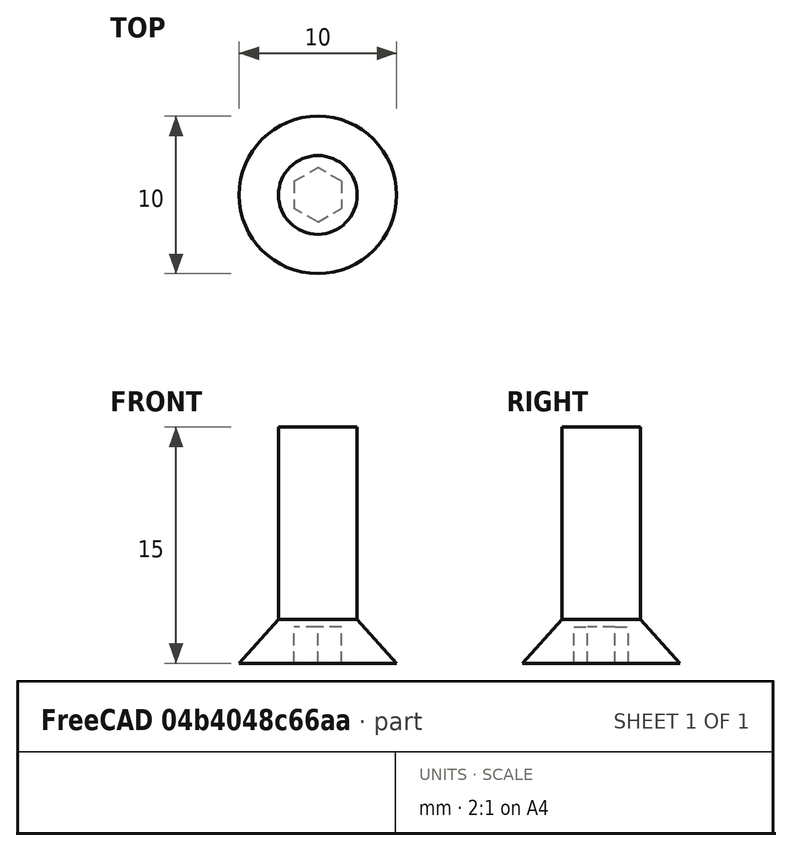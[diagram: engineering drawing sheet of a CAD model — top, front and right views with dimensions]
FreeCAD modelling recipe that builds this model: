
FCSTD DOCUMENT  (FreeCAD 1.0R39109 (Git))
Label: dbox_asm
License: All rights reserved
LicenseURL: https://en.wikipedia.org/wiki/All_rights_reserved
objects: App::Link×162, App::FeaturePython×132, Assembly::AssemblyLink×11, Assembly::JointGroup×2, Part::Feature×1, Assembly::AssemblyObject×1
note: 1 computed .brp shape members not serialized (recipe doc carries the construction recipe); baked Part::Feature solids carry a one-line shape summary decoded from their .brp
EXTERNAL_REF file=../parts/T-Slot_20_height.FCStd obj=Body
EXTERNAL_REF file=../parts/T-Slot_20_length.FCStd obj=Body
EXTERNAL_REF file=../parts/T-Slot_20_width.FCStd obj=Body
EXTERNAL_REF file=../downloads/2020-corner-bracket.FCStd obj=Part
EXTERNAL_REF file=../parts/T-nut_20.FCStd obj=Part__Feature
EXTERNAL_REF file=roof_holder_asm.FCStd obj=Assembly
EXTERNAL_REF file=roof_holder_asm.FCStd obj=roof_holder
EXTERNAL_REF file=roof_holder_asm.FCStd obj=Hex_socket_countersunk_head_screw_ISO_10642_M5_15_0
EXTERNAL_REF file=roof_holder_asm.FCStd obj=Hex_socket_countersunk_head_screw_ISO_10642_M5_15_001
EXTERNAL_REF file=asm_roof.FCStd obj=Assembly
EXTERNAL_REF file=asm_roof.FCStd obj=plate_roof001
EXTERNAL_REF file=asm_roof.FCStd obj=linear_slide
EXTERNAL_REF file=asm_roof.FCStd obj=linear_slide001
EXTERNAL_REF file=asm_roof.FCStd obj=asm_SHF002
EXTERNAL_REF file=asm_shf.FCStd obj=SHF12
EXTERNAL_REF file=asm_shf.FCStd obj=Hex_socket_head_cap_screw_DIN_912_M4_15_0
EXTERNAL_REF file=asm_shf.FCStd obj=Hex_socket_head_cap_screw_DIN_912_M5_15_0
EXTERNAL_REF file=asm_shf.FCStd obj=Hex_socket_head_cap_screw_DIN_912_M5_15_001
EXTERNAL_REF file=asm_roof.FCStd obj=asm_SHF003
EXTERNAL_REF file=asm_roof.FCStd obj=asm_cam_holder
EXTERNAL_REF file=asm_plate_front_back.FCStd obj=Assembly
EXTERNAL_REF file=asm_plate_front_back.FCStd obj=plate_front_back
EXTERNAL_REF file=asm_plate_front_back.FCStd obj=Hex_screw_M5_10_001
EXTERNAL_REF file=asm_plate_front_back.FCStd obj=Hex_screw_M5_10_002
EXTERNAL_REF file=asm_plate_front_back.FCStd obj=Hex_screw_M5_10_003
EXTERNAL_REF file=asm_plate_front_back.FCStd obj=Hex_screw_M5_10_0
EXTERNAL_REF file=asm_plate_side.FCStd obj=Assembly
EXTERNAL_REF file=asm_plate_side.FCStd obj=plate_side
EXTERNAL_REF file=asm_plate_side.FCStd obj=TAH15_M5_L6
EXTERNAL_REF file=asm_plate_side.FCStd obj=TAH15_M5_L007
EXTERNAL_REF file=asm_plate_side.FCStd obj=TAH15_M5_L008
EXTERNAL_REF file=asm_plate_side.FCStd obj=TAH15_M5_L009
EXTERNAL_REF file=../secondary/bolts.FCStd obj=Body004

FEATURE [App::Link] Tslot20_heigh
  LinkedObject = -> <external ../parts/T-Slot_20_height.FCStd>#Body
FEATURE [App::FeaturePython] GroundedJoint  # Assembly grounded joint (typed FeaturePython)
  ObjectToGround = -> Tslot20_heigh
FEATURE [App::Link] Tslot20_len
  LinkPlacement = pos=(10,4e-16,570) rot=(0,1,0;1.5708rad)
  LinkedObject = -> <external ../parts/T-Slot_20_length.FCStd>#Body
  Placement = pos=(10,4e-16,570) rot=(0,1,0;1.5708rad)
FEATURE [App::FeaturePython] Joint  label="Fixed"  # Assembly joint (typed FeaturePython)
  Activated = true
  AngleMax = 0
  AngleMin = 0
  Detach1 = false
  Detach2 = false
  Distance = 0
  Distance2 = 0
  EnableAngleMax = false
  EnableAngleMin = false
  EnableLengthMax = false
  EnableLengthMin = false
  JointType = 0 (Fixed)
  LengthMax = 0
  LengthMin = 0
  Offset2 = pos=(0,0,0) rot=(0,0,1;1.5708rad)
  Placement1 = pos=(10,-6.55,580) rot=(-0.57735,-0.57735,0.57735;4.18879rad)
  Placement2 = pos=(-10,-6.55,1.8e-15) rot=(1,0,0;4.71239rad)
  Reference1 = -> Assembly [Tslot20_heigh.Edge52,Tslot20_heigh.Edge52]
  Reference2 = -> Assembly [Tslot20_len.Edge39,Tslot20_len.Edge39]
FEATURE [App::Link] Tslot20_heigh001
  LinkPlacement = pos=(420,3.92e-14,-5.3e-14) rot=(0,0,1;0rad)
  LinkedObject = -> <external ../parts/T-Slot_20_height.FCStd>#Body
  Placement = pos=(420,3.92e-14,-5.3e-14) rot=(0,0,1;0rad)
FEATURE [App::FeaturePython] Joint001  label="Fixed001"  # Assembly joint (typed FeaturePython)
  Activated = true
  AngleMax = 0
  AngleMin = 0
  Detach1 = false
  Detach2 = false
  Distance = 0
  Distance2 = 0
  EnableAngleMax = false
  EnableAngleMin = false
  EnableLengthMax = false
  EnableLengthMin = false
  JointType = 0 (Fixed)
  LengthMax = 0
  LengthMin = 0
  Offset2 = pos=(0,0,0) rot=(0,0,1;1.5708rad)
  Placement1 = pos=(-10,6.55,400) rot=(0.57735,0.57735,0.57735;4.18879rad)
  Placement2 = pos=(-10,6.55,580) rot=(1,0,0;4.71239rad)
  Reference1 = -> Assembly [Tslot20_len.Edge68,Tslot20_len.Edge68]
  Reference2 = -> Assembly [Tslot20_heigh001.Edge68,Tslot20_heigh001.Edge68]
FEATURE [App::Link] Tslot20_wid
  LinkPlacement = pos=(7e-16,10,570) rot=(0.57735,0.57735,0.57735;4.18879rad)
  LinkedObject = -> <external ../parts/T-Slot_20_width.FCStd>#Body
  Placement = pos=(7e-16,10,570) rot=(0.57735,0.57735,0.57735;4.18879rad)
FEATURE [App::FeaturePython] Joint002  label="Fixed002"  # Assembly joint (typed FeaturePython)
  Activated = true
  AngleMax = 0
  AngleMin = 0
  Detach1 = false
  Detach2 = false
  Distance = 0
  Distance2 = 0
  EnableAngleMax = false
  EnableAngleMin = false
  EnableLengthMax = false
  EnableLengthMin = false
  JointType = 0 (Fixed)
  LengthMax = 0
  LengthMin = 0
  Offset2 = pos=(0,0,0) rot=(0,0,1;1.5708rad)
  Placement1 = pos=(10,-6.55,0) rot=(-0.57735,-0.57735,0.57735;4.18879rad)
  Placement2 = pos=(-6.55,10,580) rot=(0.57735,-0.57735,0.57735;4.18879rad)
  Reference1 = -> Assembly [Tslot20_wid.Edge14,Tslot20_wid.Edge14]
  Reference2 = -> Assembly [Tslot20_heigh.Edge3,Tslot20_heigh.Edge3]
FEATURE [App::Link] Tslot20_heigh002
  LinkPlacement = pos=(1e-16,220,-3.59e-14) rot=(0,0,1;0rad)
  LinkedObject = -> <external ../parts/T-Slot_20_height.FCStd>#Body
  Placement = pos=(1e-16,220,-3.59e-14) rot=(0,0,1;0rad)
FEATURE [App::FeaturePython] Joint003  label="Fixed003"  # Assembly joint (typed FeaturePython)
  Activated = true
  AngleMax = 0
  AngleMin = 0
  Detach1 = false
  Detach2 = false
  Distance = 0
  Distance2 = 0
  EnableAngleMax = false
  EnableAngleMin = false
  EnableLengthMax = false
  EnableLengthMin = false
  JointType = 0 (Fixed)
  LengthMax = 0
  LengthMin = 0
  Offset2 = pos=(0,0,0) rot=(0,0,1;1.5708rad)
  Placement1 = pos=(10,-6.55,200) rot=(-0.57735,-0.57735,0.57735;4.18879rad)
  Placement2 = pos=(-6.55,-10,580) rot=(-0.57735,0.57735,0.57735;4.18879rad)
  Reference1 = -> Assembly [Tslot20_wid.Edge52,Tslot20_wid.Edge52]
  Reference2 = -> Assembly [Tslot20_heigh002.Edge43,Tslot20_heigh002.Edge43]
FEATURE [App::Link] Tslot20_len001
  LinkPlacement = pos=(10,220,570) rot=(0,1,0;1.5708rad)
  LinkedObject = -> <external ../parts/T-Slot_20_length.FCStd>#Body
  Placement = pos=(10,220,570) rot=(0,1,0;1.5708rad)
FEATURE [App::FeaturePython] Joint004  label="Fixed004"  # Assembly joint (typed FeaturePython)
  Activated = true
  AngleMax = 0
  AngleMin = 0
  Detach1 = false
  Detach2 = false
  Distance = 0
  Distance2 = 0
  EnableAngleMax = false
  EnableAngleMin = false
  EnableLengthMax = false
  EnableLengthMin = false
  JointType = 0 (Fixed)
  LengthMax = 0
  LengthMin = 0
  Offset2 = pos=(0,0,0) rot=(0,0,1;1.5708rad)
  Placement1 = pos=(10,6.55,580) rot=(-0.57735,-0.57735,0.57735;4.18879rad)
  Placement2 = pos=(-10,6.55,-1.8e-15) rot=(1,0,0;4.71239rad)
  Reference1 = -> Assembly [Tslot20_heigh002.Edge60,Tslot20_heigh002.Edge60]
  Reference2 = -> Assembly [Tslot20_len001.Edge31,Tslot20_len001.Edge31]
FEATURE [App::Link] Tslot20_heigh003
  LinkPlacement = pos=(420,220,-8.25e-14) rot=(0,0,1;0rad)
  LinkedObject = -> <external ../parts/T-Slot_20_height.FCStd>#Body
  Placement = pos=(420,220,-8.25e-14) rot=(0,0,1;0rad)
FEATURE [App::FeaturePython] Joint005  label="Fixed005"  # Assembly joint (typed FeaturePython)
  Activated = true
  AngleMax = 0
  AngleMin = 0
  Detach1 = false
  Detach2 = false
  Distance = 0
  Distance2 = 0
  EnableAngleMax = false
  EnableAngleMin = false
  EnableLengthMax = false
  EnableLengthMin = false
  JointType = 0 (Fixed)
  LengthMax = 0
  LengthMin = 0
  Offset2 = pos=(0,0,0) rot=(0,0,1;1.5708rad)
  Placement1 = pos=(-10,6.55,400) rot=(0.57735,0.57735,0.57735;4.18879rad)
  Placement2 = pos=(-10,6.55,580) rot=(1,0,0;4.71239rad)
  Reference1 = -> Assembly [Tslot20_len001.Edge68,Tslot20_len001.Edge68]
  Reference2 = -> Assembly [Tslot20_heigh003.Edge68,Tslot20_heigh003.Edge68]
FEATURE [App::Link] Tslot20_wid001
  LinkPlacement = pos=(420,10,570) rot=(-1,0,0;1.5708rad)
  LinkedObject = -> <external ../parts/T-Slot_20_width.FCStd>#Body
  Placement = pos=(420,10,570) rot=(-1,0,0;1.5708rad)
FEATURE [App::FeaturePython] Joint006  label="Fixed006"  # Assembly joint (typed FeaturePython)
  Activated = true
  AngleMax = 0
  AngleMin = 0
  Detach1 = false
  Detach2 = false
  Distance = 0
  Distance2 = 0
  EnableAngleMax = false
  EnableAngleMin = false
  EnableLengthMax = false
  EnableLengthMin = false
  JointType = 0 (Fixed)
  LengthMax = 0
  LengthMin = 0
  Offset2 = pos=(0,0,0) rot=(0,0,1;1.5708rad)
  Placement1 = pos=(6.55,10,580) rot=(0.707107,0,0.707107;3.14159rad)
  Placement2 = pos=(6.55,-10,-1.8e-15) rot=(-0.57735,0.57735,0.57735;4.18879rad)
  Reference1 = -> Assembly [Tslot20_heigh001.Edge61,Tslot20_heigh001.Edge61]
  Reference2 = -> Assembly [Tslot20_wid001.Edge13,Tslot20_wid001.Edge13]
FEATURE [App::Link] Tslot20_len002
  LinkPlacement = pos=(10,2.9e-15,10) rot=(0,1,0;1.5708rad)
  LinkedObject = -> <external ../parts/T-Slot_20_length.FCStd>#Body
  Placement = pos=(10,2.9e-15,10) rot=(0,1,0;1.5708rad)
FEATURE [App::FeaturePython] Joint007  label="Fixed007"  # Assembly joint (typed FeaturePython)
  Activated = true
  AngleMax = 0
  AngleMin = 0
  Detach1 = false
  Detach2 = false
  Distance = 0
  Distance2 = 0
  EnableAngleMax = false
  EnableAngleMin = false
  EnableLengthMax = false
  EnableLengthMin = false
  JointType = 0 (Fixed)
  LengthMax = 0
  LengthMin = 0
  Offset2 = pos=(0,0,0) rot=(0,0,-1;1.5708rad)
  Placement1 = pos=(10,6.55,0) rot=(-0.57735,-0.57735,0.57735;4.18879rad)
  Placement2 = pos=(10,6.55,0) rot=(0,-0.707107,0.707107;3.14159rad)
  Reference1 = -> Assembly [Tslot20_len002.Edge22,Tslot20_len002.Edge22]
  Reference2 = -> Assembly [Tslot20_heigh.Edge22,Tslot20_heigh.Edge22]
FEATURE [App::Link] Tslot20_len003
  LinkPlacement = pos=(10,220,10) rot=(0,1,0;1.5708rad)
  LinkedObject = -> <external ../parts/T-Slot_20_length.FCStd>#Body
  Placement = pos=(10,220,10) rot=(0,1,0;1.5708rad)
FEATURE [App::FeaturePython] Joint008  label="Fixed008"  # Assembly joint (typed FeaturePython)
  Activated = true
  AngleMax = 0
  AngleMin = 0
  Detach1 = false
  Detach2 = false
  Distance = 0
  Distance2 = 0
  EnableAngleMax = false
  EnableAngleMin = false
  EnableLengthMax = false
  EnableLengthMin = false
  JointType = 0 (Fixed)
  LengthMax = 0
  LengthMin = 0
  Offset2 = pos=(0,0,0) rot=(0,0,-1;1.5708rad)
  Placement1 = pos=(-10,6.55,0) rot=(0.57735,0.57735,0.57735;4.18879rad)
  Placement2 = pos=(10,6.55,400) rot=(0,-0.707107,0.707107;3.14159rad)
  Reference1 = -> Assembly [Tslot20_heigh003.Edge31,Tslot20_heigh003.Edge31]
  Reference2 = -> Assembly [Tslot20_len003.Edge60,Tslot20_len003.Edge60]
FEATURE [App::Link] Tslot20_wid002
  LinkPlacement = pos=(-6.2e-15,10,30) rot=(1,0,0;4.71239rad)
  LinkedObject = -> <external ../parts/T-Slot_20_width.FCStd>#Body
  Placement = pos=(-6.2e-15,10,30) rot=(1,0,0;4.71239rad)
FEATURE [App::Link] Tslot20_wid003
  LinkPlacement = pos=(420,210,30) rot=(1,0,0;1.5708rad)
  LinkedObject = -> <external ../parts/T-Slot_20_width.FCStd>#Body
  Placement = pos=(420,210,30) rot=(1,0,0;1.5708rad)
FEATURE [App::FeaturePython] Joint009  label="Fixed009"  # Assembly joint (typed FeaturePython)
  Activated = true
  AngleMax = 0
  AngleMin = 0
  Detach1 = false
  Detach2 = false
  Distance = 0
  Distance2 = 0
  EnableAngleMax = false
  EnableAngleMin = false
  EnableLengthMax = false
  EnableLengthMin = false
  JointType = 0 (Fixed)
  LengthMax = 0
  LengthMin = 0
  Offset2 = pos=(0,-20,0) rot=(0,0,-1;1.5708rad)
  Placement1 = pos=(-6.55,-10,0) rot=(-0.707107,0,0.707107;3.14159rad)
  Placement2 = pos=(-6.55,30,200) rot=(0.57735,0.57735,0.57735;2.0944rad)
  Reference1 = -> Assembly [Tslot20_heigh002.Edge5,Tslot20_heigh002.Edge5]
  Reference2 = -> Assembly [Tslot20_wid002.Edge3,Tslot20_wid002.Edge3]
FEATURE [App::FeaturePython] Joint010  label="Fixed010"  # Assembly joint (typed FeaturePython)
  Activated = true
  AngleMax = 0
  AngleMin = 0
  Detach1 = false
  Detach2 = false
  Distance = 0
  Distance2 = 0
  EnableAngleMax = false
  EnableAngleMin = false
  EnableLengthMax = false
  EnableLengthMin = false
  JointType = 0 (Fixed)
  LengthMax = 0
  LengthMin = 0
  Offset2 = pos=(0,20,0) rot=(0,0,-1;1.5708rad)
  Placement1 = pos=(6.55,10,0) rot=(0.707107,0,0.707107;3.14159rad)
  Placement2 = pos=(6.55,-30,200) rot=(-0.57735,-0.57735,0.57735;2.0944rad)
  Reference1 = -> Assembly [Tslot20_heigh001.Edge23,Tslot20_heigh001.Edge23]
  Reference2 = -> Assembly [Tslot20_wid003.Edge51,Tslot20_wid003.Edge51]
FEATURE [App::Link] Body  label="corner1"
  LinkPlacement = pos=(20,-0.05,30) rot=(0,0,1;0rad)
  LinkedObject = -> <external ../downloads/2020-corner-bracket.FCStd>#Part
  Placement = pos=(20,-0.05,30) rot=(0,0,1;0rad)
FEATURE [App::FeaturePython] Joint011  label="Fixed011"  # Assembly joint (typed FeaturePython)
  Activated = true
  AngleMax = 0
  AngleMin = 0
  Detach1 = false
  Detach2 = false
  Distance = 0
  Distance2 = 0
  EnableAngleMax = false
  EnableAngleMin = false
  EnableLengthMax = false
  EnableLengthMin = false
  JointType = 0 (Fixed)
  LengthMax = 0
  LengthMin = 0
  Offset2 = pos=(0,0,-2) rot=(0,0,1;1.5708rad)
  Placement1 = pos=(-10,-8.5,-10) rot=(-0.57735,-0.57735,0.57735;4.18879rad)
  Placement2 = pos=(-10,-8.55,-1.8e-15) rot=(1,0,0;4.71239rad)
  Reference1 = -> Assembly [Body.Edge15,Body.Vertex13]
  Reference2 = -> Assembly [Tslot20_len002.Edge39,Tslot20_len002.Edge39]
FEATURE [App::Link] Body001  label="corner2"
  LinkPlacement = pos=(0.05,200,50) rot=(0,0,-1;1.5708rad)
  LinkedObject = -> <external ../downloads/2020-corner-bracket.FCStd>#Part
  Placement = pos=(0.05,200,50) rot=(0,0,-1;1.5708rad)
FEATURE [App::Link] Body002  label="corner3"
  LinkPlacement = pos=(0.05,20,50) rot=(0,0,1;1.5708rad)
  LinkedObject = -> <external ../downloads/2020-corner-bracket.FCStd>#Part
  Placement = pos=(0.05,20,50) rot=(0,0,1;1.5708rad)
FEATURE [App::Link] Body003  label="corner4"
  LinkPlacement = pos=(20,-0.05,550) rot=(0,1,0;1.5708rad)
  LinkedObject = -> <external ../downloads/2020-corner-bracket.FCStd>#Part
  Placement = pos=(20,-0.05,550) rot=(0,1,0;1.5708rad)
FEATURE [App::FeaturePython] Joint012  label="Fixed012"  # Assembly joint (typed FeaturePython)
  Activated = true
  AngleMax = 0
  AngleMin = 0
  Detach1 = false
  Detach2 = false
  Distance = 0
  Distance2 = 0
  EnableAngleMax = false
  EnableAngleMin = false
  EnableLengthMax = false
  EnableLengthMin = false
  JointType = 0 (Fixed)
  LengthMax = 0
  LengthMin = 0
  Offset2 = pos=(0,0,-2) rot=(0,0,-1;1.5708rad)
  Placement1 = pos=(6.55,-10,0) rot=(-0.707107,0,0.707107;3.14159rad)
  Placement2 = pos=(-10,-6.5,-10) rot=(0,-0.707107,0.707107;3.14159rad)
  Reference1 = -> Assembly [Tslot20_wid002.Edge13,Tslot20_wid002.Edge13]
  Reference2 = -> Assembly [Body002.Edge15,Body002.Vertex13]
FEATURE [App::FeaturePython] Joint013  label="Fixed013"  # Assembly joint (typed FeaturePython)
  Activated = true
  AngleMax = 0
  AngleMin = 0
  Detach1 = false
  Detach2 = false
  Distance = 0
  Distance2 = 0
  EnableAngleMax = false
  EnableAngleMin = false
  EnableLengthMax = false
  EnableLengthMin = false
  JointType = 0 (Fixed)
  LengthMax = 0
  LengthMin = 0
  Offset2 = pos=(0,0,2) rot=(0,0,1;1.5708rad)
  Placement1 = pos=(6.55,-10,200) rot=(-0.707107,0,0.707107;3.14159rad)
  Placement2 = pos=(-10,6.5,-10) rot=(-1,0,0;4.71239rad)
  Reference1 = -> Assembly [Tslot20_wid002.Edge51,Tslot20_wid002.Edge51]
  Reference2 = -> Assembly [Body001.Edge15,Body001.Vertex12]
FEATURE [App::FeaturePython] Joint014  label="Fixed014"  # Assembly joint (typed FeaturePython)
  Activated = true
  AngleMax = 0
  AngleMin = 0
  Detach1 = false
  Detach2 = false
  Distance = 0
  Distance2 = 0
  EnableAngleMax = false
  EnableAngleMin = false
  EnableLengthMax = false
  EnableLengthMin = false
  JointType = 0 (Fixed)
  LengthMax = 0
  LengthMin = 0
  Offset2 = pos=(0,0,-2) rot=(0,0,1;0rad)
  Placement1 = pos=(10,-6.55,0) rot=(-0.57735,-0.57735,0.57735;4.18879rad)
  Placement2 = pos=(-10,-6.5,-10) rot=(-0.57735,-0.57735,0.57735;4.18879rad)
  Reference1 = -> Assembly [Tslot20_len.Edge14,Tslot20_len.Edge14]
  Reference2 = -> Assembly [Body003.Edge15,Body003.Vertex13]
FEATURE [App::Link] Body004  label="corner5"
  LinkPlacement = pos=(20,220.05,30) rot=(0,0,1;0rad)
  LinkedObject = -> <external ../downloads/2020-corner-bracket.FCStd>#Part
  Placement = pos=(20,220.05,30) rot=(0,0,1;0rad)
FEATURE [App::FeaturePython] Joint015  label="Fixed015"  # Assembly joint (typed FeaturePython)
  Activated = true
  AngleMax = 0
  AngleMin = 0
  Detach1 = false
  Detach2 = false
  Distance = 0
  Distance2 = 0
  EnableAngleMax = false
  EnableAngleMin = false
  EnableLengthMax = false
  EnableLengthMin = false
  JointType = 0 (Fixed)
  LengthMax = 0
  LengthMin = 0
  Offset2 = pos=(0,0,2) rot=(0,0,1;1.5708rad)
  Placement1 = pos=(-10,6.55,-1.8e-15) rot=(0.57735,0.57735,0.57735;4.18879rad)
  Placement2 = pos=(-10,6.5,-10) rot=(-1,0,0;4.71239rad)
  Reference1 = -> Assembly [Tslot20_len003.Edge31,Tslot20_len003.Edge31]
  Reference2 = -> Assembly [Body004.Edge15,Body004.Vertex12]
FEATURE [App::Link] Body005  label="corner6"
  LinkPlacement = pos=(-0.05,200,550) rot=(-0.707107,0.707107,0;3.14159rad)
  LinkedObject = -> <external ../downloads/2020-corner-bracket.FCStd>#Part
  Placement = pos=(-0.05,200,550) rot=(-0.707107,0.707107,0;3.14159rad)
FEATURE [App::Link] Body006  label="corner7"
  LinkPlacement = pos=(-0.55,20,550) rot=(-0.57735,0.57735,0.57735;2.0944rad)
  LinkedObject = -> <external ../downloads/2020-corner-bracket.FCStd>#Part
  Placement = pos=(-0.55,20,550) rot=(-0.57735,0.57735,0.57735;2.0944rad)
FEATURE [App::Link] Body007  label="corner8"
  LinkPlacement = pos=(400,219.45,30) rot=(0,0,1;3.14159rad)
  LinkedObject = -> <external ../downloads/2020-corner-bracket.FCStd>#Part
  Placement = pos=(400,219.45,30) rot=(0,0,1;3.14159rad)
FEATURE [App::Link] Body008  label="corner9"
  LinkPlacement = pos=(20,219.6,550) rot=(0,1,0;1.5708rad)
  LinkedObject = -> <external ../downloads/2020-corner-bracket.FCStd>#Part
  Placement = pos=(20,219.6,550) rot=(0,1,0;1.5708rad)
FEATURE [App::FeaturePython] Joint016  label="Fixed016"  # Assembly joint (typed FeaturePython)
  Activated = true
  AngleMax = 0
  AngleMin = 0
  Detach1 = false
  Detach2 = false
  Distance = 0
  Distance2 = 0
  EnableAngleMax = false
  EnableAngleMin = false
  EnableLengthMax = false
  EnableLengthMin = false
  JointType = 0 (Fixed)
  LengthMax = 0
  LengthMin = 0
  Offset2 = pos=(0,0,-6) rot=(0,0,1;3.14159rad)
  Placement1 = pos=(-10,-6.55,0) rot=(0.57735,0.57735,0.57735;4.18879rad)
  Placement2 = pos=(-10,6,-10) rot=(-0.57735,0.57735,-0.57735;4.18879rad)
  Reference1 = -> Assembly [Tslot20_wid.Edge39,Tslot20_wid.Edge39]
  Reference2 = -> Assembly [Body006.Edge15,Body006.Edge15]
FEATURE [App::FeaturePython] Joint017  label="Fixed017"  # Assembly joint (typed FeaturePython)
  Activated = true
  AngleMax = 0
  AngleMin = 0
  Detach1 = false
  Detach2 = false
  Distance = 0
  Distance2 = 0
  EnableAngleMax = false
  EnableAngleMin = false
  EnableLengthMax = false
  EnableLengthMin = false
  JointType = 0 (Fixed)
  LengthMax = 0
  LengthMin = 0
  Offset2 = pos=(0,0,-6) rot=(0,0,-1;1.5708rad)
  Placement1 = pos=(-10,-6.55,400) rot=(0.57735,0.57735,0.57735;4.18879rad)
  Placement2 = pos=(-10,6,-10) rot=(0,-0.707107,0.707107;3.14159rad)
  Reference1 = -> Assembly [Tslot20_len003.Edge76,Tslot20_len003.Edge76]
  Reference2 = -> Assembly [Body007.Edge15,Body007.Edge15]
FEATURE [App::FeaturePython] Joint018  label="Fixed018"  # Assembly joint (typed FeaturePython)
  Activated = true
  AngleMax = 0
  AngleMin = 0
  Detach1 = false
  Detach2 = false
  Distance = 0
  Distance2 = 0
  EnableAngleMax = false
  EnableAngleMin = false
  EnableLengthMax = false
  EnableLengthMin = false
  JointType = 0 (Fixed)
  LengthMax = 0
  LengthMin = 0
  Offset2 = pos=(0,0,2) rot=(0,0,-1;1.5708rad)
  Placement1 = pos=(-10,-6.55,200) rot=(0.57735,0.57735,0.57735;4.18879rad)
  Placement2 = pos=(-10,6.5,-10) rot=(0,-0.707107,0.707107;3.14159rad)
  Reference1 = -> Assembly [Tslot20_wid.Edge76,Tslot20_wid.Edge76]
  Reference2 = -> Assembly [Body005.Edge15,Body005.Vertex12]
FEATURE [App::FeaturePython] Joint019  label="Fixed019"  # Assembly joint (typed FeaturePython)
  Activated = true
  AngleMax = 0
  AngleMin = 0
  Detach1 = false
  Detach2 = false
  Distance = 0
  Distance2 = 0
  EnableAngleMax = false
  EnableAngleMin = false
  EnableLengthMax = false
  EnableLengthMin = false
  JointType = 0 (Fixed)
  LengthMax = 0
  LengthMin = 0
  Offset2 = pos=(0,0,-12) rot=(0,0,1;0rad)
  Placement1 = pos=(10,3.1,0) rot=(-0.57735,-0.57735,0.57735;4.18879rad)
  Placement2 = pos=(-10,3.5,-10) rot=(-0.57735,-0.57735,0.57735;4.18879rad)
  Reference1 = -> Assembly [Tslot20_len001.Edge22,Tslot20_len001.Vertex22]
  Reference2 = -> Assembly [Body008.Edge15,Body008.Vertex13]
FEATURE [App::Link] Body009  label="corner10"
  LinkPlacement = pos=(400,219.45,550) rot=(0,1,0;3.14159rad)
  LinkedObject = -> <external ../downloads/2020-corner-bracket.FCStd>#Part
  Placement = pos=(400,219.45,550) rot=(0,1,0;3.14159rad)
FEATURE [App::Link] Body010  label="corner11"
  LinkPlacement = pos=(420.45,200,550) rot=(0.57735,0.57735,-0.57735;2.0944rad)
  LinkedObject = -> <external ../downloads/2020-corner-bracket.FCStd>#Part
  Placement = pos=(420.45,200,550) rot=(0.57735,0.57735,-0.57735;2.0944rad)
FEATURE [App::Link] Body011  label="corner12"
  LinkPlacement = pos=(419.95,200,50) rot=(0,0,1;4.71239rad)
  LinkedObject = -> <external ../downloads/2020-corner-bracket.FCStd>#Part
  Placement = pos=(419.95,200,50) rot=(0,0,1;4.71239rad)
FEATURE [App::FeaturePython] Joint020  label="Fixed020"  # Assembly joint (typed FeaturePython)
  Activated = true
  AngleMax = 0
  AngleMin = 0
  Detach1 = false
  Detach2 = false
  Distance = 0
  Distance2 = 0
  EnableAngleMax = false
  EnableAngleMin = false
  EnableLengthMax = false
  EnableLengthMin = false
  JointType = 0 (Fixed)
  LengthMax = 0
  LengthMin = 0
  Offset2 = pos=(0,0,-6) rot=(0,0,-1;1.5708rad)
  Placement1 = pos=(-10,0,-10) rot=(-0.57735,-0.57735,0.57735;4.18879rad)
  Placement2 = pos=(10,-0.55,400) rot=(0,-0.707107,0.707107;3.14159rad)
  Reference1 = -> Assembly [Body009.Edge15,Body009.Edge15]
  Reference2 = -> Assembly [Tslot20_len001.Edge52,Tslot20_len001.Edge52]
FEATURE [App::FeaturePython] Joint021  label="Fixed021"  # Assembly joint (typed FeaturePython)
  Activated = true
  AngleMax = 0
  AngleMin = 0
  Detach1 = false
  Detach2 = false
  Distance = 0
  Distance2 = 0
  EnableAngleMax = false
  EnableAngleMin = false
  EnableLengthMax = false
  EnableLengthMin = false
  JointType = 0 (Fixed)
  LengthMax = 0
  LengthMin = 0
  Offset2 = pos=(0,0,7) rot=(0,0,1;0rad)
  Placement1 = pos=(-6.55,10,200) rot=(0.707107,0,0.707107;3.14159rad)
  Placement2 = pos=(-10,-7,-10) rot=(-0.57735,-0.57735,0.57735;4.18879rad)
  Reference1 = -> Assembly [Tslot20_wid001.Edge3,Tslot20_wid001.Edge3]
  Reference2 = -> Assembly [Body010.Edge15,Body010.Edge15]
FEATURE [App::FeaturePython] Joint022  label="Fixed022"  # Assembly joint (typed FeaturePython)
  Activated = true
  AngleMax = 0
  AngleMin = 0
  Detach1 = false
  Detach2 = false
  Distance = 0
  Distance2 = 0
  EnableAngleMax = false
  EnableAngleMin = false
  EnableLengthMax = false
  EnableLengthMin = false
  JointType = 0 (Fixed)
  LengthMax = 0
  LengthMin = 0
  Offset2 = pos=(0,0,15) rot=(0,0,1;1.5708rad)
  Placement1 = pos=(-6.55,10,0) rot=(0.707107,0,0.707107;3.14159rad)
  Placement2 = pos=(-10,-6.5,-10) rot=(-1,0,0;4.71239rad)
  Reference1 = -> Assembly [Tslot20_wid003.Edge1,Tslot20_wid003.Edge1]
  Reference2 = -> Assembly [Body011.Edge15,Body011.Vertex12]
FEATURE [App::Link] Body012  label="Body"
  LinkPlacement = pos=(419.45,20,550) rot=(0.707107,0.707107,0;3.14159rad)
  LinkedObject = -> <external ../downloads/2020-corner-bracket.FCStd>#Part
  Placement = pos=(419.45,20,550) rot=(0.707107,0.707107,0;3.14159rad)
FEATURE [App::Link] Body013
  LinkPlacement = pos=(400,-0.05,550) rot=(-0.707107,0,0.707107;3.14159rad)
  LinkedObject = -> <external ../downloads/2020-corner-bracket.FCStd>#Part
  Placement = pos=(400,-0.05,550) rot=(-0.707107,0,0.707107;3.14159rad)
FEATURE [App::FeaturePython] Joint023  label="Fixed023"  # Assembly joint (typed FeaturePython)
  Activated = true
  AngleMax = 0
  AngleMin = 0
  Detach1 = false
  Detach2 = false
  Distance = 0
  Distance2 = 0
  EnableAngleMax = false
  EnableAngleMin = false
  EnableLengthMax = false
  EnableLengthMin = false
  JointType = 0 (Fixed)
  LengthMax = 0
  LengthMin = 0
  Offset2 = pos=(0,0,6) rot=(0,0,1;1.5708rad)
  Placement1 = pos=(-6.55,10,0) rot=(0.707107,0,0.707107;3.14159rad)
  Placement2 = pos=(-10,-6,-10) rot=(-1,0,0;4.71239rad)
  Reference1 = -> Assembly [Tslot20_wid001.Edge1,Tslot20_wid001.Edge1]
  Reference2 = -> Assembly [Body012.Edge15,Body012.Edge15]
FEATURE [App::Link] Body014
  LinkPlacement = pos=(400,0.45,30) rot=(0,-1,0;1.5708rad)
  LinkedObject = -> <external ../downloads/2020-corner-bracket.FCStd>#Part
  Placement = pos=(400,0.45,30) rot=(0,-1,0;1.5708rad)
FEATURE [App::Link] Body015
  LinkPlacement = pos=(420.45,20,50) rot=(-0.57735,-0.57735,-0.57735;2.0944rad)
  LinkedObject = -> <external ../downloads/2020-corner-bracket.FCStd>#Part
  Placement = pos=(420.45,20,50) rot=(-0.57735,-0.57735,-0.57735;2.0944rad)
FEATURE [App::FeaturePython] Joint025  label="Fixed025"  # Assembly joint (typed FeaturePython)
  Activated = true
  AngleMax = 0
  AngleMin = 0
  Detach1 = false
  Detach2 = false
  Distance = 0
  Distance2 = 0
  EnableAngleMax = false
  EnableAngleMin = false
  EnableLengthMax = false
  EnableLengthMin = false
  JointType = 0 (Fixed)
  LengthMax = 0
  LengthMin = 0
  Offset2 = pos=(0,0,7) rot=(0,0,1;0rad)
  Placement1 = pos=(-6.55,10,200) rot=(0.707107,0,0.707107;3.14159rad)
  Placement2 = pos=(-10,-7,-10) rot=(-0.57735,-0.57735,0.57735;4.18879rad)
  Reference1 = -> Assembly [Tslot20_wid003.Edge3,Tslot20_wid003.Edge3]
  Reference2 = -> Assembly [Body015.Edge15,Body015.Edge15]
FEATURE [App::FeaturePython] Joint026  label="Fixed026"  # Assembly joint (typed FeaturePython)
  Activated = true
  AngleMax = 0
  AngleMin = 0
  Detach1 = false
  Detach2 = false
  Distance = 0
  Distance2 = 0
  EnableAngleMax = false
  EnableAngleMin = false
  EnableLengthMax = false
  EnableLengthMin = false
  JointType = 0 (Fixed)
  LengthMax = 0
  LengthMin = 0
  Offset2 = pos=(0,0,7) rot=(0,0,1;0rad)
  Placement1 = pos=(-10,-6.55,400) rot=(0.57735,0.57735,0.57735;4.18879rad)
  Placement2 = pos=(-10,-7,-10) rot=(-0.57735,-0.57735,0.57735;4.18879rad)
  Reference1 = -> Assembly [Tslot20_len002.Edge76,Tslot20_len002.Edge76]
  Reference2 = -> Assembly [Body014.Edge15,Body014.Edge15]
FEATURE [App::FeaturePython] Joint027  label="Fixed027"  # Assembly joint (typed FeaturePython)
  Activated = true
  AngleMax = 0
  AngleMin = 0
  Detach1 = false
  Detach2 = false
  Distance = 0
  Distance2 = 0
  EnableAngleMax = false
  EnableAngleMin = false
  EnableLengthMax = false
  EnableLengthMin = false
  JointType = 0 (Fixed)
  LengthMax = 0
  LengthMin = 0
  Offset2 = pos=(0,0,-15) rot=(0,0,1;3.14159rad)
  Placement1 = pos=(10,-6.55,400) rot=(-0.57735,-0.57735,0.57735;4.18879rad)
  Placement2 = pos=(-10,6.5,-10) rot=(-0.57735,0.57735,-0.57735;4.18879rad)
  Reference1 = -> Assembly [Tslot20_len.Edge52,Tslot20_len.Edge52]
  Reference2 = -> Assembly [Body013.Edge15,Body013.Vertex13]
FEATURE [App::Link] T_Nut_2020_M5  label="T-Nut_2020_M5"
  LinkPlacement = pos=(83.9077,212,570.1) rot=(0.57735,0.57735,-0.57735;2.0944rad)
  LinkedObject = -> <external ../parts/T-nut_20.FCStd>#Part__Feature
  Placement = pos=(83.9077,212,570.1) rot=(0.57735,0.57735,-0.57735;2.0944rad)
FEATURE [App::Link] T_Nut_2020_M006  label="T-Nut_2020_M006"
  LinkPlacement = pos=(107.908,212,570.1) rot=(0.57735,0.57735,-0.57735;2.0944rad)
  LinkedObject = -> <external ../parts/T-nut_20.FCStd>#Part__Feature
  Placement = pos=(107.908,212,570.1) rot=(0.57735,0.57735,-0.57735;2.0944rad)
FEATURE [App::FeaturePython] Joint028  label="Slider"  # Assembly joint (typed FeaturePython)
  Activated = true
  AngleMax = 0
  AngleMin = 0
  Detach1 = false
  Detach2 = false
  Distance = 0
  Distance2 = 0
  EnableAngleMax = false
  EnableAngleMin = false
  EnableLengthMax = false
  EnableLengthMin = false
  JointType = 3 (Slider)
  LengthMax = 0
  LengthMin = 0
  Offset1 = pos=(0,0,44) rot=(0,0,1;0rad)
  Offset2 = pos=(0,0,0) rot=(0,0,1;1.5708rad)
  Placement1 = pos=(-3,-44,0) rot=(-0.57735,-0.57735,0.57735;4.18879rad)
  Placement2 = pos=(-3.1,-8,-1.8e-15) rot=(0.707107,0.707107,0;3.14159rad)
  Reference1 = -> Assembly [T_Nut_2020_M5.Edge27,T_Nut_2020_M5.Edge27]
  Reference2 = -> Assembly [Tslot20_len001.Edge81,Tslot20_len001.Vertex7]
FEATURE [App::FeaturePython] Joint029  label="Slider001"  # Assembly joint (typed FeaturePython)
  Activated = true
  AngleMax = 0
  AngleMin = 0
  Detach1 = false
  Detach2 = false
  Distance = 0
  Distance2 = 0
  EnableAngleMax = false
  EnableAngleMin = false
  EnableLengthMax = false
  EnableLengthMin = false
  JointType = 3 (Slider)
  LengthMax = 0
  LengthMin = 0
  Offset2 = pos=(0,0,0) rot=(0,0,1;1.5708rad)
  Placement1 = pos=(-3,0,0) rot=(-0.57735,-0.57735,0.57735;4.18879rad)
  Placement2 = pos=(-3.1,-8,-1.8e-15) rot=(0.707107,0.707107,0;3.14159rad)
  Reference1 = -> Assembly [T_Nut_2020_M006.Edge27,T_Nut_2020_M006.Edge27]
  Reference2 = -> Assembly [Tslot20_len001.Edge81,Tslot20_len001.Vertex7]
FEATURE [Part::Feature] BOLTS_part  label="Hex socket countersunk head screw ISO 10642 M5 15.0"
  Placement = pos=(-103,0,0) rot=(0,0,1;0rad)
  shape: bbox 10 x 10 x 15 mm, 12 faces (baked)
FEATURE [App::Link] roof_holder001
  LinkPlacement = pos=(95.9077,208.636,570.1) rot=(1,0,0;1.5708rad)
  LinkedObject = -> <external roof_holder_asm.FCStd>#roof_holder
  Placement = pos=(95.9077,208.636,570.1) rot=(1,0,0;1.5708rad)
FEATURE [App::Link] Hex_socket_countersunk_head_screw_ISO_10642_M5_15_001  label="Hex socket countersunk head screw ISO 10642 M5 15.002"
  LinkPlacement = pos=(107.908,201.836,570.1) rot=(-1,0,0;1.5708rad)
  LinkedObject = -> <external roof_holder_asm.FCStd>#Hex_socket_countersunk_head_screw_ISO_10642_M5_15_0
  Placement = pos=(107.908,201.836,570.1) rot=(-1,0,0;1.5708rad)
FEATURE [App::Link] Hex_socket_countersunk_head_screw_ISO_10642_M5_15_002  label="Hex socket countersunk head screw ISO 10642 M5 15.003"
  LinkPlacement = pos=(83.9077,201.836,570.1) rot=(-1,0,0;1.5708rad)
  LinkedObject = -> <external roof_holder_asm.FCStd>#Hex_socket_countersunk_head_screw_ISO_10642_M5_15_001
  Placement = pos=(83.9077,201.836,570.1) rot=(-1,0,0;1.5708rad)
FEATURE [App::FeaturePython] Joint030  label="Slider002"  # Assembly joint (typed FeaturePython)
  Activated = true
  AngleMax = 0
  AngleMin = 0
  Detach1 = false
  Detach2 = false
  Distance = 0
  Distance2 = 0
  EnableAngleMax = false
  EnableAngleMin = false
  EnableLengthMax = false
  EnableLengthMin = false
  JointType = 3 (Slider)
  LengthMax = 0
  LengthMin = 0
  Offset2 = pos=(0,0,0) rot=(0,0,-1;1.5708rad)
  Placement1 = pos=(0,0,11.5) rot=(0,0,1;0rad)
  Placement2 = pos=(0,0,-1.5) rot=(-0.707107,-0.707107,0;3.14159rad)
  Reference1 = -> Assembly [asm_roof_holder.Hex_socket_countersunk_head_screw_ISO_10642_M5_15_001.Face4,asm_roof_holder.Hex_socket_countersunk_head_screw_ISO_10642_M5_15_001.Face4]
  Reference2 = -> Assembly [T_Nut_2020_M006.Face7,T_Nut_2020_M006.Face7]
FEATURE [App::FeaturePython] Joint031  label="Slider003"  # Assembly joint (typed FeaturePython)
  Activated = true
  AngleMax = 0
  AngleMin = 0
  Detach1 = false
  Detach2 = false
  Distance = 0
  Distance2 = 0
  EnableAngleMax = false
  EnableAngleMin = false
  EnableLengthMax = false
  EnableLengthMin = false
  JointType = 3 (Slider)
  LengthMax = 0
  LengthMin = 0
  Placement1 = pos=(0,0,0.6) rot=(-1,0,0;3.14159rad)
  Placement2 = pos=(0,0,11.5) rot=(0,0,1;0rad)
  Reference1 = -> Assembly [T_Nut_2020_M5.Face7,T_Nut_2020_M5.Edge3]
  Reference2 = -> Assembly [asm_roof_holder.Hex_socket_countersunk_head_screw_ISO_10642_M5_15_002.Face4,asm_roof_holder.Hex_socket_countersunk_head_screw_ISO_10642_M5_15_002.Face4]
FEATURE [App::Link] T_Nut_2020_M007  label="T-Nut_2020_M007"
  LinkPlacement = pos=(268.572,212,570.1) rot=(0.57735,0.57735,-0.57735;2.0944rad)
  LinkedObject = -> <external ../parts/T-nut_20.FCStd>#Part__Feature
  Placement = pos=(268.572,212,570.1) rot=(0.57735,0.57735,-0.57735;2.0944rad)
FEATURE [App::FeaturePython] Joint032  label="Slider004"  # Assembly joint (typed FeaturePython)
  Activated = true
  AngleMax = 0
  AngleMin = 0
  Detach1 = false
  Detach2 = false
  Distance = 0
  Distance2 = 0
  EnableAngleMax = false
  EnableAngleMin = false
  EnableLengthMax = false
  EnableLengthMin = false
  JointType = 3 (Slider)
  LengthMax = 0
  LengthMin = 0
  Offset1 = pos=(0,0,-100) rot=(0,0,1;0rad)
  Offset2 = pos=(0,0,0) rot=(0,0,1;1.5708rad)
  Placement1 = pos=(-3,100,0) rot=(-0.57735,-0.57735,0.57735;4.18879rad)
  Placement2 = pos=(-3.1,-8,400) rot=(0.707107,0.707107,0;3.14159rad)
  Reference1 = -> Assembly [T_Nut_2020_M007.Edge27,T_Nut_2020_M007.Edge27]
  Reference2 = -> Assembly [Tslot20_len001.Edge81,Tslot20_len001.Vertex43]
FEATURE [App::Link] T_Nut_2020_M008  label="T-Nut_2020_M008"
  LinkPlacement = pos=(292.572,212,570.1) rot=(0.57735,0.57735,-0.57735;2.0944rad)
  LinkedObject = -> <external ../parts/T-nut_20.FCStd>#Part__Feature
  Placement = pos=(292.572,212,570.1) rot=(0.57735,0.57735,-0.57735;2.0944rad)
FEATURE [App::FeaturePython] Joint033  label="Slider005"  # Assembly joint (typed FeaturePython)
  Activated = true
  AngleMax = 0
  AngleMin = 0
  Detach1 = false
  Detach2 = false
  Distance = 0
  Distance2 = 0
  EnableAngleMax = false
  EnableAngleMin = false
  EnableLengthMax = false
  EnableLengthMin = false
  JointType = 3 (Slider)
  LengthMax = 0
  LengthMin = 0
  Offset1 = pos=(0,0,-50) rot=(0,0,1;0rad)
  Offset2 = pos=(0,0,0) rot=(0,0,1;1.5708rad)
  Placement1 = pos=(-3,50,0) rot=(-0.57735,-0.57735,0.57735;4.18879rad)
  Placement2 = pos=(-3.1,-8,400) rot=(0.707107,0.707107,0;3.14159rad)
  Reference1 = -> Assembly [T_Nut_2020_M008.Edge27,T_Nut_2020_M008.Edge27]
  Reference2 = -> Assembly [Tslot20_len001.Edge81,Tslot20_len001.Vertex43]
FEATURE [App::Link] roof_holder
  LinkedObject = -> <external roof_holder_asm.FCStd>#roof_holder
FEATURE [App::Link] Hex_socket_countersunk_head_screw_ISO_10642_M5_15_0  label="Hex socket countersunk head screw ISO 10642 M5 15.004"
  LinkPlacement = pos=(12,7e-16,6.8) rot=(1,0,0;3.14159rad)
  LinkedObject = -> <external roof_holder_asm.FCStd>#Hex_socket_countersunk_head_screw_ISO_10642_M5_15_0
  Placement = pos=(12,7e-16,6.8) rot=(1,0,0;3.14159rad)
FEATURE [App::Link] Hex_socket_countersunk_head_screw_ISO_10642_M5_15_003  label="Hex socket countersunk head screw ISO 10642 M5 15.001"
  LinkPlacement = pos=(-12,7e-16,6.8) rot=(1,0,0;3.14159rad)
  LinkedObject = -> <external roof_holder_asm.FCStd>#Hex_socket_countersunk_head_screw_ISO_10642_M5_15_001
  Placement = pos=(-12,7e-16,6.8) rot=(1,0,0;3.14159rad)
FEATURE [Assembly::AssemblyLink] asm_roof_holder001
  Group = -> [roof_holder,Hex_socket_countersunk_head_screw_ISO_10642_M5_15_0,Hex_socket_countersunk_head_screw_ISO_10642_M5_15_003]
  LinkedObject = -> <external roof_holder_asm.FCStd>#Assembly
  Origin = -> Origin002
  Placement = pos=(280.572,210.004,570.1) rot=(1,0,0;1.5708rad)
  Rigid = true
FEATURE [App::FeaturePython] Joint035  label="Fixed028"  # Assembly joint (typed FeaturePython)
  Activated = true
  AngleMax = 0
  AngleMin = 0
  Detach1 = false
  Detach2 = false
  Distance = 0
  Distance2 = 0
  EnableAngleMax = false
  EnableAngleMin = false
  EnableLengthMax = false
  EnableLengthMin = false
  JointType = 0 (Fixed)
  LengthMax = 0
  LengthMin = 0
  Placement1 = pos=(-12,0,4) rot=(0,0,1;0rad)
  Placement2 = pos=(0,0,2.8) rot=(0,0,1;0rad)
  Reference1 = -> Assembly [asm_roof_holder.roof_holder001.Edge21,asm_roof_holder.roof_holder001.Edge21]
  Reference2 = -> Assembly [asm_roof_holder.Hex_socket_countersunk_head_screw_ISO_10642_M5_15_002.Edge1,asm_roof_holder.Hex_socket_countersunk_head_screw_ISO_10642_M5_15_002.Edge1]
FEATURE [App::FeaturePython] Joint036  label="Fixed029"  # Assembly joint (typed FeaturePython)
  Activated = true
  AngleMax = 0
  AngleMin = 0
  Detach1 = false
  Detach2 = false
  Distance = 0
  Distance2 = 0
  EnableAngleMax = false
  EnableAngleMin = false
  EnableLengthMax = false
  EnableLengthMin = false
  JointType = 0 (Fixed)
  LengthMax = 0
  LengthMin = 0
  Placement1 = pos=(0,0,2.8) rot=(0,0,1;0rad)
  Placement2 = pos=(12,0,4) rot=(0,0,1;0rad)
  Reference1 = -> Assembly [asm_roof_holder.Hex_socket_countersunk_head_screw_ISO_10642_M5_15_001.Edge1,asm_roof_holder.Hex_socket_countersunk_head_screw_ISO_10642_M5_15_001.Edge1]
  Reference2 = -> Assembly [asm_roof_holder.roof_holder001.Edge2,asm_roof_holder.roof_holder001.Edge2]
FEATURE [Assembly::JointGroup] Joints001
  Group = -> [Joint035,Joint036]
FEATURE [Assembly::AssemblyLink] asm_roof_holder
  Group = -> [Joints001,roof_holder001,Hex_socket_countersunk_head_screw_ISO_10642_M5_15_001,Hex_socket_countersunk_head_screw_ISO_10642_M5_15_002,Joint035,Joint036]
  LinkedObject = -> <external roof_holder_asm.FCStd>#Assembly
  Origin = -> Origin001
  Rigid = false
FEATURE [App::FeaturePython] Joint037  label="Slider006"  # Assembly joint (typed FeaturePython)
  Activated = true
  AngleMax = 0
  AngleMin = 0
  Detach1 = false
  Detach2 = false
  Distance = 0
  Distance2 = 0
  EnableAngleMax = false
  EnableAngleMin = false
  EnableLengthMax = false
  EnableLengthMin = false
  JointType = 3 (Slider)
  LengthMax = 0
  LengthMin = 0
  Offset2 = pos=(0,0,0) rot=(0,0,1;1.5708rad)
  Placement1 = pos=(0,0,15) rot=(0,0,1;0rad)
  Placement2 = pos=(0,0,0.6) rot=(0,0,1;1.5708rad)
  Reference1 = -> Assembly [asm_roof_holder001.Hex_socket_countersunk_head_screw_ISO_10642_M5_15_003.Edge12,asm_roof_holder001.Hex_socket_countersunk_head_screw_ISO_10642_M5_15_003.Edge12]
  Reference2 = -> Assembly [T_Nut_2020_M007.Edge6,T_Nut_2020_M007.Edge6]
FEATURE [App::FeaturePython] Joint038  label="Slider007"  # Assembly joint (typed FeaturePython)
  Activated = true
  AngleMax = 0
  AngleMin = 0
  Detach1 = false
  Detach2 = false
  Distance = 0
  Distance2 = 0
  EnableAngleMax = false
  EnableAngleMin = false
  EnableLengthMax = false
  EnableLengthMin = false
  JointType = 3 (Slider)
  LengthMax = 0
  LengthMin = 0
  Placement1 = pos=(0,0,15) rot=(0,0,1;0rad)
  Placement2 = pos=(0,0,0.6) rot=(0,0,1;0rad)
  Reference1 = -> Assembly [asm_roof_holder001.Hex_socket_countersunk_head_screw_ISO_10642_M5_15_0.Edge12,asm_roof_holder001.Hex_socket_countersunk_head_screw_ISO_10642_M5_15_0.Edge12]
  Reference2 = -> Assembly [T_Nut_2020_M008.Edge6,T_Nut_2020_M008.Edge6]
FEATURE [App::Link] T_Nut_2020_M009  label="T-Nut_2020_M009"
  LinkPlacement = pos=(323.367,8,570.1) rot=(-0.57735,0.57735,0.57735;2.0944rad)
  LinkedObject = -> <external ../parts/T-nut_20.FCStd>#Part__Feature
  Placement = pos=(323.367,8,570.1) rot=(-0.57735,0.57735,0.57735;2.0944rad)
FEATURE [App::Link] T_Nut_2020_M010  label="T-Nut_2020_M010"
  LinkPlacement = pos=(347.367,8,570.1) rot=(-0.57735,0.57735,0.57735;2.0944rad)
  LinkedObject = -> <external ../parts/T-nut_20.FCStd>#Part__Feature
  Placement = pos=(347.367,8,570.1) rot=(-0.57735,0.57735,0.57735;2.0944rad)
FEATURE [App::FeaturePython] Joint039  label="Slider008"  # Assembly joint (typed FeaturePython)
  Activated = true
  AngleMax = 0
  AngleMin = 0
  Detach1 = false
  Detach2 = false
  Distance = 0
  Distance2 = 0
  EnableAngleMax = false
  EnableAngleMin = false
  EnableLengthMax = false
  EnableLengthMin = false
  JointType = 3 (Slider)
  LengthMax = 0
  LengthMin = 0
  Offset2 = pos=(0,0,0) rot=(0,0,-1;1.5708rad)
  Placement1 = pos=(-3.1,8,400) rot=(0,1,0;3.14159rad)
  Placement2 = pos=(-3,0,0) rot=(0,-0.707107,0.707107;3.14159rad)
  Reference1 = -> Assembly [Tslot20_len.Edge42,Tslot20_len.Vertex40]
  Reference2 = -> Assembly [T_Nut_2020_M009.Edge27,T_Nut_2020_M009.Edge27]
FEATURE [App::FeaturePython] Joint040  label="Slider009"  # Assembly joint (typed FeaturePython)
  Activated = true
  AngleMax = 0
  AngleMin = 0
  Detach1 = false
  Detach2 = false
  Distance = 0
  Distance2 = 0
  EnableAngleMax = false
  EnableAngleMin = false
  EnableLengthMax = false
  EnableLengthMin = false
  JointType = 3 (Slider)
  LengthMax = 0
  LengthMin = 0
  Offset2 = pos=(0,0,0) rot=(0,0,-1;1.5708rad)
  Placement1 = pos=(-3.1,8,400) rot=(0,1,0;3.14159rad)
  Placement2 = pos=(-3,5.25,-7.1e-15) rot=(0,-0.707107,0.707107;3.14159rad)
  Reference1 = -> Assembly [Tslot20_len.Edge42,Tslot20_len.Vertex40]
  Reference2 = -> Assembly [T_Nut_2020_M010.Edge27,T_Nut_2020_M010.Vertex10]
FEATURE [App::Link] roof_holder002
  LinkedObject = -> <external roof_holder_asm.FCStd>#roof_holder
FEATURE [App::Link] Hex_socket_countersunk_head_screw_ISO_10642_M5_15_004  label="Hex socket countersunk head screw ISO 10642 M5 15.005"
  LinkPlacement = pos=(12,7e-16,6.8) rot=(1,0,0;3.14159rad)
  LinkedObject = -> <external roof_holder_asm.FCStd>#Hex_socket_countersunk_head_screw_ISO_10642_M5_15_0
  Placement = pos=(12,7e-16,6.8) rot=(1,0,0;3.14159rad)
FEATURE [App::Link] Hex_socket_countersunk_head_screw_ISO_10642_M5_15_005  label="Hex socket countersunk head screw ISO 10642 M5 15.006"
  LinkPlacement = pos=(-12,7e-16,6.8) rot=(1,0,0;3.14159rad)
  LinkedObject = -> <external roof_holder_asm.FCStd>#Hex_socket_countersunk_head_screw_ISO_10642_M5_15_001
  Placement = pos=(-12,7e-16,6.8) rot=(1,0,0;3.14159rad)
FEATURE [Assembly::AssemblyLink] asm_roof_holder002
  Group = -> [roof_holder002,Hex_socket_countersunk_head_screw_ISO_10642_M5_15_004,Hex_socket_countersunk_head_screw_ISO_10642_M5_15_005]
  LinkedObject = -> <external roof_holder_asm.FCStd>#Assembly
  Origin = -> Origin003
  Placement = pos=(335.367,10.0091,570.1) rot=(1,0,0;4.71239rad)
  Rigid = true
FEATURE [App::FeaturePython] Joint041  label="Slider010"  # Assembly joint (typed FeaturePython)
  Activated = true
  AngleMax = 0
  AngleMin = 0
  Detach1 = false
  Detach2 = false
  Distance = 0
  Distance2 = 0
  EnableAngleMax = false
  EnableAngleMin = false
  EnableLengthMax = false
  EnableLengthMin = false
  JointType = 3 (Slider)
  LengthMax = 0
  LengthMin = 0
  Offset2 = pos=(0,0,0) rot=(0,0,-1;1.5708rad)
  Placement1 = pos=(0,0,15) rot=(0,0,1;0rad)
  Placement2 = pos=(0,0,0.6) rot=(0,0,1;4.71239rad)
  Reference1 = -> Assembly [asm_roof_holder002.Hex_socket_countersunk_head_screw_ISO_10642_M5_15_004.Edge12,asm_roof_holder002.Hex_socket_countersunk_head_screw_ISO_10642_M5_15_004.Edge12]
  Reference2 = -> Assembly [T_Nut_2020_M010.Edge6,T_Nut_2020_M010.Edge6]
FEATURE [App::FeaturePython] Joint042  label="Slider011"  # Assembly joint (typed FeaturePython)
  Activated = true
  AngleMax = 0
  AngleMin = 0
  Detach1 = false
  Detach2 = false
  Distance = 0
  Distance2 = 0
  EnableAngleMax = false
  EnableAngleMin = false
  EnableLengthMax = false
  EnableLengthMin = false
  JointType = 3 (Slider)
  LengthMax = 0
  LengthMin = 0
  Placement1 = pos=(0,0,0.6) rot=(0,0,1;0rad)
  Placement2 = pos=(0,0,15) rot=(0,0,1;0rad)
  Reference1 = -> Assembly [T_Nut_2020_M009.Edge6,T_Nut_2020_M009.Edge6]
  Reference2 = -> Assembly [asm_roof_holder002.Hex_socket_countersunk_head_screw_ISO_10642_M5_15_005.Edge12,asm_roof_holder002.Hex_socket_countersunk_head_screw_ISO_10642_M5_15_005.Edge12]
FEATURE [App::Link] T_Nut_2020_M011  label="T-Nut_2020_M011"
  LinkPlacement = pos=(147.943,8,570.1) rot=(-0.57735,0.57735,0.57735;2.0944rad)
  LinkedObject = -> <external ../parts/T-nut_20.FCStd>#Part__Feature
  Placement = pos=(147.943,8,570.1) rot=(-0.57735,0.57735,0.57735;2.0944rad)
FEATURE [App::Link] T_Nut_2020_M012  label="T-Nut_2020_M012"
  LinkPlacement = pos=(171.943,8,570.1) rot=(-0.57735,0.57735,0.57735;2.0944rad)
  LinkedObject = -> <external ../parts/T-nut_20.FCStd>#Part__Feature
  Placement = pos=(171.943,8,570.1) rot=(-0.57735,0.57735,0.57735;2.0944rad)
FEATURE [App::FeaturePython] Joint043  label="Slider012"  # Assembly joint (typed FeaturePython)
  Activated = true
  AngleMax = 0
  AngleMin = 0
  Detach1 = false
  Detach2 = false
  Distance = 0
  Distance2 = 0
  EnableAngleMax = false
  EnableAngleMin = false
  EnableLengthMax = false
  EnableLengthMin = false
  JointType = 3 (Slider)
  LengthMax = 0
  LengthMin = 0
  Offset2 = pos=(0,0,0) rot=(0,0,-1;1.5708rad)
  Placement1 = pos=(-3,0,0) rot=(-0.57735,-0.57735,0.57735;4.18879rad)
  Placement2 = pos=(-3.1,8,1.8e-15) rot=(-0.707107,0.707107,0;3.14159rad)
  Reference1 = -> Assembly [T_Nut_2020_M012.Edge27,T_Nut_2020_M012.Edge27]
  Reference2 = -> Assembly [Tslot20_len.Edge42,Tslot20_len.Vertex30]
FEATURE [App::FeaturePython] Joint044  label="Slider013"  # Assembly joint (typed FeaturePython)
  Activated = true
  AngleMax = 0
  AngleMin = 0
  Detach1 = false
  Detach2 = false
  Distance = 0
  Distance2 = 0
  EnableAngleMax = false
  EnableAngleMin = false
  EnableLengthMax = false
  EnableLengthMin = false
  JointType = 3 (Slider)
  LengthMax = 0
  LengthMin = 0
  Offset2 = pos=(0,0,0) rot=(0,0,-1;1.5708rad)
  Placement1 = pos=(-3,0,0) rot=(-0.57735,-0.57735,0.57735;4.18879rad)
  Placement2 = pos=(-3.1,8,1.8e-15) rot=(-0.707107,0.707107,0;3.14159rad)
  Reference1 = -> Assembly [T_Nut_2020_M011.Edge27,T_Nut_2020_M011.Edge27]
  Reference2 = -> Assembly [Tslot20_len.Edge42,Tslot20_len.Vertex30]
FEATURE [App::Link] roof_holder003
  LinkedObject = -> <external roof_holder_asm.FCStd>#roof_holder
FEATURE [App::Link] Hex_socket_countersunk_head_screw_ISO_10642_M5_15_006  label="Hex socket countersunk head screw ISO 10642 M5 15.007"
  LinkPlacement = pos=(12,7e-16,6.8) rot=(1,0,0;3.14159rad)
  LinkedObject = -> <external roof_holder_asm.FCStd>#Hex_socket_countersunk_head_screw_ISO_10642_M5_15_0
  Placement = pos=(12,7e-16,6.8) rot=(1,0,0;3.14159rad)
FEATURE [App::Link] Hex_socket_countersunk_head_screw_ISO_10642_M5_15_007  label="Hex socket countersunk head screw ISO 10642 M5 15.008"
  LinkPlacement = pos=(-12,7e-16,6.8) rot=(1,0,0;3.14159rad)
  LinkedObject = -> <external roof_holder_asm.FCStd>#Hex_socket_countersunk_head_screw_ISO_10642_M5_15_001
  Placement = pos=(-12,7e-16,6.8) rot=(1,0,0;3.14159rad)
FEATURE [Assembly::AssemblyLink] asm_roof_holder003
  Group = -> [roof_holder003,Hex_socket_countersunk_head_screw_ISO_10642_M5_15_006,Hex_socket_countersunk_head_screw_ISO_10642_M5_15_007]
  LinkedObject = -> <external roof_holder_asm.FCStd>#Assembly
  Origin = -> Origin004
  Placement = pos=(159.943,10.0097,570.1) rot=(-1,0,0;1.5708rad)
  Rigid = true
FEATURE [App::FeaturePython] Joint045  label="Slider014"  # Assembly joint (typed FeaturePython)
  Activated = true
  AngleMax = 0
  AngleMin = 0
  Detach1 = false
  Detach2 = false
  Distance = 0
  Distance2 = 0
  EnableAngleMax = false
  EnableAngleMin = false
  EnableLengthMax = false
  EnableLengthMin = false
  JointType = 3 (Slider)
  LengthMax = 0
  LengthMin = 0
  Offset2 = pos=(0,0,0) rot=(0,0,-1;1.5708rad)
  Placement1 = pos=(0,0,15) rot=(0,0,1;0rad)
  Placement2 = pos=(0,0,0.6) rot=(0,0,1;4.71239rad)
  Reference1 = -> Assembly [asm_roof_holder003.Hex_socket_countersunk_head_screw_ISO_10642_M5_15_006.Edge12,asm_roof_holder003.Hex_socket_countersunk_head_screw_ISO_10642_M5_15_006.Edge12]
  Reference2 = -> Assembly [T_Nut_2020_M012.Edge6,T_Nut_2020_M012.Edge6]
FEATURE [App::FeaturePython] Joint046  label="Slider015"  # Assembly joint (typed FeaturePython)
  Activated = true
  AngleMax = 0
  AngleMin = 0
  Detach1 = false
  Detach2 = false
  Distance = 0
  Distance2 = 0
  EnableAngleMax = false
  EnableAngleMin = false
  EnableLengthMax = false
  EnableLengthMin = false
  JointType = 3 (Slider)
  LengthMax = 0
  LengthMin = 0
  Placement1 = pos=(0,0,15) rot=(0,0,1;0rad)
  Placement2 = pos=(0,0,0.6) rot=(0,0,1;0rad)
  Reference1 = -> Assembly [asm_roof_holder003.Hex_socket_countersunk_head_screw_ISO_10642_M5_15_007.Edge12,asm_roof_holder003.Hex_socket_countersunk_head_screw_ISO_10642_M5_15_007.Edge12]
  Reference2 = -> Assembly [T_Nut_2020_M011.Edge6,T_Nut_2020_M011.Edge6]
FEATURE [App::Link] T_Nut_2020_M013  label="T-Nut_2020_M013"
  LinkPlacement = pos=(428,0.1,77.758) rot=(-0.57735,0.57735,-0.57735;2.0944rad)
  LinkedObject = -> <external ../parts/T-nut_20.FCStd>#Part__Feature
  Placement = pos=(428,0.1,77.758) rot=(-0.57735,0.57735,-0.57735;2.0944rad)
FEATURE [App::FeaturePython] Joint048  label="Slider017"  # Assembly joint (typed FeaturePython)
  Activated = true
  AngleMax = 0
  AngleMin = 0
  Detach1 = false
  Detach2 = false
  Distance = 0
  Distance2 = 0
  EnableAngleMax = false
  EnableAngleMin = false
  EnableLengthMax = false
  EnableLengthMin = false
  JointType = 3 (Slider)
  LengthMax = 0
  LengthMin = 0
  Offset2 = pos=(0,0,0) rot=(0,0,1;3.14159rad)
  Placement1 = pos=(-3,0,0) rot=(-0.57735,-0.57735,0.57735;4.18879rad)
  Placement2 = pos=(8,3.1,0) rot=(0,0,1;3.14159rad)
  Reference1 = -> Assembly [T_Nut_2020_M013.Edge27,T_Nut_2020_M013.Edge27]
  Reference2 = -> Assembly [Tslot20_heigh001.Edge95,Tslot20_heigh001.Vertex21]
FEATURE [App::Link] T_Nut_2020_M014  label="T-Nut_2020_M014"
  LinkPlacement = pos=(428,219.9,77.1229) rot=(-0.57735,0.57735,-0.57735;2.0944rad)
  LinkedObject = -> <external ../parts/T-nut_20.FCStd>#Part__Feature
  Placement = pos=(428,219.9,77.1229) rot=(-0.57735,0.57735,-0.57735;2.0944rad)
FEATURE [App::FeaturePython] Joint049  label="Slider018"  # Assembly joint (typed FeaturePython)
  Activated = true
  AngleMax = 0
  AngleMin = 0
  Detach1 = false
  Detach2 = false
  Distance = 0
  Distance2 = 0
  EnableAngleMax = false
  EnableAngleMin = false
  EnableLengthMax = false
  EnableLengthMin = false
  JointType = 3 (Slider)
  LengthMax = 0
  LengthMin = 0
  Offset2 = pos=(0,0,0) rot=(0,0,1;3.14159rad)
  Placement1 = pos=(3,-5.25,0) rot=(-0.57735,-0.57735,0.57735;4.18879rad)
  Placement2 = pos=(8,-3.1,0) rot=(0,0,1;3.14159rad)
  Reference1 = -> Assembly [T_Nut_2020_M014.Edge8,T_Nut_2020_M014.Vertex8]
  Reference2 = -> Assembly [Tslot20_heigh003.Edge90,Tslot20_heigh003.Vertex16]
FEATURE [App::Link] plate_roof001  label="plate_roof"
  LinkedObject = -> <external asm_roof.FCStd>#plate_roof001
FEATURE [App::Link] linear_slide  label="linear_slide_12"
  LinkPlacement = pos=(-38,-53.8,-16.3253) rot=(0,0,1;0rad)
  LinkedObject = -> <external asm_roof.FCStd>#linear_slide
  Placement = pos=(-38,-53.8,-16.3253) rot=(0,0,1;0rad)
FEATURE [App::Link] linear_slide001  label="linear_slide_12_001"
  LinkPlacement = pos=(38,-53.8,-16.3253) rot=(0,0,1;0rad)
  LinkedObject = -> <external asm_roof.FCStd>#linear_slide001
  Placement = pos=(38,-53.8,-16.3253) rot=(0,0,1;0rad)
FEATURE [App::Link] SHF12
  LinkedObject = -> <external asm_shf.FCStd>#SHF12
FEATURE [App::Link] Hex_socket_head_cap_screw_DIN_912_M4_15_0  label="Hex socket head cap screw DIN 912 M4 15.0"
  LinkPlacement = pos=(12.25,6.5,11.5) rot=(0,-1,0;1.5708rad)
  LinkedObject = -> <external asm_shf.FCStd>#Hex_socket_head_cap_screw_DIN_912_M4_15_0
  Placement = pos=(12.25,6.5,11.5) rot=(0,-1,0;1.5708rad)
FEATURE [App::Link] Hex_socket_head_cap_screw_DIN_912_M5_15_0  label="Hex socket head cap screw DIN 912 M5 15.0"
  LinkPlacement = pos=(18,11,1.16e-14) rot=(0.57735,-0.57735,0.57735;2.0944rad)
  LinkedObject = -> <external asm_shf.FCStd>#Hex_socket_head_cap_screw_DIN_912_M5_15_0
  Placement = pos=(18,11,1.16e-14) rot=(0.57735,-0.57735,0.57735;2.0944rad)
FEATURE [App::Link] Hex_socket_head_cap_screw_DIN_912_M5_15_001  label="Hex socket head cap screw DIN 912 M5 15.001"
  LinkPlacement = pos=(-18,11,1.16e-14) rot=(0.57735,-0.57735,0.57735;2.0944rad)
  LinkedObject = -> <external asm_shf.FCStd>#Hex_socket_head_cap_screw_DIN_912_M5_15_001
  Placement = pos=(-18,11,1.16e-14) rot=(0.57735,-0.57735,0.57735;2.0944rad)
FEATURE [Assembly::AssemblyLink] asm_SHF002
  Group = -> [SHF12,Hex_socket_head_cap_screw_DIN_912_M4_15_0,Hex_socket_head_cap_screw_DIN_912_M5_15_0,Hex_socket_head_cap_screw_DIN_912_M5_15_001]
  LinkedObject = -> <external asm_roof.FCStd>#asm_SHF002
  Placement = pos=(-38,-53.8,4e-15) rot=(0.57735,-0.57735,0.57735;4.18879rad)
  Rigid = true
FEATURE [App::Link] SHF013
  LinkedObject = -> <external asm_shf.FCStd>#SHF12
FEATURE [App::Link] Hex_socket_head_cap_screw_DIN_912_M4_15_001  label="Hex socket head cap screw DIN 912 M4 15.001"
  LinkPlacement = pos=(12.25,6.5,11.5) rot=(0,-1,0;1.5708rad)
  LinkedObject = -> <external asm_shf.FCStd>#Hex_socket_head_cap_screw_DIN_912_M4_15_0
  Placement = pos=(12.25,6.5,11.5) rot=(0,-1,0;1.5708rad)
FEATURE [App::Link] Hex_socket_head_cap_screw_DIN_912_M5_15_002  label="Hex socket head cap screw DIN 912 M5 15.002"
  LinkPlacement = pos=(18,11,1.16e-14) rot=(0.57735,-0.57735,0.57735;2.0944rad)
  LinkedObject = -> <external asm_shf.FCStd>#Hex_socket_head_cap_screw_DIN_912_M5_15_0
  Placement = pos=(18,11,1.16e-14) rot=(0.57735,-0.57735,0.57735;2.0944rad)
FEATURE [App::Link] Hex_socket_head_cap_screw_DIN_912_M5_15_003  label="Hex socket head cap screw DIN 912 M5 15.003"
  LinkPlacement = pos=(-18,11,1.16e-14) rot=(0.57735,-0.57735,0.57735;2.0944rad)
  LinkedObject = -> <external asm_shf.FCStd>#Hex_socket_head_cap_screw_DIN_912_M5_15_001
  Placement = pos=(-18,11,1.16e-14) rot=(0.57735,-0.57735,0.57735;2.0944rad)
FEATURE [Assembly::AssemblyLink] asm_SHF003
  Group = -> [SHF013,Hex_socket_head_cap_screw_DIN_912_M4_15_001,Hex_socket_head_cap_screw_DIN_912_M5_15_002,Hex_socket_head_cap_screw_DIN_912_M5_15_003]
  LinkedObject = -> <external asm_roof.FCStd>#asm_SHF003
  Placement = pos=(38,-53.8,4e-15) rot=(0.57735,-0.57735,0.57735;4.18879rad)
  Rigid = true
FEATURE [App::Link] asm_cam_holder
  LinkPlacement = pos=(0,-53.8,64.6747) rot=(0,0,1;1.5708rad)
  LinkedObject = -> <external asm_roof.FCStd>#asm_cam_holder
  Placement = pos=(0,-53.8,64.6747) rot=(0,0,1;1.5708rad)
FEATURE [Assembly::AssemblyLink] asm_roof
  Group = -> [plate_roof001,linear_slide,linear_slide001,asm_SHF002,asm_SHF003,asm_cam_holder]
  LinkedObject = -> <external asm_roof.FCStd>#Assembly
  Origin = -> Origin005
  Placement = pos=(210,110,764.828) rot=(0.707107,0.707107,0;3.14159rad)
  Rigid = true
FEATURE [App::FeaturePython] Joint050  label="Slider019"  # Assembly joint (typed FeaturePython)
  Activated = true
  AngleMax = 0
  AngleMin = 0
  Detach1 = false
  Detach2 = false
  Distance = 0
  Distance2 = 0
  EnableAngleMax = false
  EnableAngleMin = false
  EnableLengthMax = true
  EnableLengthMin = true
  JointType = 3 (Slider)
  LengthMax = 226.58
  LengthMin = 11.7049
  Placement1 = pos=(100,-200,1.5) rot=(0,0,1;0rad)
  Placement2 = pos=(-3.1,10,200) rot=(0.707107,0,0.707107;3.14159rad)
  Reference1 = -> Assembly [asm_roof.plate_roof001.Edge5,asm_roof.plate_roof001.Edge5]
  Reference2 = -> Assembly [Tslot20_wid.Edge3,Tslot20_wid.Vertex3]
FEATURE [App::Link] plate_front_back
  LinkedObject = -> <external asm_plate_front_back.FCStd>#plate_front_back
FEATURE [App::Link] Hex_screw_M5_10_001  label="Hex screw M5 10.001"
  LinkPlacement = pos=(-103.013,204.442,-7) rot=(0,0,1;0rad)
  LinkedObject = -> <external asm_plate_front_back.FCStd>#Hex_screw_M5_10_001
  Placement = pos=(-103.013,204.442,-7) rot=(0,0,1;0rad)
FEATURE [App::Link] Hex_screw_M5_10_002  label="Hex screw M5 10.002"
  LinkPlacement = pos=(116.987,204.442,-7) rot=(0,0,1;0rad)
  LinkedObject = -> <external asm_plate_front_back.FCStd>#Hex_screw_M5_10_002
  Placement = pos=(116.987,204.442,-7) rot=(0,0,1;0rad)
FEATURE [App::Link] Hex_screw_M5_10_003  label="Hex screw M5 10.003"
  LinkPlacement = pos=(116.987,-275.558,-7) rot=(0,0,1;0rad)
  LinkedObject = -> <external asm_plate_front_back.FCStd>#Hex_screw_M5_10_003
  Placement = pos=(116.987,-275.558,-7) rot=(0,0,1;0rad)
FEATURE [App::Link] Hex_screw_M5_10_0  label="Hex screw M5 10.0"
  LinkPlacement = pos=(-103.013,-275.558,-7) rot=(0,0,1;0rad)
  LinkedObject = -> <external asm_plate_front_back.FCStd>#Hex_screw_M5_10_0
  Placement = pos=(-103.013,-275.558,-7) rot=(0,0,1;0rad)
FEATURE [Assembly::AssemblyLink] asm_plate_front_back
  Group = -> [plate_front_back,Hex_screw_M5_10_001,Hex_screw_M5_10_002,Hex_screw_M5_10_003,Hex_screw_M5_10_0]
  LinkedObject = -> <external asm_plate_front_back.FCStd>#Assembly
  Origin = -> Origin006
  Placement = pos=(-10,109.9,299.985) rot=(0.57735,0.57735,-0.57735;4.18879rad)
  Rigid = true
FEATURE [App::Link] T_Nut_2020_M015  label="T-Nut_2020_M015"
  LinkPlacement = pos=(428,219.9,547.156) rot=(0.57735,0.57735,0.57735;2.0944rad)
  LinkedObject = -> <external ../parts/T-nut_20.FCStd>#Part__Feature
  Placement = pos=(428,219.9,547.156) rot=(0.57735,0.57735,0.57735;2.0944rad)
FEATURE [App::Link] T_Nut_2020_M016  label="T-Nut_2020_M016"
  LinkPlacement = pos=(428,0.1,539.806) rot=(0.57735,0.57735,0.57735;2.0944rad)
  LinkedObject = -> <external ../parts/T-nut_20.FCStd>#Part__Feature
  Placement = pos=(428,0.1,539.806) rot=(0.57735,0.57735,0.57735;2.0944rad)
FEATURE [App::FeaturePython] Joint051  label="Slider020"  # Assembly joint (typed FeaturePython)
  Activated = true
  AngleMax = 0
  AngleMin = 0
  Detach1 = false
  Detach2 = false
  Distance = 0
  Distance2 = 0
  EnableAngleMax = false
  EnableAngleMin = false
  EnableLengthMax = false
  EnableLengthMin = false
  JointType = 3 (Slider)
  LengthMax = 0
  LengthMin = 0
  Offset2 = pos=(0,0,0) rot=(0,0,1;3.14159rad)
  Placement1 = pos=(-3,0,0) rot=(-0.57735,-0.57735,0.57735;4.18879rad)
  Placement2 = pos=(8,-3.1,580) rot=(0,0,1;3.14159rad)
  Reference1 = -> Assembly [T_Nut_2020_M015.Edge27,T_Nut_2020_M015.Edge27]
  Reference2 = -> Assembly [Tslot20_heigh003.Edge90,Tslot20_heigh003.Vertex52]
FEATURE [App::FeaturePython] Joint052  label="Slider021"  # Assembly joint (typed FeaturePython)
  Activated = true
  AngleMax = 0
  AngleMin = 0
  Detach1 = false
  Detach2 = false
  Distance = 0
  Distance2 = 0
  EnableAngleMax = false
  EnableAngleMin = false
  EnableLengthMax = false
  EnableLengthMin = false
  JointType = 3 (Slider)
  LengthMax = 0
  LengthMin = 0
  Offset2 = pos=(0,0,0) rot=(0,0,1;3.14159rad)
  Placement1 = pos=(3,0,0) rot=(-0.57735,-0.57735,0.57735;4.18879rad)
  Placement2 = pos=(8,3.1,580) rot=(0,0,1;3.14159rad)
  Reference1 = -> Assembly [T_Nut_2020_M016.Edge8,T_Nut_2020_M016.Edge8]
  Reference2 = -> Assembly [Tslot20_heigh001.Edge95,Tslot20_heigh001.Vertex57]
FEATURE [App::Link] plate_front_back001
  LinkedObject = -> <external asm_plate_front_back.FCStd>#plate_front_back
FEATURE [App::Link] Hex_screw_M5_10_004  label="Hex screw M5 10.004"
  LinkPlacement = pos=(-103.013,204.442,-7) rot=(0,0,1;0rad)
  LinkedObject = -> <external asm_plate_front_back.FCStd>#Hex_screw_M5_10_001
  Placement = pos=(-103.013,204.442,-7) rot=(0,0,1;0rad)
FEATURE [App::Link] Hex_screw_M5_10_005  label="Hex screw M5 10.005"
  LinkPlacement = pos=(116.987,204.442,-7) rot=(0,0,1;0rad)
  LinkedObject = -> <external asm_plate_front_back.FCStd>#Hex_screw_M5_10_002
  Placement = pos=(116.987,204.442,-7) rot=(0,0,1;0rad)
FEATURE [App::Link] Hex_screw_M5_10_006  label="Hex screw M5 10.006"
  LinkPlacement = pos=(116.987,-275.558,-7) rot=(0,0,1;0rad)
  LinkedObject = -> <external asm_plate_front_back.FCStd>#Hex_screw_M5_10_003
  Placement = pos=(116.987,-275.558,-7) rot=(0,0,1;0rad)
FEATURE [App::Link] Hex_screw_M5_10_007  label="Hex screw M5 10.007"
  LinkPlacement = pos=(-103.013,-275.558,-7) rot=(0,0,1;0rad)
  LinkedObject = -> <external asm_plate_front_back.FCStd>#Hex_screw_M5_10_0
  Placement = pos=(-103.013,-275.558,-7) rot=(0,0,1;0rad)
FEATURE [Assembly::AssemblyLink] asm_plate_front_back001
  Group = -> [plate_front_back001,Hex_screw_M5_10_004,Hex_screw_M5_10_005,Hex_screw_M5_10_006,Hex_screw_M5_10_007]
  LinkedObject = -> <external asm_plate_front_back.FCStd>#Assembly
  Origin = -> Origin007
  Placement = pos=(430,110.1,299.806) rot=(0.57735,0.57735,0.57735;2.0944rad)
  Rigid = true
FEATURE [App::FeaturePython] Joint053  label="Fixed030"  # Assembly joint (typed FeaturePython)
  Activated = true
  AngleMax = 0
  AngleMin = 0
  Detach1 = false
  Detach2 = false
  Distance = 0
  Distance2 = 0
  EnableAngleMax = false
  EnableAngleMin = false
  EnableLengthMax = false
  EnableLengthMin = false
  JointType = 0 (Fixed)
  LengthMax = 0
  LengthMin = 0
  Offset2 = pos=(0,0,-5.6) rot=(0,0,1;0rad)
  Placement1 = pos=(-6.98683,35.5575,0) rot=(0,0,1;0rad)
  Placement2 = pos=(-1.7e-15,-6.2e-15,-5) rot=(0,0,1;0rad)
  Reference1 = -> Assembly [asm_plate_front_back001.Hex_screw_M5_10_004.Edge2,asm_plate_front_back001.Hex_screw_M5_10_004.Edge2]
  Reference2 = -> Assembly [T_Nut_2020_M016.Edge6,T_Nut_2020_M016.Edge6]
FEATURE [App::Link] T_Nut_2020_M017  label="T-Nut_2020_M017"
  LinkPlacement = pos=(-8,219.9,539.985) rot=(0.57735,0.57735,-0.57735;4.18879rad)
  LinkedObject = -> <external ../parts/T-nut_20.FCStd>#Part__Feature
  Placement = pos=(-8,219.9,539.985) rot=(0.57735,0.57735,-0.57735;4.18879rad)
FEATURE [App::Link] T_Nut_2020_M018  label="T-Nut_2020_M018"
  LinkPlacement = pos=(-8,0.1,46.76) rot=(0.57735,-0.57735,-0.57735;2.0944rad)
  LinkedObject = -> <external ../parts/T-nut_20.FCStd>#Part__Feature
  Placement = pos=(-8,0.1,46.76) rot=(0.57735,-0.57735,-0.57735;2.0944rad)
FEATURE [App::Link] T_Nut_2020_M019  label="T-Nut_2020_M019"
  LinkPlacement = pos=(-8,219.9,55.7454) rot=(0.57735,0.57735,-0.57735;4.18879rad)
  LinkedObject = -> <external ../parts/T-nut_20.FCStd>#Part__Feature
  Placement = pos=(-8,219.9,55.7454) rot=(0.57735,0.57735,-0.57735;4.18879rad)
FEATURE [App::Link] T_Nut_2020_M020  label="T-Nut_2020_M020"
  LinkPlacement = pos=(-8,0.1,573.051) rot=(0.57735,0.57735,-0.57735;4.18879rad)
  LinkedObject = -> <external ../parts/T-nut_20.FCStd>#Part__Feature
  Placement = pos=(-8,0.1,573.051) rot=(0.57735,0.57735,-0.57735;4.18879rad)
FEATURE [App::FeaturePython] Joint054  label="Slider022"  # Assembly joint (typed FeaturePython)
  Activated = true
  AngleMax = 0
  AngleMin = 0
  Detach1 = false
  Detach2 = false
  Distance = 0
  Distance2 = 0
  EnableAngleMax = false
  EnableAngleMin = false
  EnableLengthMax = false
  EnableLengthMin = false
  JointType = 3 (Slider)
  LengthMax = 0
  LengthMin = 0
  Placement1 = pos=(-3,0,0) rot=(-0.57735,-0.57735,0.57735;4.18879rad)
  Placement2 = pos=(-8,-3.1,0) rot=(0,0,1;0rad)
  Reference1 = -> Assembly [T_Nut_2020_M019.Edge27,T_Nut_2020_M019.Edge27]
  Reference2 = -> Assembly [Tslot20_heigh002.Edge109,Tslot20_heigh002.Vertex37]
FEATURE [App::FeaturePython] Joint055  label="Slider023"  # Assembly joint (typed FeaturePython)
  Activated = true
  AngleMax = 0
  AngleMin = 0
  Detach1 = false
  Detach2 = false
  Distance = 0
  Distance2 = 0
  EnableAngleMax = false
  EnableAngleMin = false
  EnableLengthMax = false
  EnableLengthMin = false
  JointType = 3 (Slider)
  LengthMax = 0
  LengthMin = 0
  Placement1 = pos=(-3,0,0) rot=(-0.57735,-0.57735,0.57735;4.18879rad)
  Placement2 = pos=(-8,3.1,0) rot=(0,0,1;0rad)
  Reference1 = -> Assembly [T_Nut_2020_M018.Edge27,T_Nut_2020_M018.Edge27]
  Reference2 = -> Assembly [Tslot20_heigh.Edge104,Tslot20_heigh.Vertex32]
FEATURE [App::FeaturePython] Joint056  label="Slider024"  # Assembly joint (typed FeaturePython)
  Activated = true
  AngleMax = 0
  AngleMin = 0
  Detach1 = false
  Detach2 = false
  Distance = 0
  Distance2 = 0
  EnableAngleMax = false
  EnableAngleMin = false
  EnableLengthMax = false
  EnableLengthMin = false
  JointType = 3 (Slider)
  LengthMax = 0
  LengthMin = 0
  Placement1 = pos=(3,5.25,-7.1e-15) rot=(-0.57735,-0.57735,0.57735;4.18879rad)
  Placement2 = pos=(-8,3.1,580) rot=(0,0,1;0rad)
  Reference1 = -> Assembly [T_Nut_2020_M020.Edge8,T_Nut_2020_M020.Vertex7]
  Reference2 = -> Assembly [Tslot20_heigh.Edge104,Tslot20_heigh.Vertex67]
FEATURE [App::FeaturePython] Joint057  label="Slider025"  # Assembly joint (typed FeaturePython)
  Activated = true
  AngleMax = 0
  AngleMin = 0
  Detach1 = false
  Detach2 = false
  Distance = 0
  Distance2 = 0
  EnableAngleMax = false
  EnableAngleMin = false
  EnableLengthMax = false
  EnableLengthMin = false
  JointType = 3 (Slider)
  LengthMax = 0
  LengthMin = 0
  Placement1 = pos=(-3,0,0) rot=(-0.57735,-0.57735,0.57735;4.18879rad)
  Placement2 = pos=(-8,-3.1,580) rot=(0,0,1;0rad)
  Reference1 = -> Assembly [T_Nut_2020_M017.Edge27,T_Nut_2020_M017.Edge27]
  Reference2 = -> Assembly [Tslot20_heigh002.Edge109,Tslot20_heigh002.Vertex72]
FEATURE [App::FeaturePython] Joint058  label="Fixed031"  # Assembly joint (typed FeaturePython)
  Activated = true
  AngleMax = 0
  AngleMin = 0
  Detach1 = false
  Detach2 = false
  Distance = 0
  Distance2 = 0
  EnableAngleMax = false
  EnableAngleMin = false
  EnableLengthMax = false
  EnableLengthMin = false
  JointType = 0 (Fixed)
  LengthMax = 0
  LengthMin = 0
  Offset2 = pos=(0,0,-5.6) rot=(0,0,1;0rad)
  Placement1 = pos=(-6.98683,35.5575,0) rot=(0,0,1;0rad)
  Placement2 = pos=(-6e-16,-6.2e-15,-5) rot=(0,0,1;0rad)
  Reference1 = -> Assembly [asm_plate_front_back.Hex_screw_M5_10_003.Edge2,asm_plate_front_back.Hex_screw_M5_10_003.Edge2]
  Reference2 = -> Assembly [T_Nut_2020_M017.Edge6,T_Nut_2020_M017.Edge6]
FEATURE [App::Link] T_Nut_2020_M021  label="T-Nut_2020_M021"
  LinkPlacement = pos=(419.9,228,33.7633) rot=(1,0,0;4.71239rad)
  LinkedObject = -> <external ../parts/T-nut_20.FCStd>#Part__Feature
  Placement = pos=(419.9,228,33.7633) rot=(1,0,0;4.71239rad)
FEATURE [App::Link] T_Nut_2020_M022  label="T-Nut_2020_M022"
  LinkPlacement = pos=(0.1,228,567.313) rot=(-1,0,0;1.5708rad)
  LinkedObject = -> <external ../parts/T-nut_20.FCStd>#Part__Feature
  Placement = pos=(0.1,228,567.313) rot=(-1,0,0;1.5708rad)
FEATURE [App::Link] T_Nut_2020_M023  label="T-Nut_2020_M023"
  LinkPlacement = pos=(419.9,228,549.906) rot=(1,0,0;4.71239rad)
  LinkedObject = -> <external ../parts/T-nut_20.FCStd>#Part__Feature
  Placement = pos=(419.9,228,549.906) rot=(1,0,0;4.71239rad)
FEATURE [App::Link] T_Nut_2020_M024  label="T-Nut_2020_M024"
  LinkPlacement = pos=(0.1,228,59.7123) rot=(1,0,0;4.71239rad)
  LinkedObject = -> <external ../parts/T-nut_20.FCStd>#Part__Feature
  Placement = pos=(0.1,228,59.7123) rot=(1,0,0;4.71239rad)
FEATURE [App::FeaturePython] Joint059  label="Slider026"  # Assembly joint (typed FeaturePython)
  Activated = true
  AngleMax = 0
  AngleMin = 0
  Detach1 = false
  Detach2 = false
  Distance = 0
  Distance2 = 0
  EnableAngleMax = false
  EnableAngleMin = false
  EnableLengthMax = false
  EnableLengthMin = false
  JointType = 3 (Slider)
  LengthMax = 0
  LengthMin = 0
  Offset2 = pos=(0,0,0) rot=(0,0,-1;1.5708rad)
  Placement1 = pos=(3,-7.1e-15,0) rot=(-0.57735,-0.57735,0.57735;4.18879rad)
  Placement2 = pos=(3.1,8,0) rot=(-0.707107,0.707107,0;3.14159rad)
  Reference1 = -> Assembly [T_Nut_2020_M024.Edge8,T_Nut_2020_M024.Edge8]
  Reference2 = -> Assembly [Tslot20_heigh002.Edge99,Tslot20_heigh002.Vertex25]
FEATURE [App::FeaturePython] Joint060  label="Slider027"  # Assembly joint (typed FeaturePython)
  Activated = true
  AngleMax = 0
  AngleMin = 0
  Detach1 = false
  Detach2 = false
  Distance = 0
  Distance2 = 0
  EnableAngleMax = false
  EnableAngleMin = false
  EnableLengthMax = false
  EnableLengthMin = false
  JointType = 3 (Slider)
  LengthMax = 0
  LengthMin = 0
  Offset2 = pos=(0,0,0) rot=(0,0,-1;1.5708rad)
  Placement1 = pos=(-3,0,0) rot=(-0.57735,-0.57735,0.57735;4.18879rad)
  Placement2 = pos=(-3.1,8,0) rot=(-0.707107,0.707107,0;3.14159rad)
  Reference1 = -> Assembly [T_Nut_2020_M021.Edge27,T_Nut_2020_M021.Edge27]
  Reference2 = -> Assembly [Tslot20_heigh003.Edge42,Tslot20_heigh003.Vertex30]
FEATURE [App::FeaturePython] Joint061  label="Slider028"  # Assembly joint (typed FeaturePython)
  Activated = true
  AngleMax = 0
  AngleMin = 0
  Detach1 = false
  Detach2 = false
  Distance = 0
  Distance2 = 0
  EnableAngleMax = false
  EnableAngleMin = false
  EnableLengthMax = false
  EnableLengthMin = false
  JointType = 3 (Slider)
  LengthMax = 0
  LengthMin = 0
  Offset2 = pos=(0,0,0) rot=(0,0,-1;1.5708rad)
  Placement1 = pos=(3,-5.25,0) rot=(-0.57735,-0.57735,0.57735;4.18879rad)
  Placement2 = pos=(3.1,8,580) rot=(-0.707107,0.707107,0;3.14159rad)
  Reference1 = -> Assembly [T_Nut_2020_M022.Edge8,T_Nut_2020_M022.Vertex8]
  Reference2 = -> Assembly [Tslot20_heigh002.Edge99,Tslot20_heigh002.Vertex61]
FEATURE [App::FeaturePython] Joint062  label="Slider029"  # Assembly joint (typed FeaturePython)
  Activated = true
  AngleMax = 0
  AngleMin = 0
  Detach1 = false
  Detach2 = false
  Distance = 0
  Distance2 = 0
  EnableAngleMax = false
  EnableAngleMin = false
  EnableLengthMax = false
  EnableLengthMin = false
  JointType = 3 (Slider)
  LengthMax = 0
  LengthMin = 0
  Offset2 = pos=(0,0,0) rot=(0,0,-1;1.5708rad)
  Placement1 = pos=(-3,0,0) rot=(-0.57735,-0.57735,0.57735;4.18879rad)
  Placement2 = pos=(-3.1,8,580) rot=(-0.707107,0.707107,0;3.14159rad)
  Reference1 = -> Assembly [T_Nut_2020_M023.Edge27,T_Nut_2020_M023.Edge27]
  Reference2 = -> Assembly [Tslot20_heigh003.Edge42,Tslot20_heigh003.Vertex40]
FEATURE [App::Link] plate_side
  LinkedObject = -> <external asm_plate_side.FCStd>#plate_side
FEATURE [App::Link] TAH15_M5_L6  label="TAH15-M5-L6"
  LinkPlacement = pos=(210,240,3) rot=(0.707107,0,-0.707107;3.14159rad)
  LinkedObject = -> <external asm_plate_side.FCStd>#TAH15_M5_L6
  Placement = pos=(210,240,3) rot=(0.707107,0,-0.707107;3.14159rad)
FEATURE [App::Link] TAH15_M5_L007  label="TAH15-M5-L007"
  LinkPlacement = pos=(-210,-240,3) rot=(0.707107,0,-0.707107;3.14159rad)
  LinkedObject = -> <external asm_plate_side.FCStd>#TAH15_M5_L007
  Placement = pos=(-210,-240,3) rot=(0.707107,0,-0.707107;3.14159rad)
FEATURE [App::Link] TAH15_M5_L008  label="TAH15-M5-L008"
  LinkPlacement = pos=(210,-240,3) rot=(0.707107,0,-0.707107;3.14159rad)
  LinkedObject = -> <external asm_plate_side.FCStd>#TAH15_M5_L008
  Placement = pos=(210,-240,3) rot=(0.707107,0,-0.707107;3.14159rad)
FEATURE [App::Link] TAH15_M5_L009  label="TAH15-M5-L009"
  LinkPlacement = pos=(-210,240,3) rot=(0.707107,0,-0.707107;3.14159rad)
  LinkedObject = -> <external asm_plate_side.FCStd>#TAH15_M5_L009
  Placement = pos=(-210,240,3) rot=(0.707107,0,-0.707107;3.14159rad)
FEATURE [Assembly::AssemblyLink] asm_plate_side
  Group = -> [plate_side,TAH15_M5_L6,TAH15_M5_L007,TAH15_M5_L008,TAH15_M5_L009]
  LinkedObject = -> <external asm_plate_side.FCStd>#Assembly
  Origin = -> Origin008
  Placement = pos=(209.9,230.109,299.906) rot=(0,-0.707107,-0.707107;3.14159rad)
  Rigid = true
FEATURE [App::FeaturePython] Joint063  label="Fixed032"  # Assembly joint (typed FeaturePython)
  Activated = true
  AngleMax = 0
  AngleMin = 0
  Detach1 = false
  Detach2 = false
  Distance = 0
  Distance2 = 0
  EnableAngleMax = false
  EnableAngleMin = false
  EnableLengthMax = false
  EnableLengthMin = false
  JointType = 0 (Fixed)
  LengthMax = 0
  LengthMin = 0
  Offset2 = pos=(0,0,-1) rot=(0,0,1;3.14159rad)
  Placement1 = pos=(5.5095,0,0) rot=(0,1,0;1.5708rad)
  Placement2 = pos=(0,-1.1e-15,-0.4) rot=(0,0,-1;3.14159rad)
  Reference1 = -> Assembly [asm_plate_side.TAH15_M5_L009.Edge12,asm_plate_side.TAH15_M5_L009.Edge12]
  Reference2 = -> Assembly [T_Nut_2020_M023.Edge6,T_Nut_2020_M023.Edge6]
FEATURE [App::Link] T_Nut_2020_M025  label="T-Nut_2020_M025"
  LinkPlacement = pos=(0.1,-8,34.5329) rot=(1,0,0;1.5708rad)
  LinkedObject = -> <external ../parts/T-nut_20.FCStd>#Part__Feature
  Placement = pos=(0.1,-8,34.5329) rot=(1,0,0;1.5708rad)
FEATURE [App::Link] T_Nut_2020_M026  label="T-Nut_2020_M026"
  LinkPlacement = pos=(419.9,-8,32.0325) rot=(1,0,0;1.5708rad)
  LinkedObject = -> <external ../parts/T-nut_20.FCStd>#Part__Feature
  Placement = pos=(419.9,-8,32.0325) rot=(1,0,0;1.5708rad)
FEATURE [App::Link] T_Nut_2020_M027  label="T-Nut_2020_M027"
  LinkPlacement = pos=(0.1,-8,549.726) rot=(1,0,0;1.5708rad)
  LinkedObject = -> <external ../parts/T-nut_20.FCStd>#Part__Feature
  Placement = pos=(0.1,-8,549.726) rot=(1,0,0;1.5708rad)
FEATURE [App::Link] T_Nut_2020_M028  label="T-Nut_2020_M028"
  LinkPlacement = pos=(419.9,-8,559.851) rot=(1,0,0;1.5708rad)
  LinkedObject = -> <external ../parts/T-nut_20.FCStd>#Part__Feature
  Placement = pos=(419.9,-8,559.851) rot=(1,0,0;1.5708rad)
FEATURE [App::FeaturePython] Joint064  label="Slider030"  # Assembly joint (typed FeaturePython)
  Activated = true
  AngleMax = 0
  AngleMin = 0
  Detach1 = false
  Detach2 = false
  Distance = 0
  Distance2 = 0
  EnableAngleMax = false
  EnableAngleMin = false
  EnableLengthMax = false
  EnableLengthMin = false
  JointType = 3 (Slider)
  LengthMax = 0
  LengthMin = 0
  Offset2 = pos=(0,0,0) rot=(0,0,1;1.5708rad)
  Placement1 = pos=(-3,0,0) rot=(-0.57735,-0.57735,0.57735;4.18879rad)
  Placement2 = pos=(-3.1,-8,0) rot=(0.707107,0.707107,0;3.14159rad)
  Reference1 = -> Assembly [T_Nut_2020_M026.Edge27,T_Nut_2020_M026.Edge27]
  Reference2 = -> Assembly [Tslot20_heigh001.Edge81,Tslot20_heigh001.Vertex7]
FEATURE [App::FeaturePython] Joint065  label="Slider031"  # Assembly joint (typed FeaturePython)
  Activated = true
  AngleMax = 0
  AngleMin = 0
  Detach1 = false
  Detach2 = false
  Distance = 0
  Distance2 = 0
  EnableAngleMax = false
  EnableAngleMin = false
  EnableLengthMax = false
  EnableLengthMin = false
  JointType = 3 (Slider)
  LengthMax = 0
  LengthMin = 0
  Offset2 = pos=(0,0,0) rot=(0,0,1;1.5708rad)
  Placement1 = pos=(3,-5.25,7.1e-15) rot=(-0.57735,-0.57735,0.57735;4.18879rad)
  Placement2 = pos=(3.1,-8,0) rot=(0.707107,0.707107,0;3.14159rad)
  Reference1 = -> Assembly [T_Nut_2020_M025.Edge8,T_Nut_2020_M025.Vertex8]
  Reference2 = -> Assembly [Tslot20_heigh.Edge86,Tslot20_heigh.Vertex12]
FEATURE [App::FeaturePython] Joint066  label="Slider032"  # Assembly joint (typed FeaturePython)
  Activated = true
  AngleMax = 0
  AngleMin = 0
  Detach1 = false
  Detach2 = false
  Distance = 0
  Distance2 = 0
  EnableAngleMax = false
  EnableAngleMin = false
  EnableLengthMax = false
  EnableLengthMin = false
  JointType = 3 (Slider)
  LengthMax = 0
  LengthMin = 0
  Offset2 = pos=(0,0,0) rot=(0,0,1;1.5708rad)
  Placement1 = pos=(-3,0,0) rot=(-0.57735,-0.57735,0.57735;4.18879rad)
  Placement2 = pos=(-3.1,-8,580) rot=(0.707107,0.707107,0;3.14159rad)
  Reference1 = -> Assembly [T_Nut_2020_M028.Edge27,T_Nut_2020_M028.Edge27]
  Reference2 = -> Assembly [Tslot20_heigh001.Edge81,Tslot20_heigh001.Vertex43]
FEATURE [App::FeaturePython] Joint067  label="Slider033"  # Assembly joint (typed FeaturePython)
  Activated = true
  AngleMax = 0
  AngleMin = 0
  Detach1 = false
  Detach2 = false
  Distance = 0
  Distance2 = 0
  EnableAngleMax = false
  EnableAngleMin = false
  EnableLengthMax = false
  EnableLengthMin = false
  JointType = 3 (Slider)
  LengthMax = 0
  LengthMin = 0
  Offset2 = pos=(0,0,0) rot=(0,0,1;1.5708rad)
  Placement1 = pos=(3,0,0) rot=(-0.57735,-0.57735,0.57735;4.18879rad)
  Placement2 = pos=(3.1,-8,580) rot=(0.707107,0.707107,0;3.14159rad)
  Reference1 = -> Assembly [T_Nut_2020_M027.Edge8,T_Nut_2020_M027.Edge8]
  Reference2 = -> Assembly [Tslot20_heigh.Edge86,Tslot20_heigh.Vertex48]
FEATURE [App::Link] plate_side001
  LinkedObject = -> <external asm_plate_side.FCStd>#plate_side
FEATURE [App::Link] TAH15_M5_L010  label="TAH15-M5-L010"
  LinkPlacement = pos=(210,240,3) rot=(0.707107,0,-0.707107;3.14159rad)
  LinkedObject = -> <external asm_plate_side.FCStd>#TAH15_M5_L6
  Placement = pos=(210,240,3) rot=(0.707107,0,-0.707107;3.14159rad)
FEATURE [App::Link] TAH15_M5_L011  label="TAH15-M5-L011"
  LinkPlacement = pos=(-210,-240,3) rot=(0.707107,0,-0.707107;3.14159rad)
  LinkedObject = -> <external asm_plate_side.FCStd>#TAH15_M5_L007
  Placement = pos=(-210,-240,3) rot=(0.707107,0,-0.707107;3.14159rad)
FEATURE [App::Link] TAH15_M5_L012  label="TAH15-M5-L012"
  LinkPlacement = pos=(210,-240,3) rot=(0.707107,0,-0.707107;3.14159rad)
  LinkedObject = -> <external asm_plate_side.FCStd>#TAH15_M5_L008
  Placement = pos=(210,-240,3) rot=(0.707107,0,-0.707107;3.14159rad)
FEATURE [App::Link] TAH15_M5_L013  label="TAH15-M5-L013"
  LinkPlacement = pos=(-210,240,3) rot=(0.707107,0,-0.707107;3.14159rad)
  LinkedObject = -> <external asm_plate_side.FCStd>#TAH15_M5_L009
  Placement = pos=(-210,240,3) rot=(0.707107,0,-0.707107;3.14159rad)
FEATURE [Assembly::AssemblyLink] asm_plate_side001
  Group = -> [plate_side001,TAH15_M5_L010,TAH15_M5_L011,TAH15_M5_L012,TAH15_M5_L013]
  LinkedObject = -> <external asm_plate_side.FCStd>#Assembly
  Origin = -> Origin009
  Placement = pos=(210.1,-11.1095,299.726) rot=(1,0,0;1.5708rad)
  Rigid = true
FEATURE [App::FeaturePython] Joint068  label="Fixed033"  # Assembly joint (typed FeaturePython)
  Activated = true
  AngleMax = 0
  AngleMin = 0
  Detach1 = false
  Detach2 = false
  Distance = 0
  Distance2 = 0
  EnableAngleMax = false
  EnableAngleMin = false
  EnableLengthMax = false
  EnableLengthMin = false
  JointType = 0 (Fixed)
  LengthMax = 0
  LengthMin = 0
  Placement1 = pos=(5.5095,0,0) rot=(0,1,0;1.5708rad)
  Placement2 = pos=(0,0,0.6) rot=(0,0,1;0rad)
  Reference1 = -> Assembly [asm_plate_side001.TAH15_M5_L013.Edge12,asm_plate_side001.TAH15_M5_L013.Edge12]
  Reference2 = -> Assembly [T_Nut_2020_M027.Edge6,T_Nut_2020_M027.Edge6]
FEATURE [App::Link] T_Nut_2020_M029  label="T-Nut_2020_M029"
  LinkPlacement = pos=(-0.1,20.447,38) rot=(0,0,1;0rad)
  LinkedObject = -> <external ../parts/T-nut_20.FCStd>#Part__Feature
  Placement = pos=(-0.1,20.447,38) rot=(0,0,1;0rad)
FEATURE [App::Link] T_Nut_2020_M030  label="T-Nut_2020_M030"
  LinkPlacement = pos=(0.1,200.635,38) rot=(0,0,1;0rad)
  LinkedObject = -> <external ../parts/T-nut_20.FCStd>#Part__Feature
  Placement = pos=(0.1,200.635,38) rot=(0,0,1;0rad)
FEATURE [App::FeaturePython] Joint069  label="Slider034"  # Assembly joint (typed FeaturePython)
  Activated = true
  AngleMax = 0
  AngleMin = 0
  Detach1 = false
  Detach2 = false
  Distance = 0
  Distance2 = 0
  EnableAngleMax = false
  EnableAngleMin = false
  EnableLengthMax = false
  EnableLengthMin = false
  JointType = 3 (Slider)
  LengthMax = 0
  LengthMin = 0
  Offset2 = pos=(0,0,0) rot=(0,0,1;1.5708rad)
  Placement1 = pos=(3,0,0) rot=(-0.57735,-0.57735,0.57735;4.18879rad)
  Placement2 = pos=(3.1,-8,200) rot=(0.707107,0.707107,0;3.14159rad)
  Reference1 = -> Assembly [T_Nut_2020_M030.Edge8,T_Nut_2020_M030.Edge8]
  Reference2 = -> Assembly [Tslot20_wid002.Edge86,Tslot20_wid002.Vertex48]
FEATURE [App::Link] Hex_screw_M5_10_008  label="Hex screw M5 10.008"
  LinkPlacement = pos=(7.08683,165.078,32.6) rot=(0,0,1;0rad)
  LinkedObject = -> <external ../secondary/bolts.FCStd>#Body004
  Placement = pos=(7.08683,165.078,32.6) rot=(0,0,1;0rad)
FEATURE [App::Link] Hex_screw_M5_10_009  label="Hex screw M5 10.009"
  LinkPlacement = pos=(6.88683,-15.1105,32.6) rot=(0,0,1;0rad)
  LinkedObject = -> <external ../secondary/bolts.FCStd>#Body004
  Placement = pos=(6.88683,-15.1105,32.6) rot=(0,0,1;0rad)
FEATURE [App::Link] Hex_screw_M5_10_010  label="Hex screw M5 10.010"
  LinkPlacement = pos=(55.6112,7.08683,12.6) rot=(0,0,1;1.5708rad)
  LinkedObject = -> <external ../secondary/bolts.FCStd>#Body004
  Placement = pos=(55.6112,7.08683,12.6) rot=(0,0,1;1.5708rad)
FEATURE [App::Link] Hex_screw_M5_10_011  label="Hex screw M5 10.011"
  LinkPlacement = pos=(55.848,227.087,12.6) rot=(0,0,1;1.5708rad)
  LinkedObject = -> <external ../secondary/bolts.FCStd>#Body004
  Placement = pos=(55.848,227.087,12.6) rot=(0,0,1;1.5708rad)
FEATURE [App::FeaturePython] Joint070  label="Fixed034"  # Assembly joint (typed FeaturePython)
  Activated = true
  AngleMax = 0
  AngleMin = 0
  Detach1 = false
  Detach2 = false
  Distance = 0
  Distance2 = 0
  EnableAngleMax = false
  EnableAngleMin = false
  EnableLengthMax = false
  EnableLengthMin = false
  JointType = 0 (Fixed)
  LengthMax = 0
  LengthMin = 0
  Offset2 = pos=(0,0,-6) rot=(0,0,1;0rad)
  Placement1 = pos=(-6.98683,35.5575,-7.1e-15) rot=(0,0,1;0rad)
  Placement2 = pos=(0,-6.7e-15,-5.4) rot=(0,0,1;0rad)
  Reference1 = -> Assembly [Hex_screw_M5_10_008.Edge2,Hex_screw_M5_10_008.Edge2]
  Reference2 = -> Assembly [T_Nut_2020_M030.Edge6,T_Nut_2020_M030.Edge6]
FEATURE [App::FeaturePython] Joint071  label="Slider035"  # Assembly joint (typed FeaturePython)
  Activated = true
  AngleMax = 0
  AngleMin = 0
  Detach1 = false
  Detach2 = false
  Distance = 0
  Distance2 = 0
  EnableAngleMax = false
  EnableAngleMin = false
  EnableLengthMax = false
  EnableLengthMin = false
  JointType = 3 (Slider)
  LengthMax = 0
  LengthMin = 0
  Offset2 = pos=(0,0,0) rot=(0,0,1;1.5708rad)
  Placement1 = pos=(-3,0,0) rot=(-0.57735,-0.57735,0.57735;4.18879rad)
  Placement2 = pos=(-3.1,-8,0) rot=(0.707107,0.707107,0;3.14159rad)
  Reference1 = -> Assembly [T_Nut_2020_M029.Edge27,T_Nut_2020_M029.Edge27]
  Reference2 = -> Assembly [Tslot20_wid002.Edge81,Tslot20_wid002.Vertex7]
FEATURE [App::FeaturePython] Joint072  label="Fixed035"  # Assembly joint (typed FeaturePython)
  Activated = true
  AngleMax = 0
  AngleMin = 0
  Detach1 = false
  Detach2 = false
  Distance = 0
  Distance2 = 0
  EnableAngleMax = false
  EnableAngleMin = false
  EnableLengthMax = false
  EnableLengthMin = false
  JointType = 0 (Fixed)
  LengthMax = 0
  LengthMin = 0
  Offset2 = pos=(0,0,-6) rot=(0,0,1;0rad)
  Placement1 = pos=(-6.98683,35.5575,-7.1e-15) rot=(0,0,1;0rad)
  Placement2 = pos=(0,-6.7e-15,-5.4) rot=(0,0,1;0rad)
  Reference1 = -> Assembly [Hex_screw_M5_10_009.Edge2,Hex_screw_M5_10_009.Edge2]
  Reference2 = -> Assembly [T_Nut_2020_M029.Edge6,T_Nut_2020_M029.Edge6]
FEATURE [App::Link] T_Nut_2020_M031  label="T-Nut_2020_M031"
  LinkPlacement = pos=(20.0537,0.1,18) rot=(0,0,1;1.5708rad)
  LinkedObject = -> <external ../parts/T-nut_20.FCStd>#Part__Feature
  Placement = pos=(20.0537,0.1,18) rot=(0,0,1;1.5708rad)
FEATURE [App::Link] T_Nut_2020_M032  label="T-Nut_2020_M032"
  LinkPlacement = pos=(20.2905,220.1,18) rot=(0,0,1;1.5708rad)
  LinkedObject = -> <external ../parts/T-nut_20.FCStd>#Part__Feature
  Placement = pos=(20.2905,220.1,18) rot=(0,0,1;1.5708rad)
FEATURE [App::FeaturePython] Joint073  label="Slider036"  # Assembly joint (typed FeaturePython)
  Activated = true
  AngleMax = 0
  AngleMin = 0
  Detach1 = false
  Detach2 = false
  Distance = 0
  Distance2 = 0
  EnableAngleMax = false
  EnableAngleMin = false
  EnableLengthMax = false
  EnableLengthMin = false
  JointType = 3 (Slider)
  LengthMax = 0
  LengthMin = 0
  Placement1 = pos=(3,-3.6e-15,3.6e-15) rot=(-0.57735,-0.57735,0.57735;4.18879rad)
  Placement2 = pos=(-8,3.1,0) rot=(0,0,1;0rad)
  Reference1 = -> Assembly [T_Nut_2020_M032.Edge8,T_Nut_2020_M032.Edge8]
  Reference2 = -> Assembly [Tslot20_len003.Edge104,Tslot20_len003.Vertex32]
FEATURE [App::FeaturePython] Joint074  label="Fixed036"  # Assembly joint (typed FeaturePython)
  Activated = true
  AngleMax = 0
  AngleMin = 0
  Detach1 = false
  Detach2 = false
  Distance = 0
  Distance2 = 0
  EnableAngleMax = false
  EnableAngleMin = false
  EnableLengthMax = false
  EnableLengthMin = false
  JointType = 0 (Fixed)
  LengthMax = 0
  LengthMin = 0
  Offset2 = pos=(0,0,-6) rot=(0,0,1;0rad)
  Placement1 = pos=(-6.98683,35.5575,0) rot=(0,0,1;0rad)
  Placement2 = pos=(0,-6.7e-15,-5.4) rot=(0,0,1;0rad)
  Reference1 = -> Assembly [Hex_screw_M5_10_011.Edge2,Hex_screw_M5_10_011.Edge2]
  Reference2 = -> Assembly [T_Nut_2020_M032.Edge6,T_Nut_2020_M032.Edge6]
FEATURE [App::FeaturePython] Joint075  label="Slider037"  # Assembly joint (typed FeaturePython)
  Activated = true
  AngleMax = 0
  AngleMin = 0
  Detach1 = false
  Detach2 = false
  Distance = 0
  Distance2 = 0
  EnableAngleMax = false
  EnableAngleMin = false
  EnableLengthMax = false
  EnableLengthMin = false
  JointType = 3 (Slider)
  LengthMax = 0
  LengthMin = 0
  Placement1 = pos=(3,0,0) rot=(-0.57735,-0.57735,0.57735;4.18879rad)
  Placement2 = pos=(-8,3.1,0) rot=(0,0,1;0rad)
  Reference1 = -> Assembly [T_Nut_2020_M031.Edge8,T_Nut_2020_M031.Edge8]
  Reference2 = -> Assembly [Tslot20_len002.Edge104,Tslot20_len002.Vertex32]
FEATURE [App::FeaturePython] Joint076  label="Fixed037"  # Assembly joint (typed FeaturePython)
  Activated = true
  AngleMax = 0
  AngleMin = 0
  Detach1 = false
  Detach2 = false
  Distance = 0
  Distance2 = 0
  EnableAngleMax = false
  EnableAngleMin = false
  EnableLengthMax = false
  EnableLengthMin = false
  JointType = 0 (Fixed)
  LengthMax = 0
  LengthMin = 0
  Offset2 = pos=(0,0,-6) rot=(0,0,1;0rad)
  Placement1 = pos=(-6.98683,35.5575,0) rot=(0,0,1;0rad)
  Placement2 = pos=(0,-6.7e-15,-5.4) rot=(0,0,1;0rad)
  Reference1 = -> Assembly [Hex_screw_M5_10_010.Edge2,Hex_screw_M5_10_010.Edge2]
  Reference2 = -> Assembly [T_Nut_2020_M031.Edge6,T_Nut_2020_M031.Edge6]
FEATURE [App::Link] T_Nut_2020_M033  label="T-Nut_2020_M033"
  LinkPlacement = pos=(420.1,198.193,38) rot=(0,0,1;0rad)
  LinkedObject = -> <external ../parts/T-nut_20.FCStd>#Part__Feature
  Placement = pos=(420.1,198.193,38) rot=(0,0,1;0rad)
FEATURE [App::Link] T_Nut_2020_M034  label="T-Nut_2020_M034"
  LinkPlacement = pos=(399.431,220.1,18) rot=(0,0,1;1.5708rad)
  LinkedObject = -> <external ../parts/T-nut_20.FCStd>#Part__Feature
  Placement = pos=(399.431,220.1,18) rot=(0,0,1;1.5708rad)
FEATURE [App::Link] T_Nut_2020_M035  label="T-Nut_2020_M035"
  LinkPlacement = pos=(420.1,20.7376,38) rot=(0,0,1;0rad)
  LinkedObject = -> <external ../parts/T-nut_20.FCStd>#Part__Feature
  Placement = pos=(420.1,20.7376,38) rot=(0,0,1;0rad)
FEATURE [App::Link] T_Nut_2020_M036  label="T-Nut_2020_M036"
  LinkPlacement = pos=(398.375,0.1,18) rot=(0,0,1;1.5708rad)
  LinkedObject = -> <external ../parts/T-nut_20.FCStd>#Part__Feature
  Placement = pos=(398.375,0.1,18) rot=(0,0,1;1.5708rad)
FEATURE [App::FeaturePython] Joint077  label="Slider038"  # Assembly joint (typed FeaturePython)
  Activated = true
  AngleMax = 0
  AngleMin = 0
  Detach1 = false
  Detach2 = false
  Distance = 0
  Distance2 = 0
  EnableAngleMax = false
  EnableAngleMin = false
  EnableLengthMax = false
  EnableLengthMin = false
  JointType = 3 (Slider)
  LengthMax = 0
  LengthMin = 0
  Offset2 = pos=(0,0,0) rot=(0,0,-1;1.5708rad)
  Placement1 = pos=(3,5.25,-7.1e-15) rot=(-0.57735,-0.57735,0.57735;4.18879rad)
  Placement2 = pos=(3.1,8,0) rot=(-0.707107,0.707107,0;3.14159rad)
  Reference1 = -> Assembly [T_Nut_2020_M033.Edge8,T_Nut_2020_M033.Vertex7]
  Reference2 = -> Assembly [Tslot20_wid003.Edge99,Tslot20_wid003.Vertex25]
FEATURE [App::FeaturePython] Joint078  label="Slider039"  # Assembly joint (typed FeaturePython)
  Activated = true
  AngleMax = 0
  AngleMin = 0
  Detach1 = false
  Detach2 = false
  Distance = 0
  Distance2 = 0
  EnableAngleMax = false
  EnableAngleMin = false
  EnableLengthMax = false
  EnableLengthMin = false
  JointType = 3 (Slider)
  LengthMax = 0
  LengthMin = 0
  Offset2 = pos=(0,0,0) rot=(0,0,-1;1.5708rad)
  Placement1 = pos=(3,0,0) rot=(-0.57735,-0.57735,0.57735;4.18879rad)
  Placement2 = pos=(3.1,8,200) rot=(-0.707107,0.707107,0;3.14159rad)
  Reference1 = -> Assembly [T_Nut_2020_M035.Edge8,T_Nut_2020_M035.Edge8]
  Reference2 = -> Assembly [Tslot20_wid003.Edge99,Tslot20_wid003.Vertex61]
FEATURE [App::FeaturePython] Joint079  label="Slider040"  # Assembly joint (typed FeaturePython)
  Activated = true
  AngleMax = 0
  AngleMin = 0
  Detach1 = false
  Detach2 = false
  Distance = 0
  Distance2 = 0
  EnableAngleMax = false
  EnableAngleMin = false
  EnableLengthMax = false
  EnableLengthMin = false
  JointType = 3 (Slider)
  LengthMax = 0
  LengthMin = 0
  Placement1 = pos=(3,0,0) rot=(-0.57735,-0.57735,0.57735;4.18879rad)
  Placement2 = pos=(-8,3.1,400) rot=(0,0,1;0rad)
  Reference1 = -> Assembly [T_Nut_2020_M036.Edge8,T_Nut_2020_M036.Edge8]
  Reference2 = -> Assembly [Tslot20_len002.Edge104,Tslot20_len002.Vertex67]
FEATURE [App::FeaturePython] Joint080  label="Slider041"  # Assembly joint (typed FeaturePython)
  Activated = true
  AngleMax = 0
  AngleMin = 0
  Detach1 = false
  Detach2 = false
  Distance = 0
  Distance2 = 0
  EnableAngleMax = false
  EnableAngleMin = false
  EnableLengthMax = false
  EnableLengthMin = false
  JointType = 3 (Slider)
  LengthMax = 0
  LengthMin = 0
  Placement1 = pos=(3,0,3.6e-15) rot=(-0.57735,-0.57735,0.57735;4.18879rad)
  Placement2 = pos=(-8,3.1,400) rot=(0,0,1;0rad)
  Reference1 = -> Assembly [T_Nut_2020_M034.Edge8,T_Nut_2020_M034.Edge8]
  Reference2 = -> Assembly [Tslot20_len003.Edge104,Tslot20_len003.Vertex67]
FEATURE [App::Link] Hex_screw_M5_10_012  label="Hex screw M5 10.012"
  LinkPlacement = pos=(434.989,227.087,12.6) rot=(0,0,1;1.5708rad)
  LinkedObject = -> <external ../secondary/bolts.FCStd>#Body004
  Placement = pos=(434.989,227.087,12.6) rot=(0,0,1;1.5708rad)
FEATURE [App::Link] Hex_screw_M5_10_013  label="Hex screw M5 10.013"
  LinkPlacement = pos=(427.087,162.636,32.6) rot=(0,0,1;0rad)
  LinkedObject = -> <external ../secondary/bolts.FCStd>#Body004
  Placement = pos=(427.087,162.636,32.6) rot=(0,0,1;0rad)
FEATURE [App::Link] Hex_screw_M5_10_014  label="Hex screw M5 10.014"
  LinkPlacement = pos=(433.932,7.08683,12.6) rot=(0,0,1;1.5708rad)
  LinkedObject = -> <external ../secondary/bolts.FCStd>#Body004
  Placement = pos=(433.932,7.08683,12.6) rot=(0,0,1;1.5708rad)
FEATURE [App::Link] Hex_screw_M5_10_015  label="Hex screw M5 10.015"
  LinkPlacement = pos=(427.087,-14.8199,32.6) rot=(0,0,1;0rad)
  LinkedObject = -> <external ../secondary/bolts.FCStd>#Body004
  Placement = pos=(427.087,-14.8199,32.6) rot=(0,0,1;0rad)
FEATURE [App::Link] Hex_screw_M5_10_016  label="Hex screw M5 10.016"
  LinkPlacement = pos=(55.848,227.087,12.6) rot=(0,0,1;1.5708rad)
  LinkedObject = -> <external ../secondary/bolts.FCStd>#Body004
  Placement = pos=(55.848,227.087,12.6) rot=(0,0,1;1.5708rad)
FEATURE [App::FeaturePython] Joint081  label="Fixed038"  # Assembly joint (typed FeaturePython)
  Activated = true
  AngleMax = 0
  AngleMin = 0
  Detach1 = false
  Detach2 = false
  Distance = 0
  Distance2 = 0
  EnableAngleMax = false
  EnableAngleMin = false
  EnableLengthMax = false
  EnableLengthMin = false
  JointType = 0 (Fixed)
  LengthMax = 0
  LengthMin = 0
  Offset2 = pos=(0,0,-6) rot=(0,0,1;0rad)
  Placement1 = pos=(-6.98683,35.5575,0) rot=(0,0,1;0rad)
  Placement2 = pos=(0,-6.7e-15,-5.4) rot=(0,0,1;0rad)
  Reference1 = -> Assembly [Hex_screw_M5_10_016.Edge2,Hex_screw_M5_10_016.Edge2]
  Reference2 = -> Assembly [T_Nut_2020_M032.Edge6,T_Nut_2020_M032.Edge6]
FEATURE [App::FeaturePython] Joint082  label="Fixed039"  # Assembly joint (typed FeaturePython)
  Activated = true
  AngleMax = 0
  AngleMin = 0
  Detach1 = false
  Detach2 = false
  Distance = 0
  Distance2 = 0
  EnableAngleMax = false
  EnableAngleMin = false
  EnableLengthMax = false
  EnableLengthMin = false
  JointType = 0 (Fixed)
  LengthMax = 0
  LengthMin = 0
  Offset2 = pos=(0,0,-6) rot=(0,0,1;0rad)
  Placement1 = pos=(-6.98683,35.5575,0) rot=(0,0,1;0rad)
  Placement2 = pos=(0,-6.7e-15,-5.4) rot=(0,0,1;0rad)
  Reference1 = -> Assembly [Hex_screw_M5_10_012.Edge2,Hex_screw_M5_10_012.Edge2]
  Reference2 = -> Assembly [T_Nut_2020_M034.Edge6,T_Nut_2020_M034.Edge6]
FEATURE [App::FeaturePython] Joint083  label="Fixed040"  # Assembly joint (typed FeaturePython)
  Activated = true
  AngleMax = 0
  AngleMin = 0
  Detach1 = false
  Detach2 = false
  Distance = 0
  Distance2 = 0
  EnableAngleMax = false
  EnableAngleMin = false
  EnableLengthMax = false
  EnableLengthMin = false
  JointType = 0 (Fixed)
  LengthMax = 0
  LengthMin = 0
  Offset2 = pos=(0,0,-6) rot=(0,0,1;0rad)
  Placement1 = pos=(-6.98683,35.5575,7.1e-15) rot=(0,0,1;0rad)
  Placement2 = pos=(0,-6.7e-15,-5.4) rot=(0,0,1;0rad)
  Reference1 = -> Assembly [Hex_screw_M5_10_013.Edge2,Hex_screw_M5_10_013.Edge2]
  Reference2 = -> Assembly [T_Nut_2020_M033.Edge6,T_Nut_2020_M033.Edge6]
FEATURE [App::FeaturePython] Joint084  label="Fixed041"  # Assembly joint (typed FeaturePython)
  Activated = true
  AngleMax = 0
  AngleMin = 0
  Detach1 = false
  Detach2 = false
  Distance = 0
  Distance2 = 0
  EnableAngleMax = false
  EnableAngleMin = false
  EnableLengthMax = false
  EnableLengthMin = false
  JointType = 0 (Fixed)
  LengthMax = 0
  LengthMin = 0
  Offset2 = pos=(0,0,-6) rot=(0,0,1;0rad)
  Placement1 = pos=(-6.98683,35.5575,7.1e-15) rot=(0,0,1;0rad)
  Placement2 = pos=(0,-6.7e-15,-5.4) rot=(0,0,1;0rad)
  Reference1 = -> Assembly [Hex_screw_M5_10_015.Edge2,Hex_screw_M5_10_015.Edge2]
  Reference2 = -> Assembly [T_Nut_2020_M035.Edge6,T_Nut_2020_M035.Edge6]
FEATURE [App::FeaturePython] Joint085  label="Fixed042"  # Assembly joint (typed FeaturePython)
  Activated = true
  AngleMax = 0
  AngleMin = 0
  Detach1 = false
  Detach2 = false
  Distance = 0
  Distance2 = 0
  EnableAngleMax = false
  EnableAngleMin = false
  EnableLengthMax = false
  EnableLengthMin = false
  JointType = 0 (Fixed)
  LengthMax = 0
  LengthMin = 0
  Offset2 = pos=(0,0,-6) rot=(0,0,1;0rad)
  Placement1 = pos=(-6.98683,35.5575,0) rot=(0,0,1;0rad)
  Placement2 = pos=(0,-6.7e-15,-5.4) rot=(0,0,1;0rad)
  Reference1 = -> Assembly [Hex_screw_M5_10_014.Edge2,Hex_screw_M5_10_014.Edge2]
  Reference2 = -> Assembly [T_Nut_2020_M036.Edge6,T_Nut_2020_M036.Edge6]
FEATURE [App::Link] T_Nut_2020_M037  label="T-Nut_2020_M037"
  LinkPlacement = pos=(-0.1,212,51.3636) rot=(1,0,0;1.5708rad)
  LinkedObject = -> <external ../parts/T-nut_20.FCStd>#Part__Feature
  Placement = pos=(-0.1,212,51.3636) rot=(1,0,0;1.5708rad)
FEATURE [App::Link] T_Nut_2020_M038  label="T-Nut_2020_M038"
  LinkPlacement = pos=(8,219.9,31.3156) rot=(0.57735,0.57735,0.57735;2.0944rad)
  LinkedObject = -> <external ../parts/T-nut_20.FCStd>#Part__Feature
  Placement = pos=(8,219.9,31.3156) rot=(0.57735,0.57735,0.57735;2.0944rad)
FEATURE [App::FeaturePython] Joint086  label="Slider042"  # Assembly joint (typed FeaturePython)
  Activated = true
  AngleMax = 0
  AngleMin = 0
  Detach1 = false
  Detach2 = false
  Distance = 0
  Distance2 = 0
  EnableAngleMax = false
  EnableAngleMin = false
  EnableLengthMax = false
  EnableLengthMin = false
  JointType = 3 (Slider)
  LengthMax = 0
  LengthMin = 0
  Offset2 = pos=(0,0,0) rot=(0,0,1;1.5708rad)
  Placement1 = pos=(-3,0,0) rot=(-0.57735,-0.57735,0.57735;4.18879rad)
  Placement2 = pos=(-3.1,-8,0) rot=(0.707107,0.707107,0;3.14159rad)
  Reference1 = -> Assembly [T_Nut_2020_M037.Edge27,T_Nut_2020_M037.Edge27]
  Reference2 = -> Assembly [Tslot20_heigh002.Edge81,Tslot20_heigh002.Vertex7]
FEATURE [App::FeaturePython] Joint087  label="Slider043"  # Assembly joint (typed FeaturePython)
  Activated = true
  AngleMax = 0
  AngleMin = 0
  Detach1 = false
  Detach2 = false
  Distance = 0
  Distance2 = 0
  EnableAngleMax = false
  EnableAngleMin = false
  EnableLengthMax = false
  EnableLengthMin = false
  JointType = 3 (Slider)
  LengthMax = 0
  LengthMin = 0
  Offset2 = pos=(0,0,0) rot=(0,0,1;3.14159rad)
  Placement1 = pos=(-3,0,9e-16) rot=(-0.57735,-0.57735,0.57735;4.18879rad)
  Placement2 = pos=(8,-3.1,0) rot=(0,0,1;3.14159rad)
  Reference1 = -> Assembly [T_Nut_2020_M038.Edge27,T_Nut_2020_M038.Edge27]
  Reference2 = -> Assembly [Tslot20_heigh002.Edge90,Tslot20_heigh002.Vertex16]
FEATURE [App::Link] Hex_screw_M5_10_017  label="Hex screw M5 10.017"
  LinkPlacement = pos=(2.6,226.887,-4.24188) rot=(0.57735,0.57735,0.57735;2.0944rad)
  LinkedObject = -> <external ../secondary/bolts.FCStd>#Body004
  Placement = pos=(2.6,226.887,-4.24188) rot=(0.57735,0.57735,0.57735;2.0944rad)
FEATURE [App::Link] Hex_screw_M5_10_018  label="Hex screw M5 10.018"
  LinkPlacement = pos=(6.88683,217.4,15.8061) rot=(1,0,0;1.5708rad)
  LinkedObject = -> <external ../secondary/bolts.FCStd>#Body004
  Placement = pos=(6.88683,217.4,15.8061) rot=(1,0,0;1.5708rad)
FEATURE [App::FeaturePython] Joint088  label="Fixed043"  # Assembly joint (typed FeaturePython)
  Activated = true
  AngleMax = 0
  AngleMin = 0
  Detach1 = false
  Detach2 = false
  Distance = 0
  Distance2 = 0
  EnableAngleMax = false
  EnableAngleMin = false
  EnableLengthMax = false
  EnableLengthMin = false
  JointType = 0 (Fixed)
  LengthMax = 0
  LengthMin = 0
  Offset2 = pos=(0,0,-6) rot=(0,0,1;0rad)
  Placement1 = pos=(-6.98683,35.5575,1.8e-15) rot=(0,0,1;0rad)
  Placement2 = pos=(-2e-15,-6.7e-15,-5.4) rot=(0,0,1;0rad)
  Reference1 = -> Assembly [Hex_screw_M5_10_017.Edge2,Hex_screw_M5_10_017.Edge2]
  Reference2 = -> Assembly [T_Nut_2020_M038.Edge6,T_Nut_2020_M038.Edge6]
FEATURE [App::FeaturePython] Joint089  label="Fixed044"  # Assembly joint (typed FeaturePython)
  Activated = true
  AngleMax = 0
  AngleMin = 0
  Detach1 = false
  Detach2 = false
  Distance = 0
  Distance2 = 0
  EnableAngleMax = false
  EnableAngleMin = false
  EnableLengthMax = false
  EnableLengthMin = false
  JointType = 0 (Fixed)
  LengthMax = 0
  LengthMin = 0
  Offset2 = pos=(0,0,-6) rot=(0,0,1;0rad)
  Placement1 = pos=(-6.98683,35.5575,0) rot=(0,0,1;0rad)
  Placement2 = pos=(0,-6.7e-15,-5.4) rot=(0,0,1;0rad)
  Reference1 = -> Assembly [Hex_screw_M5_10_018.Edge2,Hex_screw_M5_10_018.Edge2]
  Reference2 = -> Assembly [T_Nut_2020_M037.Edge6,T_Nut_2020_M037.Edge6]
FEATURE [App::Link] Hex_screw_M5_10_019  label="Hex screw M5 10.019"
  LinkPlacement = pos=(6.88683,2.6,86.8512) rot=(-1,0,0;1.5708rad)
  LinkedObject = -> <external ../secondary/bolts.FCStd>#Body004
  Placement = pos=(6.88683,2.6,86.8512) rot=(-1,0,0;1.5708rad)
FEATURE [App::Link] Hex_screw_M5_10_020  label="Hex screw M5 10.020"
  LinkPlacement = pos=(2.6,-6.88683,66.3386) rot=(0.57735,-0.57735,0.57735;4.18879rad)
  LinkedObject = -> <external ../secondary/bolts.FCStd>#Body004
  Placement = pos=(2.6,-6.88683,66.3386) rot=(0.57735,-0.57735,0.57735;4.18879rad)
FEATURE [App::Link] T_Nut_2020_M039  label="T-Nut_2020_M039"
  LinkPlacement = pos=(8,0.1,30.7811) rot=(-0.57735,0.57735,-0.57735;2.0944rad)
  LinkedObject = -> <external ../parts/T-nut_20.FCStd>#Part__Feature
  Placement = pos=(8,0.1,30.7811) rot=(-0.57735,0.57735,-0.57735;2.0944rad)
FEATURE [App::Link] T_Nut_2020_M040  label="T-Nut_2020_M040"
  LinkPlacement = pos=(-0.1,8,51.2936) rot=(1,0,0;4.71239rad)
  LinkedObject = -> <external ../parts/T-nut_20.FCStd>#Part__Feature
  Placement = pos=(-0.1,8,51.2936) rot=(1,0,0;4.71239rad)
FEATURE [App::FeaturePython] Joint090  label="Slider044"  # Assembly joint (typed FeaturePython)
  Activated = true
  AngleMax = 0
  AngleMin = 0
  Detach1 = false
  Detach2 = false
  Distance = 0
  Distance2 = 0
  EnableAngleMax = false
  EnableAngleMin = false
  EnableLengthMax = false
  EnableLengthMin = false
  JointType = 3 (Slider)
  LengthMax = 0
  LengthMin = 0
  Offset2 = pos=(0,0,0) rot=(0,0,1;3.14159rad)
  Placement1 = pos=(-3,-5.25,7.1e-15) rot=(-0.57735,-0.57735,0.57735;4.18879rad)
  Placement2 = pos=(8,3.1,0) rot=(0,0,1;3.14159rad)
  Reference1 = -> Assembly [T_Nut_2020_M039.Edge27,T_Nut_2020_M039.Vertex17]
  Reference2 = -> Assembly [Tslot20_heigh.Edge95,Tslot20_heigh.Vertex21]
FEATURE [App::FeaturePython] Joint091  label="Fixed045"  # Assembly joint (typed FeaturePython)
  Activated = true
  AngleMax = 0
  AngleMin = 0
  Detach1 = false
  Detach2 = false
  Distance = 0
  Distance2 = 0
  EnableAngleMax = false
  EnableAngleMin = false
  EnableLengthMax = false
  EnableLengthMin = false
  JointType = 0 (Fixed)
  LengthMax = 0
  LengthMin = 0
  Offset2 = pos=(0,0,-6) rot=(0,0,1;0rad)
  Placement1 = pos=(-6.98683,35.5575,9e-16) rot=(0,0,1;0rad)
  Placement2 = pos=(6e-16,-6.3e-15,-5.4) rot=(0,0,1;0rad)
  Reference1 = -> Assembly [Hex_screw_M5_10_020.Edge2,Hex_screw_M5_10_020.Edge2]
  Reference2 = -> Assembly [T_Nut_2020_M039.Edge6,T_Nut_2020_M039.Edge6]
FEATURE [App::FeaturePython] Joint092  label="Slider045"  # Assembly joint (typed FeaturePython)
  Activated = true
  AngleMax = 0
  AngleMin = 0
  Detach1 = false
  Detach2 = false
  Distance = 0
  Distance2 = 0
  EnableAngleMax = false
  EnableAngleMin = false
  EnableLengthMax = false
  EnableLengthMin = false
  JointType = 3 (Slider)
  LengthMax = 0
  LengthMin = 0
  Offset2 = pos=(0,0,0) rot=(0,0,-1;1.5708rad)
  Placement1 = pos=(-3,-5.25,7.1e-15) rot=(-0.57735,-0.57735,0.57735;4.18879rad)
  Placement2 = pos=(-3.1,8,0) rot=(-0.707107,0.707107,0;3.14159rad)
  Reference1 = -> Assembly [T_Nut_2020_M040.Edge27,T_Nut_2020_M040.Vertex17]
  Reference2 = -> Assembly [Tslot20_heigh.Edge42,Tslot20_heigh.Vertex30]
FEATURE [App::FeaturePython] Joint093  label="Fixed046"  # Assembly joint (typed FeaturePython)
  Activated = true
  AngleMax = 0
  AngleMin = 0
  Detach1 = false
  Detach2 = false
  Distance = 0
  Distance2 = 0
  EnableAngleMax = false
  EnableAngleMin = false
  EnableLengthMax = false
  EnableLengthMin = false
  JointType = 0 (Fixed)
  LengthMax = 0
  LengthMin = 0
  Offset2 = pos=(0,0,-6) rot=(0,0,1;0rad)
  Placement1 = pos=(-6.98683,35.5575,1.8e-15) rot=(0,0,1;0rad)
  Placement2 = pos=(0,-6.7e-15,-5.4) rot=(0,0,1;0rad)
  Reference1 = -> Assembly [Hex_screw_M5_10_019.Edge2,Hex_screw_M5_10_019.Edge2]
  Reference2 = -> Assembly [T_Nut_2020_M040.Edge6,T_Nut_2020_M040.Edge6]
FEATURE [App::Link] T_Nut_2020_M041  label="T-Nut_2020_M041"
  LinkPlacement = pos=(412,-0.1,31.5859) rot=(0.57735,0.57735,-0.57735;4.18879rad)
  LinkedObject = -> <external ../parts/T-nut_20.FCStd>#Part__Feature
  Placement = pos=(412,-0.1,31.5859) rot=(0.57735,0.57735,-0.57735;4.18879rad)
FEATURE [App::Link] T_Nut_2020_M042  label="T-Nut_2020_M042"
  LinkPlacement = pos=(419.9,8,51.9116) rot=(1,0,0;4.71239rad)
  LinkedObject = -> <external ../parts/T-nut_20.FCStd>#Part__Feature
  Placement = pos=(419.9,8,51.9116) rot=(1,0,0;4.71239rad)
FEATURE [App::Link] Hex_screw_M5_10_021  label="Hex screw M5 10.021"
  LinkPlacement = pos=(417.4,6.88683,67.1434) rot=(-0.57735,-0.57735,0.57735;2.0944rad)
  LinkedObject = -> <external ../secondary/bolts.FCStd>#Body004
  Placement = pos=(417.4,6.88683,67.1434) rot=(-0.57735,-0.57735,0.57735;2.0944rad)
FEATURE [App::Link] Hex_screw_M5_10_022  label="Hex screw M5 10.022"
  LinkPlacement = pos=(426.887,2.6,87.4691) rot=(-1,0,0;1.5708rad)
  LinkedObject = -> <external ../secondary/bolts.FCStd>#Body004
  Placement = pos=(426.887,2.6,87.4691) rot=(-1,0,0;1.5708rad)
FEATURE [App::Link] Hex_screw_M5_10_023  label="Hex screw M5 10.023"
  LinkPlacement = pos=(417.4,226.887,67.2443) rot=(-0.57735,-0.57735,0.57735;2.0944rad)
  LinkedObject = -> <external ../secondary/bolts.FCStd>#Body004
  Placement = pos=(417.4,226.887,67.2443) rot=(-0.57735,-0.57735,0.57735;2.0944rad)
FEATURE [App::Link] Hex_screw_M5_10_024  label="Hex screw M5 10.024"
  LinkPlacement = pos=(427.087,217.4,15.8571) rot=(1,0,0;1.5708rad)
  LinkedObject = -> <external ../secondary/bolts.FCStd>#Body004
  Placement = pos=(427.087,217.4,15.8571) rot=(1,0,0;1.5708rad)
FEATURE [App::Link] T_Nut_2020_M043  label="T-Nut_2020_M043"
  LinkPlacement = pos=(412,219.9,31.6868) rot=(0.57735,0.57735,-0.57735;4.18879rad)
  LinkedObject = -> <external ../parts/T-nut_20.FCStd>#Part__Feature
  Placement = pos=(412,219.9,31.6868) rot=(0.57735,0.57735,-0.57735;4.18879rad)
FEATURE [App::Link] T_Nut_2020_M044  label="T-Nut_2020_M044"
  LinkPlacement = pos=(420.1,212,51.4147) rot=(1,0,0;1.5708rad)
  LinkedObject = -> <external ../parts/T-nut_20.FCStd>#Part__Feature
  Placement = pos=(420.1,212,51.4147) rot=(1,0,0;1.5708rad)
FEATURE [App::FeaturePython] Joint094  label="Slider046"  # Assembly joint (typed FeaturePython)
  Activated = true
  AngleMax = 0
  AngleMin = 0
  Detach1 = false
  Detach2 = false
  Distance = 0
  Distance2 = 0
  EnableAngleMax = false
  EnableAngleMin = false
  EnableLengthMax = false
  EnableLengthMin = false
  JointType = 3 (Slider)
  LengthMax = 0
  LengthMin = 0
  Placement1 = pos=(-3,5.25,0) rot=(-0.57735,-0.57735,0.57735;4.18879rad)
  Placement2 = pos=(-8,-3.1,0) rot=(0,0,1;0rad)
  Reference1 = -> Assembly [T_Nut_2020_M043.Edge27,T_Nut_2020_M043.Vertex10]
  Reference2 = -> Assembly [Tslot20_heigh003.Edge109,Tslot20_heigh003.Vertex37]
FEATURE [App::FeaturePython] Joint095  label="Fixed047"  # Assembly joint (typed FeaturePython)
  Activated = true
  AngleMax = 0
  AngleMin = 0
  Detach1 = false
  Detach2 = false
  Distance = 0
  Distance2 = 0
  EnableAngleMax = false
  EnableAngleMin = false
  EnableLengthMax = false
  EnableLengthMin = false
  JointType = 0 (Fixed)
  LengthMax = 0
  LengthMin = 0
  Offset2 = pos=(0,0,-6) rot=(0,0,1;0rad)
  Placement1 = pos=(-6.98683,35.5575,-5.68e-14) rot=(0,0,1;0rad)
  Placement2 = pos=(-7e-16,-6.7e-15,-5.4) rot=(0,0,1;0rad)
  Reference1 = -> Assembly [Hex_screw_M5_10_023.Edge2,Hex_screw_M5_10_023.Edge2]
  Reference2 = -> Assembly [T_Nut_2020_M043.Edge6,T_Nut_2020_M043.Edge6]
FEATURE [App::FeaturePython] Joint096  label="Slider047"  # Assembly joint (typed FeaturePython)
  Activated = true
  AngleMax = 0
  AngleMin = 0
  Detach1 = false
  Detach2 = false
  Distance = 0
  Distance2 = 0
  EnableAngleMax = false
  EnableAngleMin = false
  EnableLengthMax = false
  EnableLengthMin = false
  JointType = 3 (Slider)
  LengthMax = 0
  LengthMin = 0
  Offset2 = pos=(0,0,0) rot=(0,0,1;1.5708rad)
  Placement1 = pos=(3,0,0) rot=(-0.57735,-0.57735,0.57735;4.18879rad)
  Placement2 = pos=(3.1,-8,0) rot=(0.707107,0.707107,0;3.14159rad)
  Reference1 = -> Assembly [T_Nut_2020_M044.Edge8,T_Nut_2020_M044.Edge8]
  Reference2 = -> Assembly [Tslot20_heigh003.Edge86,Tslot20_heigh003.Vertex12]
FEATURE [App::FeaturePython] Joint097  label="Fixed048"  # Assembly joint (typed FeaturePython)
  Activated = true
  AngleMax = 0
  AngleMin = 0
  Detach1 = false
  Detach2 = false
  Distance = 0
  Distance2 = 0
  EnableAngleMax = false
  EnableAngleMin = false
  EnableLengthMax = false
  EnableLengthMin = false
  JointType = 0 (Fixed)
  LengthMax = 0
  LengthMin = 0
  Offset2 = pos=(0,0,-6) rot=(0,0,1;0rad)
  Placement1 = pos=(-6.98683,35.5575,0) rot=(0,0,1;0rad)
  Placement2 = pos=(0,-6.7e-15,-5.4) rot=(0,0,1;0rad)
  Reference1 = -> Assembly [Hex_screw_M5_10_024.Edge2,Hex_screw_M5_10_024.Edge2]
  Reference2 = -> Assembly [T_Nut_2020_M044.Edge6,T_Nut_2020_M044.Edge6]
FEATURE [App::FeaturePython] Joint098  label="Slider048"  # Assembly joint (typed FeaturePython)
  Activated = true
  AngleMax = 0
  AngleMin = 0
  Detach1 = false
  Detach2 = false
  Distance = 0
  Distance2 = 0
  EnableAngleMax = false
  EnableAngleMin = false
  EnableLengthMax = false
  EnableLengthMin = false
  JointType = 3 (Slider)
  LengthMax = 0
  LengthMin = 0
  Offset2 = pos=(0,0,0) rot=(0,0,-1;1.5708rad)
  Placement1 = pos=(-3,5.25,-8.9e-15) rot=(-0.57735,-0.57735,0.57735;4.18879rad)
  Placement2 = pos=(-3.1,8,0) rot=(-0.707107,0.707107,0;3.14159rad)
  Reference1 = -> Assembly [T_Nut_2020_M042.Edge27,T_Nut_2020_M042.Vertex10]
  Reference2 = -> Assembly [Tslot20_heigh001.Edge42,Tslot20_heigh001.Vertex30]
FEATURE [App::FeaturePython] Joint099  label="Fixed049"  # Assembly joint (typed FeaturePython)
  Activated = true
  AngleMax = 0
  AngleMin = 0
  Detach1 = false
  Detach2 = false
  Distance = 0
  Distance2 = 0
  EnableAngleMax = false
  EnableAngleMin = false
  EnableLengthMax = false
  EnableLengthMin = false
  JointType = 0 (Fixed)
  LengthMax = 0
  LengthMin = 0
  Offset2 = pos=(0,0,-6) rot=(0,0,1;0rad)
  Placement1 = pos=(-6.98683,35.5575,0) rot=(0,0,1;0rad)
  Placement2 = pos=(0,-6.7e-15,-5.4) rot=(0,0,1;0rad)
  Reference1 = -> Assembly [Hex_screw_M5_10_022.Edge2,Hex_screw_M5_10_022.Edge2]
  Reference2 = -> Assembly [T_Nut_2020_M042.Edge6,T_Nut_2020_M042.Edge6]
FEATURE [App::FeaturePython] Joint100  label="Slider049"  # Assembly joint (typed FeaturePython)
  Activated = true
  AngleMax = 0
  AngleMin = 0
  Detach1 = false
  Detach2 = false
  Distance = 0
  Distance2 = 0
  EnableAngleMax = false
  EnableAngleMin = false
  EnableLengthMax = false
  EnableLengthMin = false
  JointType = 3 (Slider)
  LengthMax = 0
  LengthMin = 0
  Placement1 = pos=(-3,-3.6e-15,0) rot=(-0.57735,-0.57735,0.57735;4.18879rad)
  Placement2 = pos=(-8,-3.1,0) rot=(0,0,1;0rad)
  Reference1 = -> Assembly [T_Nut_2020_M041.Edge27,T_Nut_2020_M041.Edge27]
  Reference2 = -> Assembly [Tslot20_heigh001.Edge109,Tslot20_heigh001.Vertex37]
FEATURE [App::FeaturePython] Joint101  label="Fixed050"  # Assembly joint (typed FeaturePython)
  Activated = true
  AngleMax = 0
  AngleMin = 0
  Detach1 = false
  Detach2 = false
  Distance = 0
  Distance2 = 0
  EnableAngleMax = false
  EnableAngleMin = false
  EnableLengthMax = false
  EnableLengthMin = false
  JointType = 0 (Fixed)
  LengthMax = 0
  LengthMin = 0
  Offset2 = pos=(0,0,-6) rot=(0,0,1;0rad)
  Placement1 = pos=(-6.98683,35.5575,-5.68e-14) rot=(0,0,1;0rad)
  Placement2 = pos=(-7e-16,-6.7e-15,-5.4) rot=(0,0,1;0rad)
  Reference1 = -> Assembly [Hex_screw_M5_10_021.Edge2,Hex_screw_M5_10_021.Edge2]
  Reference2 = -> Assembly [T_Nut_2020_M041.Edge6,T_Nut_2020_M041.Edge6]
FEATURE [App::Link] T_Nut_2020_M045  label="T-Nut_2020_M045"
  LinkPlacement = pos=(21.8283,220.1,562) rot=(0.707107,-0.707107,0;3.14159rad)
  LinkedObject = -> <external ../parts/T-nut_20.FCStd>#Part__Feature
  Placement = pos=(21.8283,220.1,562) rot=(0.707107,-0.707107,0;3.14159rad)
FEATURE [App::Link] T_Nut_2020_M046  label="T-Nut_2020_M046"
  LinkPlacement = pos=(0.1,198.275,562) rot=(0,1,0;3.14159rad)
  LinkedObject = -> <external ../parts/T-nut_20.FCStd>#Part__Feature
  Placement = pos=(0.1,198.275,562) rot=(0,1,0;3.14159rad)
FEATURE [App::FeaturePython] Joint102  label="Slider050"  # Assembly joint (typed FeaturePython)
  Activated = true
  AngleMax = 0
  AngleMin = 0
  Detach1 = false
  Detach2 = false
  Distance = 0
  Distance2 = 0
  EnableAngleMax = false
  EnableAngleMin = false
  EnableLengthMax = false
  EnableLengthMin = false
  JointType = 3 (Slider)
  LengthMax = 0
  LengthMin = 0
  Placement1 = pos=(-3,0,0) rot=(-0.57735,-0.57735,0.57735;4.18879rad)
  Placement2 = pos=(-8,3.1,200) rot=(0,0,1;0rad)
  Reference1 = -> Assembly [T_Nut_2020_M046.Edge27,T_Nut_2020_M046.Edge27]
  Reference2 = -> Assembly [Tslot20_wid.Edge104,Tslot20_wid.Vertex67]
FEATURE [App::FeaturePython] Joint103  label="Slider051"  # Assembly joint (typed FeaturePython)
  Activated = true
  AngleMax = 0
  AngleMin = 0
  Detach1 = false
  Detach2 = false
  Distance = 0
  Distance2 = 0
  EnableAngleMax = false
  EnableAngleMin = false
  EnableLengthMax = false
  EnableLengthMin = false
  JointType = 3 (Slider)
  LengthMax = 0
  LengthMin = 0
  Offset2 = pos=(0,0,0) rot=(0,0,1;3.14159rad)
  Placement1 = pos=(-3,0,0) rot=(-0.57735,-0.57735,0.57735;4.18879rad)
  Placement2 = pos=(8,3.1,0) rot=(0,0,1;3.14159rad)
  Reference1 = -> Assembly [T_Nut_2020_M045.Edge27,T_Nut_2020_M045.Edge27]
  Reference2 = -> Assembly [Tslot20_len001.Edge95,Tslot20_len001.Vertex21]
FEATURE [App::Link] Hex_screw_M5_10_025  label="Hex screw M5 10.025"
  LinkPlacement = pos=(57.3858,213.113,567.4) rot=(0.707107,-0.707107,0;3.14159rad)
  LinkedObject = -> <external ../secondary/bolts.FCStd>#Body004
  Placement = pos=(57.3858,213.113,567.4) rot=(0.707107,-0.707107,0;3.14159rad)
FEATURE [App::Link] Hex_screw_M5_10_026  label="Hex screw M5 10.026"
  LinkPlacement = pos=(-6.88683,162.717,567.4) rot=(0,1,0;3.14159rad)
  LinkedObject = -> <external ../secondary/bolts.FCStd>#Body004
  Placement = pos=(-6.88683,162.717,567.4) rot=(0,1,0;3.14159rad)
FEATURE [App::FeaturePython] Joint104  label="Fixed051"  # Assembly joint (typed FeaturePython)
  Activated = true
  AngleMax = 0
  AngleMin = 0
  Detach1 = false
  Detach2 = false
  Distance = 0
  Distance2 = 0
  EnableAngleMax = false
  EnableAngleMin = false
  EnableLengthMax = false
  EnableLengthMin = false
  JointType = 0 (Fixed)
  LengthMax = 0
  LengthMin = 0
  Offset2 = pos=(0,0,-6) rot=(0,0,1;0rad)
  Placement1 = pos=(-6.98683,35.5575,0) rot=(0,0,1;0rad)
  Placement2 = pos=(0,-6.7e-15,-5.4) rot=(0,0,1;0rad)
  Reference1 = -> Assembly [Hex_screw_M5_10_026.Edge2,Hex_screw_M5_10_026.Edge2]
  Reference2 = -> Assembly [T_Nut_2020_M046.Edge6,T_Nut_2020_M046.Edge6]
FEATURE [App::FeaturePython] Joint105  label="Fixed052"  # Assembly joint (typed FeaturePython)
  Activated = true
  AngleMax = 0
  AngleMin = 0
  Detach1 = false
  Detach2 = false
  Distance = 0
  Distance2 = 0
  EnableAngleMax = false
  EnableAngleMin = false
  EnableLengthMax = false
  EnableLengthMin = false
  JointType = 0 (Fixed)
  LengthMax = 0
  LengthMin = 0
  Offset2 = pos=(0,0,-6) rot=(0,0,1;0rad)
  Placement1 = pos=(-6.98683,35.5575,1.137e-13) rot=(0,0,1;0rad)
  Placement2 = pos=(0,-6.7e-15,-5.4) rot=(0,0,1;0rad)
  Reference1 = -> Assembly [Hex_screw_M5_10_025.Edge2,Hex_screw_M5_10_025.Edge2]
  Reference2 = -> Assembly [T_Nut_2020_M045.Edge6,T_Nut_2020_M045.Edge6]
FEATURE [App::Link] T_Nut_2020_M047  label="T-Nut_2020_M047"
  LinkPlacement = pos=(21.8772,0.1,562) rot=(0.707107,0.707107,0;3.14159rad)
  LinkedObject = -> <external ../parts/T-nut_20.FCStd>#Part__Feature
  Placement = pos=(21.8772,0.1,562) rot=(0.707107,0.707107,0;3.14159rad)
FEATURE [App::Link] T_Nut_2020_M048  label="T-Nut_2020_M048"
  LinkPlacement = pos=(0.1,21.7161,562) rot=(0,1,0;3.14159rad)
  LinkedObject = -> <external ../parts/T-nut_20.FCStd>#Part__Feature
  Placement = pos=(0.1,21.7161,562) rot=(0,1,0;3.14159rad)
FEATURE [App::FeaturePython] Joint106  label="Slider052"  # Assembly joint (typed FeaturePython)
  Activated = true
  AngleMax = 0
  AngleMin = 0
  Detach1 = false
  Detach2 = false
  Distance = 0
  Distance2 = 0
  EnableAngleMax = false
  EnableAngleMin = false
  EnableLengthMax = false
  EnableLengthMin = false
  JointType = 3 (Slider)
  LengthMax = 0
  LengthMin = 0
  Offset2 = pos=(0,0,0) rot=(0,0,1;3.14159rad)
  Placement1 = pos=(3,0,0) rot=(-0.57735,-0.57735,0.57735;4.18879rad)
  Placement2 = pos=(8,3.1,0) rot=(0,0,1;3.14159rad)
  Reference1 = -> Assembly [T_Nut_2020_M047.Edge8,T_Nut_2020_M047.Edge8]
  Reference2 = -> Assembly [Tslot20_len.Edge95,Tslot20_len.Vertex21]
FEATURE [App::FeaturePython] Joint107  label="Slider053"  # Assembly joint (typed FeaturePython)
  Activated = true
  AngleMax = 0
  AngleMin = 0
  Detach1 = false
  Detach2 = false
  Distance = 0
  Distance2 = 0
  EnableAngleMax = false
  EnableAngleMin = false
  EnableLengthMax = false
  EnableLengthMin = false
  JointType = 3 (Slider)
  LengthMax = 0
  LengthMin = 0
  Placement1 = pos=(-3,0,0) rot=(-0.57735,-0.57735,0.57735;4.18879rad)
  Placement2 = pos=(-8,3.1,0) rot=(0,0,1;0rad)
  Reference1 = -> Assembly [T_Nut_2020_M048.Edge27,T_Nut_2020_M048.Edge27]
  Reference2 = -> Assembly [Tslot20_wid.Edge104,Tslot20_wid.Vertex32]
FEATURE [App::Link] Hex_screw_M5_10_029  label="Hex screw M5 10.027"
  LinkPlacement = pos=(-6.88683,-13.8415,567.4) rot=(0,1,0;3.14159rad)
  LinkedObject = -> <external ../secondary/bolts.FCStd>#Body004
  Placement = pos=(-6.88683,-13.8415,567.4) rot=(0,1,0;3.14159rad)
FEATURE [App::Link] Hex_screw_M5_10_028  label="Hex screw M5 10.028"
  LinkPlacement = pos=(-13.6803,7.08683,567.4) rot=(0.707107,0.707107,0;3.14159rad)
  LinkedObject = -> <external ../secondary/bolts.FCStd>#Body004
  Placement = pos=(-13.6803,7.08683,567.4) rot=(0.707107,0.707107,0;3.14159rad)
FEATURE [App::Link] Hex_screw_M5_10_030  label="Hex screw M5 10.029"
  LinkPlacement = pos=(362.753,227.087,567.4) rot=(0.707107,0.707107,0;3.14159rad)
  LinkedObject = -> <external ../secondary/bolts.FCStd>#Body004
  Placement = pos=(362.753,227.087,567.4) rot=(0.707107,0.707107,0;3.14159rad)
FEATURE [App::FeaturePython] Joint108  label="Fixed053"  # Assembly joint (typed FeaturePython)
  Activated = true
  AngleMax = 0
  AngleMin = 0
  Detach1 = false
  Detach2 = false
  Distance = 0
  Distance2 = 0
  EnableAngleMax = false
  EnableAngleMin = false
  EnableLengthMax = false
  EnableLengthMin = false
  JointType = 0 (Fixed)
  LengthMax = 0
  LengthMin = 0
  Offset2 = pos=(0,0,-6) rot=(0,0,1;0rad)
  Placement1 = pos=(-6.98683,35.5575,0) rot=(0,0,1;0rad)
  Placement2 = pos=(0,-6.7e-15,-5.4) rot=(0,0,1;0rad)
  Reference1 = -> Assembly [Hex_screw_M5_10_029.Edge2,Hex_screw_M5_10_029.Edge2]
  Reference2 = -> Assembly [T_Nut_2020_M048.Edge6,T_Nut_2020_M048.Edge6]
FEATURE [App::FeaturePython] Joint109  label="Fixed054"  # Assembly joint (typed FeaturePython)
  Activated = true
  AngleMax = 0
  AngleMin = 0
  Detach1 = false
  Detach2 = false
  Distance = 0
  Distance2 = 0
  EnableAngleMax = false
  EnableAngleMin = false
  EnableLengthMax = false
  EnableLengthMin = false
  JointType = 0 (Fixed)
  LengthMax = 0
  LengthMin = 0
  Offset2 = pos=(0,0,-6) rot=(0,0,1;0rad)
  Placement1 = pos=(-6.98683,35.5575,0) rot=(0,0,1;0rad)
  Placement2 = pos=(0,-6.7e-15,-5.4) rot=(0,0,1;0rad)
  Reference1 = -> Assembly [Hex_screw_M5_10_028.Edge2,Hex_screw_M5_10_028.Edge2]
  Reference2 = -> Assembly [T_Nut_2020_M047.Edge6,T_Nut_2020_M047.Edge6]
FEATURE [App::Link] T_Nut_2020_M049  label="T-Nut_2020_M049"
  LinkPlacement = pos=(419.9,198.358,562) rot=(1,0,0;3.14159rad)
  LinkedObject = -> <external ../parts/T-nut_20.FCStd>#Part__Feature
  Placement = pos=(419.9,198.358,562) rot=(1,0,0;3.14159rad)
FEATURE [App::Link] T_Nut_2020_M050  label="T-Nut_2020_M050"
  LinkPlacement = pos=(398.311,220.1,562) rot=(0.707107,0.707107,0;3.14159rad)
  LinkedObject = -> <external ../parts/T-nut_20.FCStd>#Part__Feature
  Placement = pos=(398.311,220.1,562) rot=(0.707107,0.707107,0;3.14159rad)
FEATURE [App::FeaturePython] Joint110  label="Slider054"  # Assembly joint (typed FeaturePython)
  Activated = true
  AngleMax = 0
  AngleMin = 0
  Detach1 = false
  Detach2 = false
  Distance = 0
  Distance2 = 0
  EnableAngleMax = false
  EnableAngleMin = false
  EnableLengthMax = false
  EnableLengthMin = false
  JointType = 3 (Slider)
  LengthMax = 0
  LengthMin = 0
  Offset2 = pos=(0,0,0) rot=(0,0,1;3.14159rad)
  Placement1 = pos=(3,0,0) rot=(-0.57735,-0.57735,0.57735;4.18879rad)
  Placement2 = pos=(8,3.1,400) rot=(0,0,1;3.14159rad)
  Reference1 = -> Assembly [T_Nut_2020_M050.Edge8,T_Nut_2020_M050.Edge8]
  Reference2 = -> Assembly [Tslot20_len001.Edge95,Tslot20_len001.Vertex57]
FEATURE [App::FeaturePython] Joint111  label="Slider055"  # Assembly joint (typed FeaturePython)
  Activated = true
  AngleMax = 0
  AngleMin = 0
  Detach1 = false
  Detach2 = false
  Distance = 0
  Distance2 = 0
  EnableAngleMax = false
  EnableAngleMin = false
  EnableLengthMax = false
  EnableLengthMin = false
  JointType = 3 (Slider)
  LengthMax = 0
  LengthMin = 0
  Offset2 = pos=(0,0,0) rot=(0,0,-1;1.5708rad)
  Placement1 = pos=(-3,0,0) rot=(-0.57735,-0.57735,0.57735;4.18879rad)
  Placement2 = pos=(-3.1,8,200) rot=(-0.707107,0.707107,0;3.14159rad)
  Reference1 = -> Assembly [T_Nut_2020_M049.Edge27,T_Nut_2020_M049.Edge27]
  Reference2 = -> Assembly [Tslot20_wid001.Edge42,Tslot20_wid001.Vertex40]
FEATURE [App::Link] Hex_screw_M5_10_031  label="Hex screw M5 10.030"
  LinkPlacement = pos=(426.887,233.915,567.4) rot=(1,0,0;3.14159rad)
  LinkedObject = -> <external ../secondary/bolts.FCStd>#Body004
  Placement = pos=(426.887,233.915,567.4) rot=(1,0,0;3.14159rad)
FEATURE [App::Link] Hex_screw_M5_10_032  label="Hex screw M5 10.031"
  LinkPlacement = pos=(433.922,-7.08683,567.4) rot=(0.707107,-0.707107,0;3.14159rad)
  LinkedObject = -> <external ../secondary/bolts.FCStd>#Body004
  Placement = pos=(433.922,-7.08683,567.4) rot=(0.707107,-0.707107,0;3.14159rad)
FEATURE [App::FeaturePython] Joint112  label="Fixed055"  # Assembly joint (typed FeaturePython)
  Activated = true
  AngleMax = 0
  AngleMin = 0
  Detach1 = false
  Detach2 = false
  Distance = 0
  Distance2 = 0
  EnableAngleMax = false
  EnableAngleMin = false
  EnableLengthMax = false
  EnableLengthMin = false
  JointType = 0 (Fixed)
  LengthMax = 0
  LengthMin = 0
  Offset2 = pos=(0,0,-6) rot=(0,0,1;0rad)
  Placement1 = pos=(-6.98683,35.5575,1.137e-13) rot=(0,0,1;0rad)
  Placement2 = pos=(0,-6.7e-15,-5.4) rot=(0,0,1;0rad)
  Reference1 = -> Assembly [Hex_screw_M5_10_030.Edge2,Hex_screw_M5_10_030.Edge2]
  Reference2 = -> Assembly [T_Nut_2020_M050.Edge6,T_Nut_2020_M050.Edge6]
FEATURE [App::FeaturePython] Joint113  label="Fixed056"  # Assembly joint (typed FeaturePython)
  Activated = true
  AngleMax = 0
  AngleMin = 0
  Detach1 = false
  Detach2 = false
  Distance = 0
  Distance2 = 0
  EnableAngleMax = false
  EnableAngleMin = false
  EnableLengthMax = false
  EnableLengthMin = false
  JointType = 0 (Fixed)
  LengthMax = 0
  LengthMin = 0
  Offset2 = pos=(0,0,-6) rot=(0,0,1;0rad)
  Placement1 = pos=(-6.98683,35.5575,0) rot=(0,0,1;0rad)
  Placement2 = pos=(0,-6.7e-15,-5.4) rot=(0,0,1;0rad)
  Reference1 = -> Assembly [Hex_screw_M5_10_031.Edge2,Hex_screw_M5_10_031.Edge2]
  Reference2 = -> Assembly [T_Nut_2020_M049.Edge6,T_Nut_2020_M049.Edge6]
FEATURE [App::Link] T_Nut_2020_M051  label="T-Nut_2020_M051"
  LinkPlacement = pos=(420.1,21.6929,562) rot=(1,0,0;3.14159rad)
  LinkedObject = -> <external ../parts/T-nut_20.FCStd>#Part__Feature
  Placement = pos=(420.1,21.6929,562) rot=(1,0,0;3.14159rad)
FEATURE [App::Link] T_Nut_2020_M052  label="T-Nut_2020_M052"
  LinkPlacement = pos=(398.365,-0.1,562) rot=(0.707107,-0.707107,0;3.14159rad)
  LinkedObject = -> <external ../parts/T-nut_20.FCStd>#Part__Feature
  Placement = pos=(398.365,-0.1,562) rot=(0.707107,-0.707107,0;3.14159rad)
FEATURE [App::FeaturePython] Joint114  label="Slider056"  # Assembly joint (typed FeaturePython)
  Activated = true
  AngleMax = 0
  AngleMin = 0
  Detach1 = false
  Detach2 = false
  Distance = 0
  Distance2 = 0
  EnableAngleMax = false
  EnableAngleMin = false
  EnableLengthMax = false
  EnableLengthMin = false
  JointType = 3 (Slider)
  LengthMax = 0
  LengthMin = 0
  Offset2 = pos=(0,0,0) rot=(0,0,1;3.14159rad)
  Placement1 = pos=(3,0,0) rot=(-0.57735,-0.57735,0.57735;4.18879rad)
  Placement2 = pos=(8,-3.1,400) rot=(0,0,1;3.14159rad)
  Reference1 = -> Assembly [T_Nut_2020_M052.Edge8,T_Nut_2020_M052.Edge8]
  Reference2 = -> Assembly [Tslot20_len.Edge90,Tslot20_len.Vertex52]
FEATURE [App::FeaturePython] Joint115  label="Slider057"  # Assembly joint (typed FeaturePython)
  Activated = true
  AngleMax = 0
  AngleMin = 0
  Detach1 = false
  Detach2 = false
  Distance = 0
  Distance2 = 0
  EnableAngleMax = false
  EnableAngleMin = false
  EnableLengthMax = false
  EnableLengthMin = false
  JointType = 3 (Slider)
  LengthMax = 0
  LengthMin = 0
  Offset2 = pos=(0,0,0) rot=(0,0,-1;1.5708rad)
  Placement1 = pos=(3,0,0) rot=(-0.57735,-0.57735,0.57735;4.18879rad)
  Placement2 = pos=(3.1,8,0) rot=(-0.707107,0.707107,0;3.14159rad)
  Reference1 = -> Assembly [T_Nut_2020_M051.Edge8,T_Nut_2020_M051.Edge8]
  Reference2 = -> Assembly [Tslot20_wid001.Edge99,Tslot20_wid001.Vertex25]
FEATURE [App::Link] Hex_screw_M5_10_033  label="Hex screw M5 10.032"
  LinkPlacement = pos=(427.087,57.2505,567.4) rot=(1,0,0;3.14159rad)
  LinkedObject = -> <external ../secondary/bolts.FCStd>#Body004
  Placement = pos=(427.087,57.2505,567.4) rot=(1,0,0;3.14159rad)
FEATURE [App::Link] Hex_screw_M5_10_034  label="Hex screw M5 10.033"
  LinkPlacement = pos=(2.6,-7.08683,603.883) rot=(0.57735,-0.57735,0.57735;4.18879rad)
  LinkedObject = -> <external ../secondary/bolts.FCStd>#Body004
  Placement = pos=(2.6,-7.08683,603.883) rot=(0.57735,-0.57735,0.57735;4.18879rad)
FEATURE [App::FeaturePython] Joint116  label="Fixed057"  # Assembly joint (typed FeaturePython)
  Activated = true
  AngleMax = 0
  AngleMin = 0
  Detach1 = false
  Detach2 = false
  Distance = 0
  Distance2 = 0
  EnableAngleMax = false
  EnableAngleMin = false
  EnableLengthMax = false
  EnableLengthMin = false
  JointType = 0 (Fixed)
  LengthMax = 0
  LengthMin = 0
  Offset2 = pos=(0,0,-6) rot=(0,0,1;0rad)
  Placement1 = pos=(-6.98683,35.5575,0) rot=(0,0,1;0rad)
  Placement2 = pos=(0,-6.7e-15,-5.4) rot=(0,0,1;0rad)
  Reference1 = -> Assembly [Hex_screw_M5_10_033.Edge2,Hex_screw_M5_10_033.Edge2]
  Reference2 = -> Assembly [T_Nut_2020_M051.Edge6,T_Nut_2020_M051.Edge6]
FEATURE [App::FeaturePython] Joint117  label="Fixed058"  # Assembly joint (typed FeaturePython)
  Activated = true
  AngleMax = 0
  AngleMin = 0
  Detach1 = false
  Detach2 = false
  Distance = 0
  Distance2 = 0
  EnableAngleMax = false
  EnableAngleMin = false
  EnableLengthMax = false
  EnableLengthMin = false
  JointType = 0 (Fixed)
  LengthMax = 0
  LengthMin = 0
  Offset2 = pos=(0,0,-6) rot=(0,0,1;0rad)
  Placement1 = pos=(-6.98683,35.5575,0) rot=(0,0,1;0rad)
  Placement2 = pos=(0,-6.7e-15,-5.4) rot=(0,0,1;0rad)
  Reference1 = -> Assembly [Hex_screw_M5_10_032.Edge2,Hex_screw_M5_10_032.Edge2]
  Reference2 = -> Assembly [T_Nut_2020_M052.Edge6,T_Nut_2020_M052.Edge6]
FEATURE [App::Link] T_Nut_2020_M053  label="T-Nut_2020_M053"
  LinkPlacement = pos=(8,-0.1,568.325) rot=(-0.57735,0.57735,-0.57735;2.0944rad)
  LinkedObject = -> <external ../parts/T-nut_20.FCStd>#Part__Feature
  Placement = pos=(8,-0.1,568.325) rot=(-0.57735,0.57735,-0.57735;2.0944rad)
FEATURE [App::Link] T_Nut_2020_M054  label="T-Nut_2020_M054"
  LinkPlacement = pos=(0.1,8,568.328) rot=(0,0.707107,0.707107;3.14159rad)
  LinkedObject = -> <external ../parts/T-nut_20.FCStd>#Part__Feature
  Placement = pos=(0.1,8,568.328) rot=(0,0.707107,0.707107;3.14159rad)
FEATURE [App::Link] Hex_screw_M5_10_035  label="Hex screw M5 10.034"
  LinkPlacement = pos=(-6.88683,2.6,532.77) rot=(0,0.707107,0.707107;3.14159rad)
  LinkedObject = -> <external ../secondary/bolts.FCStd>#Body004
  Placement = pos=(-6.88683,2.6,532.77) rot=(0,0.707107,0.707107;3.14159rad)
FEATURE [App::Link] Hex_screw_M5_10_036  label="Hex screw M5 10.035"
  LinkPlacement = pos=(2.6,226.887,532.521) rot=(0.57735,0.57735,0.57735;2.0944rad)
  LinkedObject = -> <external ../secondary/bolts.FCStd>#Body004
  Placement = pos=(2.6,226.887,532.521) rot=(0.57735,0.57735,0.57735;2.0944rad)
FEATURE [App::FeaturePython] Joint118  label="Slider058"  # Assembly joint (typed FeaturePython)
  Activated = true
  AngleMax = 0
  AngleMin = 0
  Detach1 = false
  Detach2 = false
  Distance = 0
  Distance2 = 0
  EnableAngleMax = false
  EnableAngleMin = false
  EnableLengthMax = false
  EnableLengthMin = false
  JointType = 3 (Slider)
  LengthMax = 0
  LengthMin = 0
  Offset2 = pos=(0,0,0) rot=(0,0,-1;1.5708rad)
  Placement1 = pos=(-3,0,0) rot=(-0.57735,-0.57735,0.57735;4.18879rad)
  Placement2 = pos=(3.1,8,580) rot=(-0.707107,0.707107,0;3.14159rad)
  Reference1 = -> Assembly [T_Nut_2020_M054.Edge27,T_Nut_2020_M054.Edge27]
  Reference2 = -> Assembly [Tslot20_heigh.Edge99,Tslot20_heigh.Vertex61]
FEATURE [App::FeaturePython] Joint119  label="Slider059"  # Assembly joint (typed FeaturePython)
  Activated = true
  AngleMax = 0
  AngleMin = 0
  Detach1 = false
  Detach2 = false
  Distance = 0
  Distance2 = 0
  EnableAngleMax = false
  EnableAngleMin = false
  EnableLengthMax = false
  EnableLengthMin = false
  JointType = 3 (Slider)
  LengthMax = 0
  LengthMin = 0
  Offset2 = pos=(0,0,0) rot=(0,0,1;3.14159rad)
  Placement1 = pos=(3,0,0) rot=(-0.57735,-0.57735,0.57735;4.18879rad)
  Placement2 = pos=(8,-3.1,580) rot=(0,0,1;3.14159rad)
  Reference1 = -> Assembly [T_Nut_2020_M053.Edge8,T_Nut_2020_M053.Edge8]
  Reference2 = -> Assembly [Tslot20_heigh.Edge90,Tslot20_heigh.Vertex52]
FEATURE [App::FeaturePython] Joint120  label="Fixed059"  # Assembly joint (typed FeaturePython)
  Activated = true
  AngleMax = 0
  AngleMin = 0
  Detach1 = false
  Detach2 = false
  Distance = 0
  Distance2 = 0
  EnableAngleMax = false
  EnableAngleMin = false
  EnableLengthMax = false
  EnableLengthMin = false
  JointType = 0 (Fixed)
  LengthMax = 0
  LengthMin = 0
  Offset2 = pos=(0,0,-6) rot=(0,0,1;0rad)
  Placement1 = pos=(-6.98683,35.5575,9e-16) rot=(0,0,1;0rad)
  Placement2 = pos=(6e-16,-6.3e-15,-5.4) rot=(0,0,1;0rad)
  Reference1 = -> Assembly [Hex_screw_M5_10_034.Edge2,Hex_screw_M5_10_034.Edge2]
  Reference2 = -> Assembly [T_Nut_2020_M053.Edge6,T_Nut_2020_M053.Edge6]
FEATURE [App::FeaturePython] Joint121  label="Fixed060"  # Assembly joint (typed FeaturePython)
  Activated = true
  AngleMax = 0
  AngleMin = 0
  Detach1 = false
  Detach2 = false
  Distance = 0
  Distance2 = 0
  EnableAngleMax = false
  EnableAngleMin = false
  EnableLengthMax = false
  EnableLengthMin = false
  JointType = 0 (Fixed)
  LengthMax = 0
  LengthMin = 0
  Offset2 = pos=(0,0,-6) rot=(0,0,1;0rad)
  Placement1 = pos=(-6.98683,35.5575,0) rot=(0,0,1;0rad)
  Placement2 = pos=(0,-6.7e-15,-5.4) rot=(0,0,1;0rad)
  Reference1 = -> Assembly [Hex_screw_M5_10_035.Edge2,Hex_screw_M5_10_035.Edge2]
  Reference2 = -> Assembly [T_Nut_2020_M054.Edge6,T_Nut_2020_M054.Edge6]
FEATURE [App::Link] T_Nut_2020_M055  label="T-Nut_2020_M055"
  LinkPlacement = pos=(0.1,212,568.222) rot=(1,0,0;1.5708rad)
  LinkedObject = -> <external ../parts/T-nut_20.FCStd>#Part__Feature
  Placement = pos=(0.1,212,568.222) rot=(1,0,0;1.5708rad)
FEATURE [App::Link] T_Nut_2020_M056  label="T-Nut_2020_M056"
  LinkPlacement = pos=(8,219.9,568.078) rot=(0.57735,0.57735,0.57735;2.0944rad)
  LinkedObject = -> <external ../parts/T-nut_20.FCStd>#Part__Feature
  Placement = pos=(8,219.9,568.078) rot=(0.57735,0.57735,0.57735;2.0944rad)
FEATURE [App::FeaturePython] Joint122  label="Slider060"  # Assembly joint (typed FeaturePython)
  Activated = true
  AngleMax = 0
  AngleMin = 0
  Detach1 = false
  Detach2 = false
  Distance = 0
  Distance2 = 0
  EnableAngleMax = false
  EnableAngleMin = false
  EnableLengthMax = false
  EnableLengthMin = false
  JointType = 3 (Slider)
  LengthMax = 0
  LengthMin = 0
  Offset2 = pos=(0,0,0) rot=(0,0,1;1.5708rad)
  Placement1 = pos=(3,0,0) rot=(-0.57735,-0.57735,0.57735;4.18879rad)
  Placement2 = pos=(3.1,-8,580) rot=(0.707107,0.707107,0;3.14159rad)
  Reference1 = -> Assembly [T_Nut_2020_M055.Edge8,T_Nut_2020_M055.Edge8]
  Reference2 = -> Assembly [Tslot20_heigh002.Edge86,Tslot20_heigh002.Vertex48]
FEATURE [App::FeaturePython] Joint123  label="Slider061"  # Assembly joint (typed FeaturePython)
  Activated = true
  AngleMax = 0
  AngleMin = 0
  Detach1 = false
  Detach2 = false
  Distance = 0
  Distance2 = 0
  EnableAngleMax = false
  EnableAngleMin = false
  EnableLengthMax = false
  EnableLengthMin = false
  JointType = 3 (Slider)
  LengthMax = 0
  LengthMin = 0
  Offset2 = pos=(0,0,0) rot=(0,0,1;3.14159rad)
  Placement1 = pos=(-3,0,9e-16) rot=(-0.57735,-0.57735,0.57735;4.18879rad)
  Placement2 = pos=(8,-3.1,580) rot=(0,0,1;3.14159rad)
  Reference1 = -> Assembly [T_Nut_2020_M056.Edge27,T_Nut_2020_M056.Edge27]
  Reference2 = -> Assembly [Tslot20_heigh002.Edge90,Tslot20_heigh002.Vertex52]
FEATURE [App::Link] Hex_screw_M5_10_037  label="Hex screw M5 10.036"
  LinkPlacement = pos=(7.08683,217.4,532.665) rot=(1,0,0;1.5708rad)
  LinkedObject = -> <external ../secondary/bolts.FCStd>#Body004
  Placement = pos=(7.08683,217.4,532.665) rot=(1,0,0;1.5708rad)
FEATURE [App::Link] Hex_screw_M5_10_038  label="Hex screw M5 10.037"
  LinkPlacement = pos=(417.4,6.88683,603.965) rot=(-0.57735,-0.57735,0.57735;2.0944rad)
  LinkedObject = -> <external ../secondary/bolts.FCStd>#Body004
  Placement = pos=(417.4,6.88683,603.965) rot=(-0.57735,-0.57735,0.57735;2.0944rad)
FEATURE [App::FeaturePython] Joint124  label="Fixed061"  # Assembly joint (typed FeaturePython)
  Activated = true
  AngleMax = 0
  AngleMin = 0
  Detach1 = false
  Detach2 = false
  Distance = 0
  Distance2 = 0
  EnableAngleMax = false
  EnableAngleMin = false
  EnableLengthMax = false
  EnableLengthMin = false
  JointType = 0 (Fixed)
  LengthMax = 0
  LengthMin = 0
  Offset2 = pos=(0,0,-6) rot=(0,0,1;0rad)
  Placement1 = pos=(-6.98683,35.5575,1.3e-15) rot=(0,0,1;0rad)
  Placement2 = pos=(-2e-15,-6.7e-15,-5.4) rot=(0,0,1;0rad)
  Reference1 = -> Assembly [Hex_screw_M5_10_036.Edge2,Hex_screw_M5_10_036.Edge2]
  Reference2 = -> Assembly [T_Nut_2020_M056.Edge6,T_Nut_2020_M056.Edge6]
FEATURE [App::FeaturePython] Joint125  label="Fixed062"  # Assembly joint (typed FeaturePython)
  Activated = true
  AngleMax = 0
  AngleMin = 0
  Detach1 = false
  Detach2 = false
  Distance = 0
  Distance2 = 0
  EnableAngleMax = false
  EnableAngleMin = false
  EnableLengthMax = false
  EnableLengthMin = false
  JointType = 0 (Fixed)
  LengthMax = 0
  LengthMin = 0
  Offset2 = pos=(0,0,-6) rot=(0,0,1;0rad)
  Placement1 = pos=(-6.98683,35.5575,-2.84e-14) rot=(0,0,1;0rad)
  Placement2 = pos=(0,-6.7e-15,-5.4) rot=(0,0,1;0rad)
  Reference1 = -> Assembly [Hex_screw_M5_10_037.Edge2,Hex_screw_M5_10_037.Edge2]
  Reference2 = -> Assembly [T_Nut_2020_M055.Edge6,T_Nut_2020_M055.Edge6]
FEATURE [App::Link] T_Nut_2020_M057  label="T-Nut_2020_M057"
  LinkPlacement = pos=(419.9,8,568.405) rot=(1,0,0;4.71239rad)
  LinkedObject = -> <external ../parts/T-nut_20.FCStd>#Part__Feature
  Placement = pos=(419.9,8,568.405) rot=(1,0,0;4.71239rad)
FEATURE [App::Link] T_Nut_2020_M058  label="T-Nut_2020_M058"
  LinkPlacement = pos=(412,-0.1,568.408) rot=(0.57735,0.57735,-0.57735;4.18879rad)
  LinkedObject = -> <external ../parts/T-nut_20.FCStd>#Part__Feature
  Placement = pos=(412,-0.1,568.408) rot=(0.57735,0.57735,-0.57735;4.18879rad)
FEATURE [App::FeaturePython] Joint126  label="Slider062"  # Assembly joint (typed FeaturePython)
  Activated = true
  AngleMax = 0
  AngleMin = 0
  Detach1 = false
  Detach2 = false
  Distance = 0
  Distance2 = 0
  EnableAngleMax = false
  EnableAngleMin = false
  EnableLengthMax = false
  EnableLengthMin = false
  JointType = 3 (Slider)
  LengthMax = 0
  LengthMin = 0
  Placement1 = pos=(-3,0,0) rot=(-0.57735,-0.57735,0.57735;4.18879rad)
  Placement2 = pos=(-8,-3.1,580) rot=(0,0,1;0rad)
  Reference1 = -> Assembly [T_Nut_2020_M058.Edge27,T_Nut_2020_M058.Edge27]
  Reference2 = -> Assembly [Tslot20_heigh001.Edge109,Tslot20_heigh001.Vertex72]
FEATURE [App::FeaturePython] Joint127  label="Slider063"  # Assembly joint (typed FeaturePython)
  Activated = true
  AngleMax = 0
  AngleMin = 0
  Detach1 = false
  Detach2 = false
  Distance = 0
  Distance2 = 0
  EnableAngleMax = false
  EnableAngleMin = false
  EnableLengthMax = false
  EnableLengthMin = false
  JointType = 3 (Slider)
  LengthMax = 0
  LengthMin = 0
  Offset2 = pos=(0,0,0) rot=(0,0,-1;1.5708rad)
  Placement1 = pos=(-3,-5.25,8e-15) rot=(-0.57735,-0.57735,0.57735;4.18879rad)
  Placement2 = pos=(-3.1,8,580) rot=(-0.707107,0.707107,0;3.14159rad)
  Reference1 = -> Assembly [T_Nut_2020_M057.Edge27,T_Nut_2020_M057.Vertex17]
  Reference2 = -> Assembly [Tslot20_heigh001.Edge42,Tslot20_heigh001.Vertex40]
FEATURE [App::Link] Hex_screw_M5_10_039  label="Hex screw M5 10.038"
  LinkPlacement = pos=(426.887,2.6,603.963) rot=(-1,0,0;1.5708rad)
  LinkedObject = -> <external ../secondary/bolts.FCStd>#Body004
  Placement = pos=(426.887,2.6,603.963) rot=(-1,0,0;1.5708rad)
FEATURE [App::Link] Hex_screw_M5_10_040  label="Hex screw M5 10.039"
  LinkPlacement = pos=(426.887,217.4,533.117) rot=(1,0,0;1.5708rad)
  LinkedObject = -> <external ../secondary/bolts.FCStd>#Body004
  Placement = pos=(426.887,217.4,533.117) rot=(1,0,0;1.5708rad)
FEATURE [App::FeaturePython] Joint128  label="Fixed063"  # Assembly joint (typed FeaturePython)
  Activated = true
  AngleMax = 0
  AngleMin = 0
  Detach1 = false
  Detach2 = false
  Distance = 0
  Distance2 = 0
  EnableAngleMax = false
  EnableAngleMin = false
  EnableLengthMax = false
  EnableLengthMin = false
  JointType = 0 (Fixed)
  LengthMax = 0
  LengthMin = 0
  Offset2 = pos=(0,0,-6) rot=(0,0,1;0rad)
  Placement1 = pos=(-6.98683,35.5575,0) rot=(0,0,1;0rad)
  Placement2 = pos=(0,-6.7e-15,-5.4) rot=(0,0,1;0rad)
  Reference1 = -> Assembly [Hex_screw_M5_10_039.Edge2,Hex_screw_M5_10_039.Edge2]
  Reference2 = -> Assembly [T_Nut_2020_M057.Edge6,T_Nut_2020_M057.Edge6]
FEATURE [App::FeaturePython] Joint129  label="Fixed064"  # Assembly joint (typed FeaturePython)
  Activated = true
  AngleMax = 0
  AngleMin = 0
  Detach1 = false
  Detach2 = false
  Distance = 0
  Distance2 = 0
  EnableAngleMax = false
  EnableAngleMin = false
  EnableLengthMax = false
  EnableLengthMin = false
  JointType = 0 (Fixed)
  LengthMax = 0
  LengthMin = 0
  Offset2 = pos=(0,0,-6) rot=(0,0,1;0rad)
  Placement1 = pos=(-6.98683,35.5575,0) rot=(0,0,1;0rad)
  Placement2 = pos=(-7e-16,-6.7e-15,-5.4) rot=(0,0,1;0rad)
  Reference1 = -> Assembly [Hex_screw_M5_10_038.Edge2,Hex_screw_M5_10_038.Edge2]
  Reference2 = -> Assembly [T_Nut_2020_M058.Edge6,T_Nut_2020_M058.Edge6]
FEATURE [App::Link] T_Nut_2020_M059  label="T-Nut_2020_M059"
  LinkPlacement = pos=(419.9,212,568.675) rot=(1,0,0;1.5708rad)
  LinkedObject = -> <external ../parts/T-nut_20.FCStd>#Part__Feature
  Placement = pos=(419.9,212,568.675) rot=(1,0,0;1.5708rad)
FEATURE [App::Link] T_Nut_2020_M060  label="T-Nut_2020_M060"
  LinkPlacement = pos=(412,220.1,569.617) rot=(0.57735,-0.57735,-0.57735;2.0944rad)
  LinkedObject = -> <external ../parts/T-nut_20.FCStd>#Part__Feature
  Placement = pos=(412,220.1,569.617) rot=(0.57735,-0.57735,-0.57735;2.0944rad)
FEATURE [App::FeaturePython] Joint130  label="Slider064"  # Assembly joint (typed FeaturePython)
  Activated = true
  AngleMax = 0
  AngleMin = 0
  Detach1 = false
  Detach2 = false
  Distance = 0
  Distance2 = 0
  EnableAngleMax = false
  EnableAngleMin = false
  EnableLengthMax = false
  EnableLengthMin = false
  JointType = 3 (Slider)
  LengthMax = 0
  LengthMin = 0
  Offset2 = pos=(0,0,0) rot=(0,0,1;1.5708rad)
  Placement1 = pos=(-3,0,0) rot=(-0.57735,-0.57735,0.57735;4.18879rad)
  Placement2 = pos=(-3.1,-8,580) rot=(0.707107,0.707107,0;3.14159rad)
  Reference1 = -> Assembly [T_Nut_2020_M059.Edge27,T_Nut_2020_M059.Edge27]
  Reference2 = -> Assembly [Tslot20_heigh003.Edge81,Tslot20_heigh003.Vertex43]
FEATURE [App::FeaturePython] Joint131  label="Slider065"  # Assembly joint (typed FeaturePython)
  Activated = true
  AngleMax = 0
  AngleMin = 0
  Detach1 = false
  Detach2 = false
  Distance = 0
  Distance2 = 0
  EnableAngleMax = false
  EnableAngleMin = false
  EnableLengthMax = false
  EnableLengthMin = false
  JointType = 3 (Slider)
  LengthMax = 0
  LengthMin = 0
  Placement1 = pos=(-3,0,0) rot=(-0.57735,-0.57735,0.57735;4.18879rad)
  Placement2 = pos=(-8,3.1,580) rot=(0,0,1;0rad)
  Reference1 = -> Assembly [T_Nut_2020_M060.Edge27,T_Nut_2020_M060.Edge27]
  Reference2 = -> Assembly [Tslot20_heigh003.Edge104,Tslot20_heigh003.Vertex67]
FEATURE [App::Link] Hex_screw_M5_10_041  label="Hex screw M5 10.040"
  LinkPlacement = pos=(417.4,213.113,534.06) rot=(0.57735,-0.57735,-0.57735;2.0944rad)
  LinkedObject = -> <external ../secondary/bolts.FCStd>#Body004
  Placement = pos=(417.4,213.113,534.06) rot=(0.57735,-0.57735,-0.57735;2.0944rad)
FEATURE [App::Link] Hex_screw_M5_10_042  label="Unnamed"
FEATURE [App::FeaturePython] Joint132  label="Fixed065"  # Assembly joint (typed FeaturePython)
  Activated = true
  AngleMax = 0
  AngleMin = 0
  Detach1 = false
  Detach2 = false
  Distance = 0
  Distance2 = 0
  EnableAngleMax = false
  EnableAngleMin = false
  EnableLengthMax = false
  EnableLengthMin = false
  JointType = 0 (Fixed)
  LengthMax = 0
  LengthMin = 0
  Offset2 = pos=(0,0,-6) rot=(0,0,1;0rad)
  Placement1 = pos=(-6.98683,35.5575,-5.68e-14) rot=(0,0,1;0rad)
  Placement2 = pos=(-7e-16,-6.7e-15,-5.4) rot=(0,0,1;0rad)
  Reference1 = -> Assembly [Hex_screw_M5_10_041.Edge2,Hex_screw_M5_10_041.Edge2]
  Reference2 = -> Assembly [T_Nut_2020_M060.Edge6,T_Nut_2020_M060.Edge6]
FEATURE [App::FeaturePython] Joint133  label="Fixed066"  # Assembly joint (typed FeaturePython)
  Activated = true
  AngleMax = 0
  AngleMin = 0
  Detach1 = false
  Detach2 = false
  Distance = 0
  Distance2 = 0
  EnableAngleMax = false
  EnableAngleMin = false
  EnableLengthMax = false
  EnableLengthMin = false
  JointType = 0 (Fixed)
  LengthMax = 0
  LengthMin = 0
  Offset2 = pos=(0,0,-6) rot=(0,0,1;0rad)
  Placement1 = pos=(-6.98683,35.5575,0) rot=(0,0,1;0rad)
  Placement2 = pos=(0,-6.7e-15,-5.4) rot=(0,0,1;0rad)
  Reference1 = -> Assembly [Hex_screw_M5_10_040.Edge2,Hex_screw_M5_10_040.Edge2]
  Reference2 = -> Assembly [T_Nut_2020_M059.Edge6,T_Nut_2020_M059.Edge6]
FEATURE [Assembly::JointGroup] Joints
  Group = -> [GroundedJoint,Joint,Joint001,Joint002,Joint003,Joint004,Joint005,Joint006,Joint007,Joint008,Joint009,Joint010,Joint011,Joint012,Joint013,Joint014,Joint015,Joint016,Joint017,Joint018,Joint019,Joint020,Joint021,Joint022,Joint023,Joint025,Joint026,Joint027,Joint028,Joint029,Joint030,Joint031,Joint032,Joint033,Joint037,Joint038,Joint039,Joint040,Joint041,Joint042,Joint043,Joint044,Joint045,Joint046,+86 more]
FEATURE [Assembly::AssemblyObject] Assembly  label="asm_dbox"
  Group = -> [Joints,Tslot20_heigh,GroundedJoint,Tslot20_len,Joint,Tslot20_heigh001,Joint001,Tslot20_wid,Joint002,Tslot20_heigh002,Joint003,Tslot20_len001,Joint004,Tslot20_heigh003,Joint005,Tslot20_wid001,Joint006,Tslot20_len002,Joint007,Tslot20_len003,Joint008,Tslot20_wid002,Tslot20_wid003,Joint009,Joint010,Body,Joint011,Body001,Body002,Body003,Joint012,Joint013,Joint014,Body004,Joint015,Body005,Body006,+220 more]
  Origin = -> Origin
  Type = Assembly

RESOLVED EXTERNAL PARTS (link-assembly join: the EXTERNAL_REF files above that resolve inside this repo's crawl, each included once):
---- part ../downloads/2020-corner-bracket.FCStd = doc fcstd_bef0e746c20d ----
FCSTD DOCUMENT  (FreeCAD 1.0R39109 (Git))
Label: 2020-corner-bracket
License: All rights reserved
LicenseURL: http://en.wikipedia.org/wiki/All_rights_reserved
objects: Sketcher::SketchObject×5, PartDesign::Pocket×3, PartDesign::Pad×2, PartDesign::PolarPattern×1, PartDesign::Chamfer×1, PartDesign::Body×1, App::Part×1
note: 31 computed .brp shape members not serialized (recipe doc carries the construction recipe); baked Part::Feature solids carry a one-line shape summary decoded from their .brp

FEATURE [Sketcher::SketchObject] Sketch
  ArcFitTolerance = 0
  AttachmentSupport = -> [XZ_Plane001]
  FullyConstrained = true
  MakeInternals = false
  MapMode = 5
  Placement = pos=(0,0,0) rot=(1,0,0;1.5708rad)
  sketch-geometry (5):
    g0: LineSegment StartX=-10 StartY=10 StartZ=0 EndX=-10 EndY=-10 EndZ=0
    g1: LineSegment StartX=-10 StartY=-10 StartZ=0 EndX=10 EndY=-10 EndZ=0
    g2: LineSegment StartX=10 StartY=-10 StartZ=0 EndX=10 EndY=-7 EndZ=0
    g3: LineSegment StartX=10 StartY=-7 StartZ=0 EndX=-7 EndY=10 EndZ=0
    g4: LineSegment StartX=-7 StartY=10 StartZ=0 EndX=-10 EndY=10 EndZ=0
  constraints (13):
    c: Coincident(g0,g1)
    c: Coincident(g1,g2)
    c: Vertical(g2)
    c: Coincident(g2,g3)
    c: Coincident(g3,g4)
    c: Coincident(g4,g0)
    c: Horizontal(g4)
    c: DistanceX(g1,g1) = 20
    c: DistanceY(g2,g2) = 3
    c: Equal(g2,g4)
    c: Equal(g1,g0)
    c: Symmetric(g0,g0,g-1)
    c: Symmetric(g0,g1,g-2)
FEATURE [PartDesign::Pad] Pad
  Direction = (0,-1,2e-16)
  Length = 17
  Length2 = 10
  Midplane = true
  Placement = pos=(0,0,0) rot=(1,0,0;1.5708rad)
  Profile = -> Sketch
  ReferenceAxis = -> Sketch [N_Axis]
  Suppressed = false
  Type = 0
FEATURE [Sketcher::SketchObject] Sketch001
  ArcFitTolerance = 0
  AttachmentSupport = -> [Pad]
  FullyConstrained = true
  MakeInternals = false
  MapMode = 5
  Placement = pos=(-10,0,0) rot=(0.707107,0,-0.707107;3.14159rad)
  sketch-geometry (4):
    g0: ArcOfCircle CenterX=-1.5 CenterY=-2e-16 CenterZ=0 NormalX=0 NormalY=0 NormalZ=1 AngleXU=0 Radius=2.9 StartAngle=1.5708 EndAngle=4.71239
    g1: ArcOfCircle CenterX=1.5 CenterY=-2e-16 CenterZ=0 NormalX=0 NormalY=0 NormalZ=1 AngleXU=0 Radius=2.9 StartAngle=4.71239 EndAngle=7.85398
    g2: LineSegment StartX=-1.5 StartY=-2.9 StartZ=0 EndX=1.5 EndY=-2.9 EndZ=0
    g3: LineSegment StartX=1.5 StartY=2.9 StartZ=0 EndX=-1.5 EndY=2.9 EndZ=0
  constraints (9):
    c: Tangent(g0,g2) = -1.5708
    c: Tangent(g2,g1) = -1.5708
    c: Tangent(g1,g3) = -1.5708
    c: Tangent(g3,g0) = -1.5708
    c: Equal(g0,g1)
    c: DistanceX(g0,g1) = 3
    c: Radius(g0) = 2.9
    c: Symmetric(g1,g0,g-2)
    c: Symmetric(g1,g1,g-1)
FEATURE [PartDesign::Pocket] Pocket
  BaseFeature = -> Pad
  Direction = (1,0,2e-16)
  Length = 3
  Length2 = 5
  Placement = pos=(0,0,0) rot=(1,0,0;1.5708rad)
  Profile = -> Sketch001
  ReferenceAxis = -> Sketch001 [N_Axis]
  Suppressed = false
  Type = 0
FEATURE [Sketcher::SketchObject] Sketch002
  ArcFitTolerance = 0
  AttachmentSupport = -> [Pocket]
  FullyConstrained = true
  MakeInternals = false
  MapMode = 5
  Placement = pos=(0,-4.4e-15,-10) rot=(1,0,0;3.14159rad)
  sketch-geometry (4):
    g0: ArcOfCircle CenterX=-1.5 CenterY=-1e-16 CenterZ=0 NormalX=0 NormalY=0 NormalZ=1 AngleXU=0 Radius=2.9 StartAngle=1.5708 EndAngle=4.71239
    g1: ArcOfCircle CenterX=1.5 CenterY=-1e-16 CenterZ=0 NormalX=0 NormalY=0 NormalZ=1 AngleXU=0 Radius=2.9 StartAngle=4.71239 EndAngle=7.85398
    g2: LineSegment StartX=-1.5 StartY=-2.9 StartZ=0 EndX=1.5 EndY=-2.9 EndZ=0
    g3: LineSegment StartX=1.5 StartY=2.9 StartZ=0 EndX=-1.5 EndY=2.9 EndZ=0
  constraints (9):
    c: Tangent(g0,g2) = -1.5708
    c: Tangent(g2,g1) = -1.5708
    c: Tangent(g1,g3) = -1.5708
    c: Tangent(g3,g0) = -1.5708
    c: Equal(g0,g1)
    c: DistanceX(g0,g1) = 3
    c: Radius(g0) = 2.9
    c: Symmetric(g1,g0,g-2)
    c: Symmetric(g1,g1,g-1)
FEATURE [PartDesign::Pocket] Pocket001
  BaseFeature = -> Pocket
  Direction = (0,0,1)
  Length = 3
  Length2 = 5
  Placement = pos=(0,0,0) rot=(1,0,0;1.5708rad)
  Profile = -> Sketch002
  ReferenceAxis = -> Sketch002 [N_Axis]
  Suppressed = false
  Type = 0
FEATURE [Sketcher::SketchObject] Sketch003
  ArcFitTolerance = 0
  AttachmentSupport = -> [Pocket001]
  ExternalGeometry = -> [Pocket001]
  FullyConstrained = true
  MakeInternals = false
  MapMode = 5
  Placement = pos=(0,0,-7) rot=(1,0,0;3.14159rad)
  sketch-geometry (4):
    g0: LineSegment StartX=-7 StartY=5.5 StartZ=0 EndX=10 EndY=5.5 EndZ=0
    g1: LineSegment StartX=10 StartY=5.5 StartZ=0 EndX=10 EndY=-5.5 EndZ=0
    g2: LineSegment StartX=10 StartY=-5.5 StartZ=0 EndX=-7 EndY=-5.5 EndZ=0
    g3: LineSegment StartX=-7 StartY=-5.5 StartZ=0 EndX=-7 EndY=5.5 EndZ=0
  constraints (11):
    c: Coincident(g0,g1)
    c: Coincident(g1,g2)
    c: Coincident(g2,g3)
    c: Coincident(g3,g0)
    c: Horizontal(g0)
    c: Horizontal(g2)
    c: Vertical(g3)
    c: DistanceY(g3,g3) = 11
    c: Symmetric(g1,g0,g-1)
    c: DistanceX(g0) = -7
    c: DistanceX(g0,g-3) = 0
FEATURE [PartDesign::Pocket] Pocket002
  BaseFeature = -> Pocket001
  Direction = (0,0,1)
  Length = 5
  Length2 = 5
  Placement = pos=(0,0,0) rot=(1,0,0;1.5708rad)
  Profile = -> Sketch003
  ReferenceAxis = -> Sketch003 [N_Axis]
  Suppressed = false
  Type = 1
FEATURE [Sketcher::SketchObject] Sketch004
  ArcFitTolerance = 0
  AttachmentSupport = -> [Pocket002]
  ExternalGeometry = -> [Pocket002]
  FullyConstrained = true
  MakeInternals = false
  MapMode = 5
  Placement = pos=(-10,0,0) rot=(0.707107,0,-0.707107;3.14159rad)
  sketch-geometry (8):
    g0: LineSegment StartX=-8.5 StartY=2 StartZ=0 EndX=-7 EndY=2 EndZ=0
    g1: LineSegment StartX=-7 StartY=2 StartZ=0 EndX=-7 EndY=-2 EndZ=0
    g2: LineSegment StartX=-7 StartY=-2 StartZ=0 EndX=-8.5 EndY=-2 EndZ=0
    g3: LineSegment StartX=-8.5 StartY=-2 StartZ=0 EndX=-8.5 EndY=2 EndZ=0
    g4: LineSegment StartX=7 StartY=2 StartZ=0 EndX=8.5 EndY=2 EndZ=0
    g5: LineSegment StartX=8.5 StartY=2 StartZ=0 EndX=8.5 EndY=-2 EndZ=0
    g6: LineSegment StartX=8.5 StartY=-2 StartZ=0 EndX=7 EndY=-2 EndZ=0
    g7: LineSegment StartX=7 StartY=-2 StartZ=0 EndX=7 EndY=2 EndZ=0
  constraints (23):
    c: Coincident(g0,g1)
    c: Coincident(g1,g2)
    c: Coincident(g2,g3)
    c: Coincident(g3,g0)
    c: Horizontal(g0)
    c: Horizontal(g2)
    c: Vertical(g1)
    c: Vertical(g3)
    c: Coincident(g4,g5)
    c: Coincident(g5,g6)
    c: Coincident(g6,g7)
    c: Coincident(g7,g4)
    c: Horizontal(g4)
    c: Horizontal(g6)
    c: Vertical(g7)
    c: Equal(g5,g1)
    c: Equal(g2,g6)
    c: DistanceX(g0,g0) = 1.5
    c: Horizontal(g1,g6)
    c: Symmetric(g5,g4,g-1)
    c: DistanceX(g4,g-3) = 1.5
    c: DistanceY(g1,g1) = 4
    c: DistanceX(g-4,g0) = 1.5
FEATURE [PartDesign::Pad] Pad001
  BaseFeature = -> Pocket002
  Direction = (-1,0,-2e-16)
  Length = 1
  Length2 = 10
  Placement = pos=(0,0,0) rot=(1,0,0;1.5708rad)
  Profile = -> Sketch004
  ReferenceAxis = -> Sketch004 [N_Axis]
  Suppressed = false
  Type = 0
FEATURE [PartDesign::PolarPattern] PolarPattern
  Angle = 90
  Axis = -> Y_Axis001
  BaseFeature = -> Pad001
  Mode = 0
  Occurrences = 2
  Offset = 120
  Originals = -> [Pad001]
  Placement = pos=(0,0,0) rot=(1,0,0;1.5708rad)
  Reversed = true
  Suppressed = false
  TransformMode = 0
FEATURE [PartDesign::Chamfer] Chamfer
  Angle = 45
  Base = -> PolarPattern [Edge48,Edge45,Edge64,Edge61,Edge80,Edge77,Edge96,Edge93]
  BaseFeature = -> PolarPattern
  ChamferType = 0
  FlipDirection = false
  Placement = pos=(0,0,0) rot=(1,0,0;1.5708rad)
  Size = 0.25
  Size2 = 1
  SupportTransform = false
  Suppressed = false
  UseAllEdges = false
FEATURE [PartDesign::Body] Body
  AllowCompound = false
  Group = -> [Sketch,Pad,Sketch001,Pocket,Sketch002,Pocket001,Sketch003,Pocket002,Sketch004,Pad001,PolarPattern,Chamfer]
  Origin = -> Origin001
  Tip = -> Chamfer
FEATURE [App::Part] Part  label="Part_Bracket"
  Group = -> [Body]
  Origin = -> Origin
---- part ../parts/T-Slot_20_height.FCStd = doc fcstd_4f71b7f3e539 ----
FCSTD DOCUMENT  (FreeCAD 1.0R39109 (Git))
Label: T-Slot_20_height
License: All rights reserved
LicenseURL: http://en.wikipedia.org/wiki/All_rights_reserved
objects: Sketcher::SketchObject×3, TechDraw::DrawViewDimension×3, PartDesign::Pocket×2, TechDraw::DrawProjGroupItem×2, PartDesign::Pad×1, PartDesign::Body×1, TechDraw::DrawSVGTemplate×1, TechDraw::DrawProjGroup×1, TechDraw::DrawPage×1
note: 22 computed .brp shape members not serialized (recipe doc carries the construction recipe); baked Part::Feature solids carry a one-line shape summary decoded from their .brp

FEATURE [Sketcher::SketchObject] Sketch
  ArcFitTolerance = 0
  AttachmentSupport = -> [XY_Plane]
  FullyConstrained = true
  MakeInternals = false
  MapMode = 5
  sketch-geometry (4):
    g0: LineSegment StartX=-10 StartY=10 StartZ=0 EndX=10 EndY=10 EndZ=0
    g1: LineSegment StartX=10 StartY=10 StartZ=0 EndX=10 EndY=-10 EndZ=0
    g2: LineSegment StartX=10 StartY=-10 StartZ=0 EndX=-10 EndY=-10 EndZ=0
    g3: LineSegment StartX=-10 StartY=-10 StartZ=0 EndX=-10 EndY=10 EndZ=0
  constraints (10):
    c: Coincident(g0,g1)
    c: Coincident(g1,g2)
    c: Coincident(g2,g3)
    c: Coincident(g3,g0)
    c: Horizontal(g0)
    c: Vertical(g1)
    c: Symmetric(g2,g1,g-2)
    c: Symmetric(g0,g2,g-1)
    c: Equal(g3,g2)
    c: Distance(g0) = 20
FEATURE [PartDesign::Pad] Pad  label="Change Length Here!"
  AllowMultiFace = false
  Direction = (0,0,1)
  Length = 580
  Length2 = 100
  Profile = -> Sketch
  ReferenceAxis = -> Sketch [N_Axis]
  Refine = true
  Suppressed = false
  Type = 0
FEATURE [Sketcher::SketchObject] Sketch001
  ArcFitTolerance = 0
  AttachmentSupport = -> [Pad]
  ExternalGeometry = -> [Pad]
  FullyConstrained = false
  MakeInternals = false
  MapMode = 5
  Placement = pos=(0,0,580) rot=(0,0,1;0rad)
  sketch-geometry (23):
    g0: LineSegment StartX=-3.1 StartY=10 StartZ=0 EndX=3.1 EndY=10 EndZ=0
    g1: LineSegment StartX=3.1 StartY=10 StartZ=0 EndX=3.1 EndY=8 EndZ=0
    g2: LineSegment [constr] StartX=3.1 StartY=8 StartZ=0 EndX=-3.1 EndY=8 EndZ=0
    g3: LineSegment StartX=-3.1 StartY=8 StartZ=0 EndX=-3.1 EndY=10 EndZ=0
    g4: LineSegment StartX=-3.1 StartY=8 StartZ=0 EndX=-6.23223 EndY=8 EndZ=0
    g5: LineSegment StartX=-6.23223 StartY=8 StartZ=0 EndX=-2.13223 EndY=3.9 EndZ=0
    g6: LineSegment StartX=-2.13223 StartY=3.9 StartZ=0 EndX=2.13223 EndY=3.9 EndZ=0
    g7: LineSegment StartX=2.13223 StartY=3.9 StartZ=0 EndX=6.23223 EndY=8 EndZ=0
    g8: LineSegment StartX=6.23223 StartY=8 StartZ=0 EndX=3.1 EndY=8 EndZ=0
    g9: LineSegment [constr] StartX=-3.9 StartY=3.9 StartZ=0 EndX=3.9 EndY=3.9 EndZ=0
    g10: LineSegment [constr] StartX=3.9 StartY=3.9 StartZ=0 EndX=3.9 EndY=-3.9 EndZ=0
    g11: LineSegment [constr] StartX=3.9 StartY=-3.9 StartZ=0 EndX=-3.9 EndY=-3.9 EndZ=0
    g12: LineSegment [constr] StartX=-3.9 StartY=-3.9 StartZ=0 EndX=-3.9 EndY=3.9 EndZ=0
    g13: Circle CenterX=0 CenterY=0 CenterZ=0 NormalX=0 NormalY=0 NormalZ=1 AngleXU=0 Radius=2.5
    g14: LineSegment [constr] StartX=3.9 StartY=3.9 StartZ=0 EndX=3.01612 EndY=4.78388 EndZ=0
    g15: LineSegment StartX=-3.1 StartY=-8 StartZ=0 EndX=-6.23223 EndY=-8 EndZ=0
    g16: LineSegment StartX=6.23223 StartY=-8 StartZ=0 EndX=3.1 EndY=-8 EndZ=0
    g17: LineSegment StartX=3.1 StartY=-10 StartZ=0 EndX=3.1 EndY=-8 EndZ=0
    g18: LineSegment StartX=-3.1 StartY=-10 StartZ=0 EndX=3.1 EndY=-10 EndZ=0
    g19: LineSegment StartX=-3.1 StartY=-8 StartZ=0 EndX=-3.1 EndY=-10 EndZ=0
    g20: LineSegment StartX=-6.23223 StartY=-8 StartZ=0 EndX=-2.13223 EndY=-3.9 EndZ=0
    g21: LineSegment StartX=-2.13223 StartY=-3.9 StartZ=0 EndX=2.13223 EndY=-3.9 EndZ=0
    g22: LineSegment StartX=2.13223 StartY=-3.9 StartZ=0 EndX=6.23223 EndY=-8 EndZ=0
  constraints (55):
    c: Coincident(g0,g1)
    c: Coincident(g1,g2)
    c: Coincident(g2,g3)
    c: Coincident(g3,g0)
    c: Horizontal(g2)
    c: Vertical(g1)
    c: Vertical(g3)
    c: PointOnObject(g0,g-3)
    c: Symmetric(g0,g0,g-2)
    c: Distance(g0) = 6.2
    c: Distance(g3) = 2
    c: Coincident(g3,g4)
    c: Horizontal(g4)
    c: Coincident(g4,g5)
    c: Coincident(g5,g6)
    c: Coincident(g6,g7)
    c: Coincident(g7,g8)
    c: Coincident(g8,g1)
    c: Horizontal(g8)
    c: Symmetric(g5,g6,g-2)
    c: Equal(g4,g8)
    c: Coincident(g9,g10)
    c: Coincident(g10,g11)
    c: Coincident(g11,g12)
    c: Coincident(g12,g9)
    c: Horizontal(g9)
    c: Vertical(g12)
    c: Equal(g9,g12)
    c: Symmetric(g11,g10,g-2)
    c: Symmetric(g9,g10,g-1)
    c: Distance(g9) = 7.8
    c: Coincident(g13,g-1)
    c: Radius(g13) = 2.5
    c: DistanceY(g6,g0) = 6.1
    c: Coincident(g14,g9)
    c: PointOnObject(g14,g7)
    c: Perpendicular(g7,g14)
    c: Distance(g14) = 1.25
    c: Angle(g6,g5) = 2.35619
    c: Coincident(g18,g17)
    c: Coincident(g19,g18)
    c: Vertical(g17)
    c: Vertical(g19)
    c: Distance(g18) = 6.2
    c: Distance(g19) = 2
    c: Coincident(g19,g15)
    c: Horizontal(g15)
    c: Coincident(g15,g20)
    c: Coincident(g20,g21)
    c: Coincident(g21,g22)
    c: Coincident(g22,g16)
    c: Coincident(g16,g17)
    c: Horizontal(g16)
    c: Equal(g15,g16)
    c: Angle(g21,g20) = -2.35619
FEATURE [PartDesign::Pocket] Pocket  label="Top & Bottom Slots"
  AllowMultiFace = false
  BaseFeature = -> Pad
  Direction = (0,0,-1)
  Length = 5
  Length2 = 100
  Profile = -> Sketch001
  Refine = true
  Suppressed = false
  Type = 1
FEATURE [Sketcher::SketchObject] Sketch002
  ArcFitTolerance = 0
  AttachmentSupport = -> [Pocket]
  ExternalGeometry = -> [Pocket]
  FullyConstrained = false
  MakeInternals = false
  MapMode = 5
  Placement = pos=(0,0,0) rot=(1,0,0;3.14159rad)
  sketch-geometry (19):
    g0: LineSegment StartX=-10 StartY=-3.1 StartZ=0 EndX=-8 EndY=-3.1 EndZ=0
    g1: LineSegment [constr] StartX=-8 StartY=-3.1 StartZ=0 EndX=-8 EndY=3.1 EndZ=0
    g2: LineSegment StartX=-8 StartY=3.1 StartZ=0 EndX=-10 EndY=3.1 EndZ=0
    g3: LineSegment StartX=-10 StartY=3.1 StartZ=0 EndX=-10 EndY=-3.1 EndZ=0
    g4: LineSegment StartX=-8 StartY=-3.1 StartZ=0 EndX=-8 EndY=-6.23223 EndZ=0
    g5: LineSegment StartX=-8 StartY=-6.23223 StartZ=0 EndX=-3.9 EndY=-2.13223 EndZ=0
    g6: LineSegment StartX=-3.9 StartY=-2.13223 StartZ=0 EndX=-3.9 EndY=2.13223 EndZ=0
    g7: LineSegment StartX=-3.9 StartY=2.13223 StartZ=0 EndX=-8 EndY=6.23223 EndZ=0
    g8: LineSegment StartX=-8 StartY=6.23223 StartZ=0 EndX=-8 EndY=3.1 EndZ=0
    g9: LineSegment [constr] StartX=-2.13223 StartY=3.9 StartZ=0 EndX=-3.9 EndY=2.13223 EndZ=0
    g10: LineSegment [constr] StartX=2.13223 StartY=3.9 StartZ=0 EndX=3.9 EndY=2.13223 EndZ=0
    g11: LineSegment StartX=3.9 StartY=-2.13223 StartZ=0 EndX=3.9 EndY=2.13223 EndZ=0
    g12: LineSegment StartX=8 StartY=-6.23223 StartZ=0 EndX=3.9 EndY=-2.13223 EndZ=0
    g13: LineSegment StartX=3.9 StartY=2.13223 StartZ=0 EndX=8 EndY=6.23223 EndZ=0
    g14: LineSegment StartX=8 StartY=6.23223 StartZ=0 EndX=8 EndY=3.1 EndZ=0
    g15: LineSegment StartX=8 StartY=3.1 StartZ=0 EndX=10 EndY=3.1 EndZ=0
    g16: LineSegment StartX=10 StartY=3.1 StartZ=0 EndX=10 EndY=-3.1 EndZ=0
    g17: LineSegment StartX=10 StartY=-3.1 StartZ=0 EndX=8 EndY=-3.1 EndZ=0
    g18: LineSegment StartX=8 StartY=-3.1 StartZ=0 EndX=8 EndY=-6.23223 EndZ=0
  constraints (43):
    c: Coincident(g0,g1)
    c: Coincident(g1,g2)
    c: Coincident(g2,g3)
    c: Coincident(g3,g0)
    c: Horizontal(g0)
    c: Horizontal(g2)
    c: Vertical(g1)
    c: PointOnObject(g0,g-3)
    c: Symmetric(g2,g0,g-1)
    c: Distance(g3) = 6.2
    c: Distance(g0) = 2
    c: Coincident(g0,g4)
    c: Vertical(g4)
    c: Coincident(g4,g5)
    c: Coincident(g5,g6)
    c: Coincident(g6,g7)
    c: Coincident(g7,g8)
    c: Coincident(g8,g2)
    c: Vertical(g8)
    c: Equal(g4,g8)
    c: Symmetric(g6,g5,g-1)
    c: DistanceX(g2,g6) = 6.1
    c: Angle(g6,g5) = 2.35619
    c: Coincident(g9,g-4)
    c: Perpendicular(g-4,g9)
    c: Coincident(g6,g9)
    c: Coincident(g15,g16)
    c: Coincident(g16,g17)
    c: Horizontal(g17)
    c: Horizontal(g15)
    c: Distance(g16) = 6.2
    c: Distance(g17) = 2
    c: Coincident(g17,g18)
    c: Vertical(g18)
    c: Coincident(g18,g12)
    c: Coincident(g12,g11)
    c: Coincident(g11,g13)
    c: Coincident(g13,g14)
    c: Coincident(g14,g15)
    c: Vertical(g14)
    c: Equal(g18,g14)
    c: Angle(g11,g12) = -2.35619
    c: Coincident(g11,g10)
FEATURE [PartDesign::Pocket] Pocket001  label="R&L Slots"
  AllowMultiFace = false
  BaseFeature = -> Pocket
  Direction = (0,0,1)
  Length = 5
  Length2 = 100
  Profile = -> Sketch002
  Refine = true
  Suppressed = false
  Type = 1
FEATURE [PartDesign::Body] Body  label="Tslot20_heigh"
  AllowCompound = false
  Group = -> [Sketch,Pad,Sketch001,Pocket,Sketch002,Pocket001]
  Origin = -> Origin
  Tip = -> Pocket001
FEATURE [TechDraw::DrawSVGTemplate] Template
  EditableTexts = approval_person=B. Hecate; creator=Djordje Vujic; date_of_issue=1/21/2025; document_type=Assembly Drawing; general_tolerances=ISO 2768-m; identification_number=DN; language_code=EN; part_material=Stainless steel Mat.No. 1.4301; revision_index=AAA; sheet_number=1 / 4; sheet_scale=1 : 3; title=T-Slot_20_height
  Height = 297
  Orientation = 0
  Template = D:/Program Files/FreeCAD 1.0/data/Mod/TechDraw/Templates/A4_Portrait_ISO5457_minimal.svg
  Width = 210
FEATURE [TechDraw::DrawProjGroupItem] ProjItem  label="Front"
  CoarseView = false
  Direction = (0,-1,0)
  Focus = 100
  HardHidden = false
  IsoCount = 0
  IsoHidden = false
  IsoVisible = false
  LockPosition = true
  Perspective = false
  Rotation = 0
  RotationVector = (1,0,0)
  Scale = 0.333333
  ScaleType = 2
  ScrubCount = 1
  SeamHidden = false
  SeamVisible = false
  SmoothHidden = false
  SmoothVisible = true
  Source = -> [Body]
  Type = 0
  X = 0
  XDirection = (1,0,0)
  Y = 0
FEATURE [TechDraw::DrawProjGroupItem] ProjItem001  label="Bottom"
  CoarseView = false
  Direction = (0,0,-1)
  Focus = 100
  HardHidden = false
  IsoCount = 0
  IsoHidden = false
  IsoVisible = false
  LockPosition = false
  Perspective = false
  Rotation = 0
  RotationVector = (1,0,0)
  Scale = 0.333333
  ScaleType = 2
  ScrubCount = 1
  SeamHidden = false
  SeamVisible = false
  SmoothHidden = false
  SmoothVisible = true
  Source = -> [Body]
  Type = 5
  X = 0
  XDirection = (1,0,0)
  Y = 115
FEATURE [TechDraw::DrawProjGroup] ProjGroup
  Anchor = -> ProjItem
  AutoDistribute = true
  LockPosition = false
  ProjectionType = 0
  Rotation = 0
  Scale = 0.333333
  ScaleType = 2
  Source = -> [Body]
  Views = -> [ProjItem,ProjItem001]
  X = 107.297
  Y = 159.41
  spacingX = 15
  spacingY = 15
FEATURE [TechDraw::DrawViewDimension] Dimension
  AngleOverride = false
  Arbitrary = false
  ArbitraryTolerances = false
  BoxCorners = (2) [(-3.33333,-3.33333,0),(3.33333,3.33333,0)]
  EqualTolerance = true
  ExtensionAngle = 0
  FormatSpec = %.2w
  FormatSpecOverTolerance = %+.2w
  FormatSpecUnderTolerance = %+.2w
  Inverted = false
  LineAngle = 0
  LockPosition = false
  MeasureType = 1
  OverTolerance = 0
  References2D = -> [ProjItem001]
  Rotation = 0
  ScaleType = 0
  TheoreticalExact = false
  Type = 0
  UnderTolerance = 0
  X = -10.1772
  Y = -5.35989
FEATURE [TechDraw::DrawViewDimension] Dimension001
  AngleOverride = false
  Arbitrary = false
  ArbitraryTolerances = false
  BoxCorners = (2) [(-3.33333,-96.6666,0),(3.33333,96.6666,0)]
  EqualTolerance = true
  ExtensionAngle = 0
  FormatSpec = %.2w
  FormatSpecOverTolerance = %+.2w
  FormatSpecUnderTolerance = %+.2w
  Inverted = false
  LineAngle = 0
  LockPosition = false
  MeasureType = 1
  OverTolerance = 0
  References2D = -> [ProjItem]
  Rotation = 0
  ScaleType = 0
  TheoreticalExact = false
  Type = 2
  UnderTolerance = 0
  X = -56.3813
  Y = 3.94419
FEATURE [TechDraw::DrawViewDimension] Dimension002
  AngleOverride = false
  Arbitrary = false
  ArbitraryTolerances = false
  BoxCorners = (2) [(-3.33333,-3.33333,0),(3.33333,3.33333,0)]
  EqualTolerance = true
  ExtensionAngle = 0
  FormatSpec = %.2w
  FormatSpecOverTolerance = %+.2w
  FormatSpecUnderTolerance = %+.2w
  Inverted = false
  LineAngle = 0
  LockPosition = false
  MeasureType = 1
  OverTolerance = 0
  References2D = -> [ProjItem001]
  Rotation = 0
  ScaleType = 0
  TheoreticalExact = false
  Type = 2
  UnderTolerance = 0
  X = 23.6969
  Y = -8.1912
FEATURE [TechDraw::DrawPage] Page
  KeepUpdated = true
  NextBalloonIndex = 1
  ProjectionType = 0
  Template = -> Template
  Views = -> [ProjGroup,Dimension,Dimension001,Dimension002]
---- part ../parts/T-Slot_20_length.FCStd = doc fcstd_5f879e7afb14 ----
FCSTD DOCUMENT  (FreeCAD 1.0R39109 (Git))
Label: T-Slot_20_length
License: All rights reserved
LicenseURL: http://en.wikipedia.org/wiki/All_rights_reserved
objects: Sketcher::SketchObject×3, PartDesign::Pocket×2, TechDraw::DrawProjGroupItem×2, TechDraw::DrawViewDimension×2, PartDesign::Pad×1, PartDesign::Body×1, TechDraw::DrawSVGTemplate×1, TechDraw::DrawProjGroup×1, TechDraw::DrawPage×1
note: 19 computed .brp shape members not serialized (recipe doc carries the construction recipe); baked Part::Feature solids carry a one-line shape summary decoded from their .brp

FEATURE [Sketcher::SketchObject] Sketch
  ArcFitTolerance = 0
  AttachmentSupport = -> [XY_Plane]
  FullyConstrained = true
  MakeInternals = false
  MapMode = 5
  sketch-geometry (4):
    g0: LineSegment StartX=-10 StartY=10 StartZ=0 EndX=10 EndY=10 EndZ=0
    g1: LineSegment StartX=10 StartY=10 StartZ=0 EndX=10 EndY=-10 EndZ=0
    g2: LineSegment StartX=10 StartY=-10 StartZ=0 EndX=-10 EndY=-10 EndZ=0
    g3: LineSegment StartX=-10 StartY=-10 StartZ=0 EndX=-10 EndY=10 EndZ=0
  constraints (10):
    c: Coincident(g0,g1)
    c: Coincident(g1,g2)
    c: Coincident(g2,g3)
    c: Coincident(g3,g0)
    c: Horizontal(g0)
    c: Vertical(g1)
    c: Symmetric(g2,g1,g-2)
    c: Symmetric(g0,g2,g-1)
    c: Equal(g3,g2)
    c: Distance(g0) = 20
FEATURE [PartDesign::Pad] Pad  label="Change Length Here!"
  AllowMultiFace = false
  Direction = (0,0,1)
  Length = 400
  Length2 = 100
  Profile = -> Sketch
  ReferenceAxis = -> Sketch [N_Axis]
  Refine = true
  Suppressed = false
  Type = 0
FEATURE [Sketcher::SketchObject] Sketch001
  ArcFitTolerance = 0
  AttachmentSupport = -> [Pad]
  ExternalGeometry = -> [Pad]
  FullyConstrained = false
  MakeInternals = false
  MapMode = 5
  Placement = pos=(0,0,400) rot=(0,0,1;0rad)
  sketch-geometry (23):
    g0: LineSegment StartX=-3.1 StartY=10 StartZ=0 EndX=3.1 EndY=10 EndZ=0
    g1: LineSegment StartX=3.1 StartY=10 StartZ=0 EndX=3.1 EndY=8 EndZ=0
    g2: LineSegment [constr] StartX=3.1 StartY=8 StartZ=0 EndX=-3.1 EndY=8 EndZ=0
    g3: LineSegment StartX=-3.1 StartY=8 StartZ=0 EndX=-3.1 EndY=10 EndZ=0
    g4: LineSegment StartX=-3.1 StartY=8 StartZ=0 EndX=-6.23223 EndY=8 EndZ=0
    g5: LineSegment StartX=-6.23223 StartY=8 StartZ=0 EndX=-2.13223 EndY=3.9 EndZ=0
    g6: LineSegment StartX=-2.13223 StartY=3.9 StartZ=0 EndX=2.13223 EndY=3.9 EndZ=0
    g7: LineSegment StartX=2.13223 StartY=3.9 StartZ=0 EndX=6.23223 EndY=8 EndZ=0
    g8: LineSegment StartX=6.23223 StartY=8 StartZ=0 EndX=3.1 EndY=8 EndZ=0
    g9: LineSegment [constr] StartX=-3.9 StartY=3.9 StartZ=0 EndX=3.9 EndY=3.9 EndZ=0
    g10: LineSegment [constr] StartX=3.9 StartY=3.9 StartZ=0 EndX=3.9 EndY=-3.9 EndZ=0
    g11: LineSegment [constr] StartX=3.9 StartY=-3.9 StartZ=0 EndX=-3.9 EndY=-3.9 EndZ=0
    g12: LineSegment [constr] StartX=-3.9 StartY=-3.9 StartZ=0 EndX=-3.9 EndY=3.9 EndZ=0
    g13: Circle CenterX=0 CenterY=0 CenterZ=0 NormalX=0 NormalY=0 NormalZ=1 AngleXU=0 Radius=2.5
    g14: LineSegment [constr] StartX=3.9 StartY=3.9 StartZ=0 EndX=3.01612 EndY=4.78388 EndZ=0
    g15: LineSegment StartX=-3.1 StartY=-8 StartZ=0 EndX=-6.23223 EndY=-8 EndZ=0
    g16: LineSegment StartX=6.23223 StartY=-8 StartZ=0 EndX=3.1 EndY=-8 EndZ=0
    g17: LineSegment StartX=3.1 StartY=-10 StartZ=0 EndX=3.1 EndY=-8 EndZ=0
    g18: LineSegment StartX=-3.1 StartY=-10 StartZ=0 EndX=3.1 EndY=-10 EndZ=0
    g19: LineSegment StartX=-3.1 StartY=-8 StartZ=0 EndX=-3.1 EndY=-10 EndZ=0
    g20: LineSegment StartX=-6.23223 StartY=-8 StartZ=0 EndX=-2.13223 EndY=-3.9 EndZ=0
    g21: LineSegment StartX=-2.13223 StartY=-3.9 StartZ=0 EndX=2.13223 EndY=-3.9 EndZ=0
    g22: LineSegment StartX=2.13223 StartY=-3.9 StartZ=0 EndX=6.23223 EndY=-8 EndZ=0
  constraints (55):
    c: Coincident(g0,g1)
    c: Coincident(g1,g2)
    c: Coincident(g2,g3)
    c: Coincident(g3,g0)
    c: Horizontal(g2)
    c: Vertical(g1)
    c: Vertical(g3)
    c: PointOnObject(g0,g-3)
    c: Symmetric(g0,g0,g-2)
    c: Distance(g0) = 6.2
    c: Distance(g3) = 2
    c: Coincident(g3,g4)
    c: Horizontal(g4)
    c: Coincident(g4,g5)
    c: Coincident(g5,g6)
    c: Coincident(g6,g7)
    c: Coincident(g7,g8)
    c: Coincident(g8,g1)
    c: Horizontal(g8)
    c: Symmetric(g5,g6,g-2)
    c: Equal(g4,g8)
    c: Coincident(g9,g10)
    c: Coincident(g10,g11)
    c: Coincident(g11,g12)
    c: Coincident(g12,g9)
    c: Horizontal(g9)
    c: Vertical(g12)
    c: Equal(g9,g12)
    c: Symmetric(g11,g10,g-2)
    c: Symmetric(g9,g10,g-1)
    c: Distance(g9) = 7.8
    c: Coincident(g13,g-1)
    c: Radius(g13) = 2.5
    c: DistanceY(g6,g0) = 6.1
    c: Coincident(g14,g9)
    c: PointOnObject(g14,g7)
    c: Perpendicular(g7,g14)
    c: Distance(g14) = 1.25
    c: Angle(g6,g5) = 2.35619
    c: Coincident(g18,g17)
    c: Coincident(g19,g18)
    c: Vertical(g17)
    c: Vertical(g19)
    c: Distance(g18) = 6.2
    c: Distance(g19) = 2
    c: Coincident(g19,g15)
    c: Horizontal(g15)
    c: Coincident(g15,g20)
    c: Coincident(g20,g21)
    c: Coincident(g21,g22)
    c: Coincident(g22,g16)
    c: Coincident(g16,g17)
    c: Horizontal(g16)
    c: Equal(g15,g16)
    c: Angle(g21,g20) = -2.35619
FEATURE [PartDesign::Pocket] Pocket  label="Top & Bottom Slots"
  AllowMultiFace = false
  BaseFeature = -> Pad
  Direction = (0,0,-1)
  Length = 5
  Length2 = 100
  Profile = -> Sketch001
  Refine = true
  Suppressed = false
  Type = 1
FEATURE [Sketcher::SketchObject] Sketch002
  ArcFitTolerance = 0
  AttachmentSupport = -> [Pocket]
  ExternalGeometry = -> [Pocket]
  FullyConstrained = false
  MakeInternals = false
  MapMode = 5
  Placement = pos=(0,0,0) rot=(1,0,0;3.14159rad)
  sketch-geometry (19):
    g0: LineSegment StartX=-10 StartY=-3.1 StartZ=0 EndX=-8 EndY=-3.1 EndZ=0
    g1: LineSegment [constr] StartX=-8 StartY=-3.1 StartZ=0 EndX=-8 EndY=3.1 EndZ=0
    g2: LineSegment StartX=-8 StartY=3.1 StartZ=0 EndX=-10 EndY=3.1 EndZ=0
    g3: LineSegment StartX=-10 StartY=3.1 StartZ=0 EndX=-10 EndY=-3.1 EndZ=0
    g4: LineSegment StartX=-8 StartY=-3.1 StartZ=0 EndX=-8 EndY=-6.23223 EndZ=0
    g5: LineSegment StartX=-8 StartY=-6.23223 StartZ=0 EndX=-3.9 EndY=-2.13223 EndZ=0
    g6: LineSegment StartX=-3.9 StartY=-2.13223 StartZ=0 EndX=-3.9 EndY=2.13223 EndZ=0
    g7: LineSegment StartX=-3.9 StartY=2.13223 StartZ=0 EndX=-8 EndY=6.23223 EndZ=0
    g8: LineSegment StartX=-8 StartY=6.23223 StartZ=0 EndX=-8 EndY=3.1 EndZ=0
    g9: LineSegment [constr] StartX=-2.13223 StartY=3.9 StartZ=0 EndX=-3.9 EndY=2.13223 EndZ=0
    g10: LineSegment [constr] StartX=2.13223 StartY=3.9 StartZ=0 EndX=3.9 EndY=2.13223 EndZ=0
    g11: LineSegment StartX=3.9 StartY=-2.13223 StartZ=0 EndX=3.9 EndY=2.13223 EndZ=0
    g12: LineSegment StartX=8 StartY=-6.23223 StartZ=0 EndX=3.9 EndY=-2.13223 EndZ=0
    g13: LineSegment StartX=3.9 StartY=2.13223 StartZ=0 EndX=8 EndY=6.23223 EndZ=0
    g14: LineSegment StartX=8 StartY=6.23223 StartZ=0 EndX=8 EndY=3.1 EndZ=0
    g15: LineSegment StartX=8 StartY=3.1 StartZ=0 EndX=10 EndY=3.1 EndZ=0
    g16: LineSegment StartX=10 StartY=3.1 StartZ=0 EndX=10 EndY=-3.1 EndZ=0
    g17: LineSegment StartX=10 StartY=-3.1 StartZ=0 EndX=8 EndY=-3.1 EndZ=0
    g18: LineSegment StartX=8 StartY=-3.1 StartZ=0 EndX=8 EndY=-6.23223 EndZ=0
  constraints (43):
    c: Coincident(g0,g1)
    c: Coincident(g1,g2)
    c: Coincident(g2,g3)
    c: Coincident(g3,g0)
    c: Horizontal(g0)
    c: Horizontal(g2)
    c: Vertical(g1)
    c: PointOnObject(g0,g-3)
    c: Symmetric(g2,g0,g-1)
    c: Distance(g3) = 6.2
    c: Distance(g0) = 2
    c: Coincident(g0,g4)
    c: Vertical(g4)
    c: Coincident(g4,g5)
    c: Coincident(g5,g6)
    c: Coincident(g6,g7)
    c: Coincident(g7,g8)
    c: Coincident(g8,g2)
    c: Vertical(g8)
    c: Equal(g4,g8)
    c: Symmetric(g6,g5,g-1)
    c: DistanceX(g2,g6) = 6.1
    c: Angle(g6,g5) = 2.35619
    c: Coincident(g9,g-4)
    c: Perpendicular(g-4,g9)
    c: Coincident(g6,g9)
    c: Coincident(g15,g16)
    c: Coincident(g16,g17)
    c: Horizontal(g17)
    c: Horizontal(g15)
    c: Distance(g16) = 6.2
    c: Distance(g17) = 2
    c: Coincident(g17,g18)
    c: Vertical(g18)
    c: Coincident(g18,g12)
    c: Coincident(g12,g11)
    c: Coincident(g11,g13)
    c: Coincident(g13,g14)
    c: Coincident(g14,g15)
    c: Vertical(g14)
    c: Equal(g18,g14)
    c: Angle(g11,g12) = -2.35619
    c: Coincident(g11,g10)
FEATURE [PartDesign::Pocket] Pocket001  label="R&L Slots"
  AllowMultiFace = false
  BaseFeature = -> Pocket
  Direction = (0,0,1)
  Length = 5
  Length2 = 100
  Profile = -> Sketch002
  Refine = true
  Suppressed = false
  Type = 1
FEATURE [PartDesign::Body] Body  label="Tslot20_len"
  AllowCompound = false
  Group = -> [Sketch,Pad,Sketch001,Pocket,Sketch002,Pocket001]
  Origin = -> Origin
  Tip = -> Pocket001
FEATURE [TechDraw::DrawSVGTemplate] Template
  EditableTexts = approval_person=B. Hecate; creator=Djordje Vujic; date_of_issue=1/21/2025; document_type=Assembly Drawing; general_tolerances=ISO 2768-m; identification_number=DN; language_code=EN; part_material=Stainless steel Mat.No. 1.4301; revision_index=AAA; sheet_number=1 / 5; sheet_scale=1 : 2; title=T-Slot_20_length
  Height = 297
  Orientation = 0
  Template = D:/Program Files/FreeCAD 1.0/data/Mod/TechDraw/Templates/A4_Portrait_ISO5457_minimal.svg
  Width = 210
FEATURE [TechDraw::DrawProjGroupItem] ProjItem  label="Front"
  CoarseView = false
  Direction = (0,-1,0)
  Focus = 100
  HardHidden = false
  IsoCount = 0
  IsoHidden = false
  IsoVisible = false
  LockPosition = true
  Perspective = false
  Rotation = 0
  RotationVector = (1,0,0)
  Scale = 0.5
  ScaleType = 0
  ScrubCount = 1
  SeamHidden = false
  SeamVisible = false
  SmoothHidden = false
  SmoothVisible = true
  Source = -> [Body]
  Type = 0
  X = 0
  XDirection = (1,0,0)
  Y = 0
FEATURE [TechDraw::DrawProjGroupItem] ProjItem001  label="Bottom"
  CoarseView = false
  Direction = (0,0,-1)
  Focus = 100
  HardHidden = false
  IsoCount = 0
  IsoHidden = false
  IsoVisible = false
  LockPosition = false
  Perspective = false
  Rotation = 0
  RotationVector = (1,0,0)
  Scale = 0.5
  ScaleType = 0
  ScrubCount = 1
  SeamHidden = false
  SeamVisible = false
  SmoothHidden = false
  SmoothVisible = true
  Source = -> [Body]
  Type = 5
  X = 0
  XDirection = (1,0,0)
  Y = 120
FEATURE [TechDraw::DrawProjGroup] ProjGroup
  Anchor = -> ProjItem
  AutoDistribute = true
  LockPosition = false
  ProjectionType = 0
  Rotation = 0
  Scale = 0.5
  ScaleType = 2
  Source = -> [Body]
  Views = -> [ProjItem,ProjItem001]
  X = 104.931
  Y = 160.059
  spacingX = 15
  spacingY = 15
FEATURE [TechDraw::DrawViewDimension] Dimension
  AngleOverride = false
  Arbitrary = false
  ArbitraryTolerances = false
  BoxCorners = (2) [(-5,-100,0),(5,100,0)]
  EqualTolerance = true
  ExtensionAngle = 0
  FormatSpec = %.2w
  FormatSpecOverTolerance = %+.2w
  FormatSpecUnderTolerance = %+.2w
  Inverted = false
  LineAngle = 0
  LockPosition = false
  MeasureType = 1
  OverTolerance = 0
  References2D = -> [ProjItem]
  Rotation = 0
  ScaleType = 0
  TheoreticalExact = false
  Type = 2
  UnderTolerance = 0
  X = 24.0453
  Y = -12.9531
FEATURE [TechDraw::DrawViewDimension] Dimension001
  AngleOverride = false
  Arbitrary = false
  ArbitraryTolerances = false
  BoxCorners = (2) [(-5,-5,0),(5,5,0)]
  EqualTolerance = true
  ExtensionAngle = 0
  FormatSpec = %.2w
  FormatSpecOverTolerance = %+.2w
  FormatSpecUnderTolerance = %+.2w
  Inverted = false
  LineAngle = 0
  LockPosition = false
  MeasureType = 1
  OverTolerance = 0
  References2D = -> [ProjItem001]
  Rotation = 0
  ScaleType = 0
  TheoreticalExact = false
  Type = 2
  UnderTolerance = 0
  X = 23.5343
  Y = -10.7172
FEATURE [TechDraw::DrawPage] Page
  KeepUpdated = true
  NextBalloonIndex = 1
  ProjectionType = 0
  Template = -> Template
  Views = -> [ProjGroup,Dimension,Dimension001]
---- part ../parts/T-Slot_20_width.FCStd = doc fcstd_92ffd128162d ----
FCSTD DOCUMENT  (FreeCAD 1.0R39109 (Git))
Label: T-Slot_20_width
License: All rights reserved
LicenseURL: http://en.wikipedia.org/wiki/All_rights_reserved
objects: Sketcher::SketchObject×3, PartDesign::Pocket×2, TechDraw::DrawProjGroupItem×2, TechDraw::DrawViewDimension×2, PartDesign::Pad×1, PartDesign::Body×1, TechDraw::DrawSVGTemplate×1, TechDraw::DrawProjGroup×1, TechDraw::DrawPage×1
note: 19 computed .brp shape members not serialized (recipe doc carries the construction recipe); baked Part::Feature solids carry a one-line shape summary decoded from their .brp

FEATURE [Sketcher::SketchObject] Sketch
  ArcFitTolerance = 0
  AttachmentSupport = -> [XY_Plane]
  FullyConstrained = true
  MakeInternals = false
  MapMode = 5
  sketch-geometry (4):
    g0: LineSegment StartX=-10 StartY=10 StartZ=0 EndX=10 EndY=10 EndZ=0
    g1: LineSegment StartX=10 StartY=10 StartZ=0 EndX=10 EndY=-10 EndZ=0
    g2: LineSegment StartX=10 StartY=-10 StartZ=0 EndX=-10 EndY=-10 EndZ=0
    g3: LineSegment StartX=-10 StartY=-10 StartZ=0 EndX=-10 EndY=10 EndZ=0
  constraints (10):
    c: Coincident(g0,g1)
    c: Coincident(g1,g2)
    c: Coincident(g2,g3)
    c: Coincident(g3,g0)
    c: Horizontal(g0)
    c: Vertical(g1)
    c: Symmetric(g2,g1,g-2)
    c: Symmetric(g0,g2,g-1)
    c: Equal(g3,g2)
    c: Distance(g0) = 20
FEATURE [PartDesign::Pad] Pad  label="Change Length Here!"
  AllowMultiFace = false
  Direction = (0,0,1)
  Length = 200
  Length2 = 100
  Profile = -> Sketch
  ReferenceAxis = -> Sketch [N_Axis]
  Refine = true
  Suppressed = false
  Type = 0
FEATURE [Sketcher::SketchObject] Sketch001
  ArcFitTolerance = 0
  AttachmentSupport = -> [Pad]
  ExternalGeometry = -> [Pad]
  FullyConstrained = false
  MakeInternals = false
  MapMode = 5
  Placement = pos=(0,0,200) rot=(0,0,1;0rad)
  sketch-geometry (23):
    g0: LineSegment StartX=-3.1 StartY=10 StartZ=0 EndX=3.1 EndY=10 EndZ=0
    g1: LineSegment StartX=3.1 StartY=10 StartZ=0 EndX=3.1 EndY=8 EndZ=0
    g2: LineSegment [constr] StartX=3.1 StartY=8 StartZ=0 EndX=-3.1 EndY=8 EndZ=0
    g3: LineSegment StartX=-3.1 StartY=8 StartZ=0 EndX=-3.1 EndY=10 EndZ=0
    g4: LineSegment StartX=-3.1 StartY=8 StartZ=0 EndX=-6.23223 EndY=8 EndZ=0
    g5: LineSegment StartX=-6.23223 StartY=8 StartZ=0 EndX=-2.13223 EndY=3.9 EndZ=0
    g6: LineSegment StartX=-2.13223 StartY=3.9 StartZ=0 EndX=2.13223 EndY=3.9 EndZ=0
    g7: LineSegment StartX=2.13223 StartY=3.9 StartZ=0 EndX=6.23223 EndY=8 EndZ=0
    g8: LineSegment StartX=6.23223 StartY=8 StartZ=0 EndX=3.1 EndY=8 EndZ=0
    g9: LineSegment [constr] StartX=-3.9 StartY=3.9 StartZ=0 EndX=3.9 EndY=3.9 EndZ=0
    g10: LineSegment [constr] StartX=3.9 StartY=3.9 StartZ=0 EndX=3.9 EndY=-3.9 EndZ=0
    g11: LineSegment [constr] StartX=3.9 StartY=-3.9 StartZ=0 EndX=-3.9 EndY=-3.9 EndZ=0
    g12: LineSegment [constr] StartX=-3.9 StartY=-3.9 StartZ=0 EndX=-3.9 EndY=3.9 EndZ=0
    g13: Circle CenterX=0 CenterY=0 CenterZ=0 NormalX=0 NormalY=0 NormalZ=1 AngleXU=0 Radius=2.5
    g14: LineSegment [constr] StartX=3.9 StartY=3.9 StartZ=0 EndX=3.01612 EndY=4.78388 EndZ=0
    g15: LineSegment StartX=-3.1 StartY=-8 StartZ=0 EndX=-6.23223 EndY=-8 EndZ=0
    g16: LineSegment StartX=6.23223 StartY=-8 StartZ=0 EndX=3.1 EndY=-8 EndZ=0
    g17: LineSegment StartX=3.1 StartY=-10 StartZ=0 EndX=3.1 EndY=-8 EndZ=0
    g18: LineSegment StartX=-3.1 StartY=-10 StartZ=0 EndX=3.1 EndY=-10 EndZ=0
    g19: LineSegment StartX=-3.1 StartY=-8 StartZ=0 EndX=-3.1 EndY=-10 EndZ=0
    g20: LineSegment StartX=-6.23223 StartY=-8 StartZ=0 EndX=-2.13223 EndY=-3.9 EndZ=0
    g21: LineSegment StartX=-2.13223 StartY=-3.9 StartZ=0 EndX=2.13223 EndY=-3.9 EndZ=0
    g22: LineSegment StartX=2.13223 StartY=-3.9 StartZ=0 EndX=6.23223 EndY=-8 EndZ=0
  constraints (55):
    c: Coincident(g0,g1)
    c: Coincident(g1,g2)
    c: Coincident(g2,g3)
    c: Coincident(g3,g0)
    c: Horizontal(g2)
    c: Vertical(g1)
    c: Vertical(g3)
    c: PointOnObject(g0,g-3)
    c: Symmetric(g0,g0,g-2)
    c: Distance(g0) = 6.2
    c: Distance(g3) = 2
    c: Coincident(g3,g4)
    c: Horizontal(g4)
    c: Coincident(g4,g5)
    c: Coincident(g5,g6)
    c: Coincident(g6,g7)
    c: Coincident(g7,g8)
    c: Coincident(g8,g1)
    c: Horizontal(g8)
    c: Symmetric(g5,g6,g-2)
    c: Equal(g4,g8)
    c: Coincident(g9,g10)
    c: Coincident(g10,g11)
    c: Coincident(g11,g12)
    c: Coincident(g12,g9)
    c: Horizontal(g9)
    c: Vertical(g12)
    c: Equal(g9,g12)
    c: Symmetric(g11,g10,g-2)
    c: Symmetric(g9,g10,g-1)
    c: Distance(g9) = 7.8
    c: Coincident(g13,g-1)
    c: Radius(g13) = 2.5
    c: DistanceY(g6,g0) = 6.1
    c: Coincident(g14,g9)
    c: PointOnObject(g14,g7)
    c: Perpendicular(g7,g14)
    c: Distance(g14) = 1.25
    c: Angle(g6,g5) = 2.35619
    c: Coincident(g18,g17)
    c: Coincident(g19,g18)
    c: Vertical(g17)
    c: Vertical(g19)
    c: Distance(g18) = 6.2
    c: Distance(g19) = 2
    c: Coincident(g19,g15)
    c: Horizontal(g15)
    c: Coincident(g15,g20)
    c: Coincident(g20,g21)
    c: Coincident(g21,g22)
    c: Coincident(g22,g16)
    c: Coincident(g16,g17)
    c: Horizontal(g16)
    c: Equal(g15,g16)
    c: Angle(g21,g20) = -2.35619
FEATURE [PartDesign::Pocket] Pocket  label="Top & Bottom Slots"
  AllowMultiFace = false
  BaseFeature = -> Pad
  Direction = (0,0,-1)
  Length = 5
  Length2 = 100
  Profile = -> Sketch001
  Refine = true
  Suppressed = false
  Type = 1
FEATURE [Sketcher::SketchObject] Sketch002
  ArcFitTolerance = 0
  AttachmentSupport = -> [Pocket]
  ExternalGeometry = -> [Pocket]
  FullyConstrained = false
  MakeInternals = false
  MapMode = 5
  Placement = pos=(0,0,0) rot=(1,0,0;3.14159rad)
  sketch-geometry (19):
    g0: LineSegment StartX=-10 StartY=-3.1 StartZ=0 EndX=-8 EndY=-3.1 EndZ=0
    g1: LineSegment [constr] StartX=-8 StartY=-3.1 StartZ=0 EndX=-8 EndY=3.1 EndZ=0
    g2: LineSegment StartX=-8 StartY=3.1 StartZ=0 EndX=-10 EndY=3.1 EndZ=0
    g3: LineSegment StartX=-10 StartY=3.1 StartZ=0 EndX=-10 EndY=-3.1 EndZ=0
    g4: LineSegment StartX=-8 StartY=-3.1 StartZ=0 EndX=-8 EndY=-6.23223 EndZ=0
    g5: LineSegment StartX=-8 StartY=-6.23223 StartZ=0 EndX=-3.9 EndY=-2.13223 EndZ=0
    g6: LineSegment StartX=-3.9 StartY=-2.13223 StartZ=0 EndX=-3.9 EndY=2.13223 EndZ=0
    g7: LineSegment StartX=-3.9 StartY=2.13223 StartZ=0 EndX=-8 EndY=6.23223 EndZ=0
    g8: LineSegment StartX=-8 StartY=6.23223 StartZ=0 EndX=-8 EndY=3.1 EndZ=0
    g9: LineSegment [constr] StartX=-2.13223 StartY=3.9 StartZ=0 EndX=-3.9 EndY=2.13223 EndZ=0
    g10: LineSegment [constr] StartX=2.13223 StartY=3.9 StartZ=0 EndX=3.9 EndY=2.13223 EndZ=0
    g11: LineSegment StartX=3.9 StartY=-2.13223 StartZ=0 EndX=3.9 EndY=2.13223 EndZ=0
    g12: LineSegment StartX=8 StartY=-6.23223 StartZ=0 EndX=3.9 EndY=-2.13223 EndZ=0
    g13: LineSegment StartX=3.9 StartY=2.13223 StartZ=0 EndX=8 EndY=6.23223 EndZ=0
    g14: LineSegment StartX=8 StartY=6.23223 StartZ=0 EndX=8 EndY=3.1 EndZ=0
    g15: LineSegment StartX=8 StartY=3.1 StartZ=0 EndX=10 EndY=3.1 EndZ=0
    g16: LineSegment StartX=10 StartY=3.1 StartZ=0 EndX=10 EndY=-3.1 EndZ=0
    g17: LineSegment StartX=10 StartY=-3.1 StartZ=0 EndX=8 EndY=-3.1 EndZ=0
    g18: LineSegment StartX=8 StartY=-3.1 StartZ=0 EndX=8 EndY=-6.23223 EndZ=0
  constraints (43):
    c: Coincident(g0,g1)
    c: Coincident(g1,g2)
    c: Coincident(g2,g3)
    c: Coincident(g3,g0)
    c: Horizontal(g0)
    c: Horizontal(g2)
    c: Vertical(g1)
    c: PointOnObject(g0,g-3)
    c: Symmetric(g2,g0,g-1)
    c: Distance(g3) = 6.2
    c: Distance(g0) = 2
    c: Coincident(g0,g4)
    c: Vertical(g4)
    c: Coincident(g4,g5)
    c: Coincident(g5,g6)
    c: Coincident(g6,g7)
    c: Coincident(g7,g8)
    c: Coincident(g8,g2)
    c: Vertical(g8)
    c: Equal(g4,g8)
    c: Symmetric(g6,g5,g-1)
    c: DistanceX(g2,g6) = 6.1
    c: Angle(g6,g5) = 2.35619
    c: Coincident(g9,g-4)
    c: Perpendicular(g-4,g9)
    c: Coincident(g6,g9)
    c: Coincident(g15,g16)
    c: Coincident(g16,g17)
    c: Horizontal(g17)
    c: Horizontal(g15)
    c: Distance(g16) = 6.2
    c: Distance(g17) = 2
    c: Coincident(g17,g18)
    c: Vertical(g18)
    c: Coincident(g18,g12)
    c: Coincident(g12,g11)
    c: Coincident(g11,g13)
    c: Coincident(g13,g14)
    c: Coincident(g14,g15)
    c: Vertical(g14)
    c: Equal(g18,g14)
    c: Angle(g11,g12) = -2.35619
    c: Coincident(g11,g10)
FEATURE [PartDesign::Pocket] Pocket001  label="R&L Slots"
  AllowMultiFace = false
  BaseFeature = -> Pocket
  Direction = (0,0,1)
  Length = 5
  Length2 = 100
  Profile = -> Sketch002
  Refine = true
  Suppressed = false
  Type = 1
FEATURE [PartDesign::Body] Body  label="Tslot20_wid"
  AllowCompound = false
  Group = -> [Sketch,Pad,Sketch001,Pocket,Sketch002,Pocket001]
  Origin = -> Origin
  Tip = -> Pocket001
FEATURE [TechDraw::DrawSVGTemplate] Template
  EditableTexts = approval_person=B. Hecate; creator=Djordje Vujic; date_of_issue=1/21/2025; document_type=Assembly Drawing; general_tolerances=ISO 2768-m; identification_number=DN; language_code=EN; part_material=Stainless steel Mat.No. 1.4301; revision_index=AAA; sheet_number=1 / 6; sheet_scale=1 : 2; title=T-Slot_20_width
  Height = 297
  Orientation = 0
  Template = D:/Program Files/FreeCAD 1.0/data/Mod/TechDraw/Templates/A4_Portrait_ISO5457_minimal.svg
  Width = 210
FEATURE [TechDraw::DrawProjGroupItem] ProjItem  label="Front"
  CoarseView = false
  Direction = (0,-1,0)
  Focus = 100
  HardHidden = false
  IsoCount = 0
  IsoHidden = false
  IsoVisible = false
  LockPosition = true
  Perspective = false
  Rotation = 0
  RotationVector = (1,0,0)
  Scale = 0.5
  ScaleType = 0
  ScrubCount = 1
  SeamHidden = false
  SeamVisible = false
  SmoothHidden = false
  SmoothVisible = true
  Source = -> [Body]
  Type = 0
  X = 0
  XDirection = (1,0,0)
  Y = 0
FEATURE [TechDraw::DrawProjGroupItem] ProjItem001  label="Bottom"
  CoarseView = false
  Direction = (0,0,-1)
  Focus = 100
  HardHidden = false
  IsoCount = 0
  IsoHidden = false
  IsoVisible = false
  LockPosition = false
  Perspective = false
  Rotation = 0
  RotationVector = (1,0,0)
  Scale = 0.5
  ScaleType = 0
  ScrubCount = 1
  SeamHidden = false
  SeamVisible = false
  SmoothHidden = false
  SmoothVisible = true
  Source = -> [Body]
  Type = 5
  X = 0
  XDirection = (1,0,0)
  Y = 70
FEATURE [TechDraw::DrawProjGroup] ProjGroup
  Anchor = -> ProjItem
  AutoDistribute = true
  LockPosition = false
  ProjectionType = 0
  Rotation = 0
  Scale = 0.5
  ScaleType = 2
  Source = -> [Body]
  Views = -> [ProjItem,ProjItem001]
  X = 106.426
  Y = 132.809
  spacingX = 15
  spacingY = 15
FEATURE [TechDraw::DrawViewDimension] Dimension
  AngleOverride = false
  Arbitrary = false
  ArbitraryTolerances = false
  BoxCorners = (2) [(-5,-50,0),(5,50,0)]
  EqualTolerance = true
  ExtensionAngle = 0
  FormatSpec = %.2w
  FormatSpecOverTolerance = %+.2w
  FormatSpecUnderTolerance = %+.2w
  Inverted = false
  LineAngle = 0
  LockPosition = false
  MeasureType = 1
  OverTolerance = 0
  References2D = -> [ProjItem]
  Rotation = 0
  ScaleType = 0
  TheoreticalExact = false
  Type = 2
  UnderTolerance = 0
  X = 38.4564
  Y = 0
FEATURE [TechDraw::DrawViewDimension] Dimension001
  AngleOverride = false
  Arbitrary = false
  ArbitraryTolerances = false
  BoxCorners = (2) [(-5,-5,0),(5,5,0)]
  EqualTolerance = true
  ExtensionAngle = 0
  FormatSpec = %.2w
  FormatSpecOverTolerance = %+.2w
  FormatSpecUnderTolerance = %+.2w
  Inverted = false
  LineAngle = 0
  LockPosition = false
  MeasureType = 1
  OverTolerance = 0
  References2D = -> [ProjItem001]
  Rotation = 0
  ScaleType = 0
  TheoreticalExact = false
  Type = 2
  UnderTolerance = 0
  X = 34.5605
  Y = 0
FEATURE [TechDraw::DrawPage] Page
  KeepUpdated = true
  NextBalloonIndex = 1
  ProjectionType = 0
  Template = -> Template
  Views = -> [ProjGroup,Dimension,Dimension001]
---- part ../secondary/bolts.FCStd = doc fcstd_e978128cc4a6 ----
FCSTD DOCUMENT  (FreeCAD 1.0R39109 (Git))
Label: bolts
License: All rights reserved
LicenseURL: https://en.wikipedia.org/wiki/All_rights_reserved
objects: Sketcher::SketchObject×8, PartDesign::Pad×8, Part::Feature×7, PartDesign::Body×5
note: 52 computed .brp shape members not serialized (recipe doc carries the construction recipe); baked Part::Feature solids carry a one-line shape summary decoded from their .brp

FEATURE [Part::Feature] BOLTS_part  label="Hex socket head cap screw DIN 912 M4 10.0"
  Placement = pos=(0,-31,0) rot=(0,0,1;0rad)
  shape: bbox 7 x 7 x 24 mm, 12 faces (baked)
FEATURE [Part::Feature] BOLTS_part001  label="Hex socket head cap screw DIN 912 M4 15.0"
  Placement = pos=(0,-20,0) rot=(0,0,1;0rad)
  shape: bbox 7 x 7 x 24 mm, 12 faces (baked)
FEATURE [Part::Feature] BOLTS_part002  label="Hex socket head cap screw DIN 912 M4 20.0"
  Placement = pos=(0,-10,0) rot=(0,0,1;0rad)
  shape: bbox 7 x 7 x 24 mm, 12 faces (baked)
FEATURE [Part::Feature] BOLTS_part003  label="Hex socket head cap screw DIN 912 M5 10.0"
  Placement = pos=(0,-1,0) rot=(0,0,1;0rad)
  shape: bbox 8.5 x 8.5 x 27 mm, 12 faces (baked)
FEATURE [Part::Feature] BOLTS_part004  label="Hex socket head cap screw DIN 912 M5 15.0"
  Placement = pos=(0,9,0) rot=(0,0,1;0rad)
  shape: bbox 8.5 x 8.5 x 27 mm, 12 faces (baked)
FEATURE [Part::Feature] BOLTS_part005  label="Hex socket head cap screw DIN 912 M5 20.0"
  Placement = pos=(0,19,0) rot=(0,0,1;0rad)
  shape: bbox 8.5 x 8.5 x 27 mm, 12 faces (baked)
FEATURE [Part::Feature] BOLTS_part006  label="Hex socket head cap screw DIN 912 M2.5 10.0"
  Placement = pos=(0,35,0) rot=(0,0,1;0rad)
  shape: bbox 4.5 x 4.5 x 19.5 mm, 12 faces (baked)
FEATURE [Sketcher::SketchObject] Sketch
  ArcFitTolerance = 1e-06
  AttachmentSupport = -> [XY_Plane001]
  FullyConstrained = false
  MakeInternals = false
  MapMode = 5
  sketch-geometry (1):
    g0: Circle CenterX=-6.98683 CenterY=35.5575 CenterZ=0 NormalX=0 NormalY=0 NormalZ=1 AngleXU=0 Radius=2.25
  constraints (1):
    c: Diameter(g0) = 4.5
FEATURE [PartDesign::Pad] Pad
  Direction = (0,0,1)
  Length = 2.5
  Length2 = 10
  Profile = -> Sketch
  ReferenceAxis = -> Sketch [N_Axis]
  Refine = true
  Suppressed = false
  Type = 0
FEATURE [Sketcher::SketchObject] Sketch001
  ArcFitTolerance = 1e-06
  AttachmentSupport = -> [Pad]
  ExternalGeometry = -> [Pad]
  FullyConstrained = true
  MakeInternals = false
  MapMode = 5
  Placement = pos=(0,0,2.5) rot=(0,0,1;0rad)
  sketch-geometry (1):
    g0: Circle CenterX=-6.98683 CenterY=35.5575 CenterZ=0 NormalX=0 NormalY=0 NormalZ=1 AngleXU=0 Radius=1.25
  constraints (2):
    c: Coincident(g0,g-3)
    c: Diameter(g0) = 2.5
FEATURE [PartDesign::Pad] Pad001
  BaseFeature = -> Pad
  Direction = (0,0,1)
  Length = 8
  Length2 = 10
  Profile = -> Sketch001
  ReferenceAxis = -> Sketch001 [N_Axis]
  Refine = true
  Suppressed = false
  Type = 0
FEATURE [PartDesign::Body] Body001  label="Hex screw M2.5 08.0"
  AllowCompound = false
  Group = -> [Sketch,Pad,Sketch001,Pad001]
  Origin = -> Origin001
  Tip = -> Pad001
FEATURE [Sketcher::SketchObject] Sketch002
  ArcFitTolerance = 1e-06
  AttachmentSupport = -> [XY_Plane002]
  FullyConstrained = false
  MakeInternals = false
  MapMode = 5
  sketch-geometry (1):
    g0: Circle CenterX=-6.98683 CenterY=35.5575 CenterZ=0 NormalX=0 NormalY=0 NormalZ=1 AngleXU=0 Radius=2
  constraints (1):
    c: Diameter(g0) = 4
FEATURE [PartDesign::Pad] Pad002
  Direction = (0,0,1)
  Length = 10
  Length2 = 10
  Profile = -> Sketch002
  ReferenceAxis = -> Sketch002 [N_Axis]
  Refine = true
  Suppressed = false
  Type = 0
FEATURE [Sketcher::SketchObject] Sketch003
  ArcFitTolerance = 1e-06
  AttachmentSupport = -> [Pad002]
  FullyConstrained = false
  MakeInternals = false
  MapMode = 5
  Placement = pos=(0,0,10) rot=(0,0,1;0rad)
  sketch-geometry (1):
    g0: Circle CenterX=-6.98683 CenterY=35.5575 CenterZ=0 NormalX=0 NormalY=0 NormalZ=1 AngleXU=0 Radius=3.5
  constraints (1):
    c: Diameter(g0) = 7
FEATURE [PartDesign::Pad] Pad003
  BaseFeature = -> Pad002
  Direction = (0,0,1)
  Length = 4
  Length2 = 10
  Profile = -> Sketch003
  ReferenceAxis = -> Sketch003 [N_Axis]
  Refine = true
  Suppressed = false
  Type = 0
FEATURE [PartDesign::Body] Body002  label="Hex screw M4 10.0"
  AllowCompound = false
  Group = -> [Sketch002,Pad002,Sketch003,Pad003]
  Origin = -> Origin002
  Tip = -> Pad003
FEATURE [Sketcher::SketchObject] Sketch004
  ArcFitTolerance = 1e-06
  AttachmentSupport = -> [XY_Plane003]
  FullyConstrained = false
  MakeInternals = false
  MapMode = 5
  sketch-geometry (1):
    g0: Circle CenterX=-6.98683 CenterY=35.5575 CenterZ=0 NormalX=0 NormalY=0 NormalZ=1 AngleXU=0 Radius=2.25
  constraints (1):
    c: Diameter(g0) = 4.5
FEATURE [PartDesign::Pad] Pad004
  Direction = (0,0,1)
  Length = 2.5
  Length2 = 10
  Profile = -> Sketch004
  ReferenceAxis = -> Sketch004 [N_Axis]
  Refine = true
  Suppressed = false
  Type = 0
FEATURE [Sketcher::SketchObject] Sketch005
  ArcFitTolerance = 1e-06
  AttachmentSupport = -> [Pad004]
  ExternalGeometry = -> [Pad004]
  FullyConstrained = true
  MakeInternals = false
  MapMode = 5
  Placement = pos=(0,0,2.5) rot=(0,0,1;0rad)
  sketch-geometry (1):
    g0: Circle CenterX=-6.98683 CenterY=35.5575 CenterZ=0 NormalX=0 NormalY=0 NormalZ=1 AngleXU=0 Radius=1.25
  constraints (2):
    c: Coincident(g0,g-3)
    c: Diameter(g0) = 2.5
FEATURE [PartDesign::Pad] Pad005
  BaseFeature = -> Pad004
  Direction = (0,0,1)
  Length = 4
  Length2 = 10
  Profile = -> Sketch005
  ReferenceAxis = -> Sketch005 [N_Axis]
  Refine = true
  Suppressed = false
  Type = 0
FEATURE [PartDesign::Body] Body003  label="Hex screw M2.5 04.0"
  AllowCompound = false
  Group = -> [Sketch004,Pad004,Sketch005,Pad005]
  Origin = -> Origin003
  Tip = -> Pad005
FEATURE [PartDesign::Body] Body  label="Bolts"
  AllowCompound = false
  Origin = -> Origin
FEATURE [Sketcher::SketchObject] Sketch006
  ArcFitTolerance = 1e-06
  AttachmentSupport = -> [XY_Plane004]
  FullyConstrained = false
  MakeInternals = false
  MapMode = 5
  sketch-geometry (1):
    g0: Circle CenterX=-6.98683 CenterY=35.5575 CenterZ=0 NormalX=0 NormalY=0 NormalZ=1 AngleXU=0 Radius=2.5
  constraints (1):
    c: Diameter(g0) = 5
FEATURE [PartDesign::Pad] Pad006
  Direction = (0,0,1)
  Length = 10
  Length2 = 10
  Profile = -> Sketch006
  ReferenceAxis = -> Sketch006 [N_Axis]
  Refine = true
  Suppressed = false
  Type = 0
FEATURE [Sketcher::SketchObject] Sketch007
  ArcFitTolerance = 1e-06
  AttachmentSupport = -> [Pad006]
  FullyConstrained = false
  MakeInternals = false
  MapMode = 5
  Placement = pos=(0,0,10) rot=(0,0,1;0rad)
  sketch-geometry (1):
    g0: Circle CenterX=-6.98683 CenterY=35.5575 CenterZ=0 NormalX=0 NormalY=0 NormalZ=1 AngleXU=0 Radius=4.25
  constraints (1):
    c: Diameter(g0) = 8.5
FEATURE [PartDesign::Pad] Pad007
  BaseFeature = -> Pad006
  Direction = (0,0,1)
  Length = 4
  Length2 = 10
  Profile = -> Sketch007
  ReferenceAxis = -> Sketch007 [N_Axis]
  Refine = true
  Suppressed = false
  Type = 0
FEATURE [PartDesign::Body] Body004  label="Hex screw M5 10.0"
  AllowCompound = false
  Group = -> [Sketch006,Pad006,Sketch007,Pad007]
  Origin = -> Origin004
  Tip = -> Pad007
---- part asm_plate_front_back.FCStd = doc fcstd_c7d6dce85756 ----
FCSTD DOCUMENT  (FreeCAD 1.0R39109 (Git))
Label: asm_plate_front_back
License: All rights reserved
LicenseURL: https://en.wikipedia.org/wiki/All_rights_reserved
objects: App::Link×5, App::FeaturePython×5, Assembly::JointGroup×1, Assembly::AssemblyObject×1
EXTERNAL_REF file=../parts/plate_front_back.FCStd obj=Body
EXTERNAL_REF file=../secondary/bolts.FCStd obj=Body004

FEATURE [App::Link] plate_front_back
  LinkedObject = -> <external ../parts/plate_front_back.FCStd>#Body
FEATURE [App::FeaturePython] GroundedJoint  # Assembly grounded joint (typed FeaturePython)
  ObjectToGround = -> plate_front_back
FEATURE [App::FeaturePython] Joint001  label="Fixed001"  # Assembly joint (typed FeaturePython)
  Activated = true
  AngleMax = 0
  AngleMin = 0
  Detach1 = false
  Detach2 = false
  Distance = 0
  Distance2 = 0
  EnableAngleMax = false
  EnableAngleMin = false
  EnableLengthMax = false
  EnableLengthMin = false
  JointType = 0 (Fixed)
  LengthMax = 0
  LengthMin = 0
  Placement1 = pos=(-6.98683,35.5575,10) rot=(0,0,1;0rad)
  Placement2 = pos=(110,-240,3) rot=(0,0,1;0rad)
  Reference1 = -> Assembly [Hex_screw_M5_10_003.Edge3,Hex_screw_M5_10_003.Edge3]
  Reference2 = -> Assembly [plate_front_back.Edge15,plate_front_back.Edge15]
FEATURE [App::Link] Hex_screw_M5_10_003  label="Hex screw M5 10.003"
  LinkPlacement = pos=(116.987,-275.558,-7) rot=(0,0,1;0rad)
  LinkedObject = -> <external ../secondary/bolts.FCStd>#Body004
  Placement = pos=(116.987,-275.558,-7) rot=(0,0,1;0rad)
FEATURE [App::FeaturePython] Joint003  label="Fixed003"  # Assembly joint (typed FeaturePython)
  Activated = true
  AngleMax = 0
  AngleMin = 0
  Detach1 = false
  Detach2 = false
  Distance = 0
  Distance2 = 0
  EnableAngleMax = false
  EnableAngleMin = false
  EnableLengthMax = false
  EnableLengthMin = false
  JointType = 0 (Fixed)
  LengthMax = 0
  LengthMin = 0
  Placement1 = pos=(-6.98683,35.5575,10) rot=(0,0,1;0rad)
  Placement2 = pos=(110,240,3) rot=(0,0,1;0rad)
  Reference1 = -> Assembly [Hex_screw_M5_10_002.Edge3,Hex_screw_M5_10_002.Edge3]
  Reference2 = -> Assembly [plate_front_back.Edge21,plate_front_back.Edge21]
FEATURE [App::Link] Hex_screw_M5_10_002  label="Hex screw M5 10.002"
  LinkPlacement = pos=(116.987,204.442,-7) rot=(0,0,1;0rad)
  LinkedObject = -> <external ../secondary/bolts.FCStd>#Body004
  Placement = pos=(116.987,204.442,-7) rot=(0,0,1;0rad)
FEATURE [App::FeaturePython] Joint002  label="Fixed002"  # Assembly joint (typed FeaturePython)
  Activated = true
  AngleMax = 0
  AngleMin = 0
  Detach1 = false
  Detach2 = false
  Distance = 0
  Distance2 = 0
  EnableAngleMax = false
  EnableAngleMin = false
  EnableLengthMax = false
  EnableLengthMin = false
  JointType = 0 (Fixed)
  LengthMax = 0
  LengthMin = 0
  Placement1 = pos=(-6.98683,35.5575,10) rot=(0,0,1;0rad)
  Placement2 = pos=(-110,240,3) rot=(0,0,1;0rad)
  Reference1 = -> Assembly [Hex_screw_M5_10_001.Edge3,Hex_screw_M5_10_001.Edge3]
  Reference2 = -> Assembly [plate_front_back.Edge24,plate_front_back.Edge24]
FEATURE [App::Link] Hex_screw_M5_10_001  label="Hex screw M5 10.001"
  LinkPlacement = pos=(-103.013,204.442,-7) rot=(0,0,1;0rad)
  LinkedObject = -> <external ../secondary/bolts.FCStd>#Body004
  Placement = pos=(-103.013,204.442,-7) rot=(0,0,1;0rad)
FEATURE [App::Link] Hex_screw_M5_10_0  label="Hex screw M5 10.0"
  LinkPlacement = pos=(-103.013,-275.558,-7) rot=(0,0,1;0rad)
  LinkedObject = -> <external ../secondary/bolts.FCStd>#Body004
  Placement = pos=(-103.013,-275.558,-7) rot=(0,0,1;0rad)
FEATURE [App::FeaturePython] Joint  label="Fixed"  # Assembly joint (typed FeaturePython)
  Activated = true
  AngleMax = 0
  AngleMin = 0
  Detach1 = false
  Detach2 = false
  Distance = 0
  Distance2 = 0
  EnableAngleMax = false
  EnableAngleMin = false
  EnableLengthMax = false
  EnableLengthMin = false
  JointType = 0 (Fixed)
  LengthMax = 0
  LengthMin = 0
  Placement1 = pos=(-6.98683,35.5575,10) rot=(0,0,1;0rad)
  Placement2 = pos=(-110,-240,3) rot=(0,0,1;0rad)
  Reference1 = -> Assembly [Hex_screw_M5_10_0.Edge3,Hex_screw_M5_10_0.Edge3]
  Reference2 = -> Assembly [plate_front_back.Edge18,plate_front_back.Edge18]
FEATURE [Assembly::JointGroup] Joints
  Group = -> [GroundedJoint,Joint001,Joint002,Joint003,Joint]
FEATURE [Assembly::AssemblyObject] Assembly  label="asm_plate_front_back"
  Group = -> [Joints,plate_front_back,GroundedJoint,Hex_screw_M5_10_001,Hex_screw_M5_10_002,Hex_screw_M5_10_003,Joint001,Joint002,Joint003,Hex_screw_M5_10_0,Joint]
  Origin = -> Origin
  Type = Assembly
---- part asm_roof.FCStd = doc fcstd_e2c621f55444 ----
FCSTD DOCUMENT  (FreeCAD 1.0R39109 (Git))
Label: asm_roof
License: All rights reserved
LicenseURL: https://en.wikipedia.org/wiki/All_rights_reserved
objects: App::Link×20, App::FeaturePython×15, Assembly::AssemblyLink×2, Assembly::JointGroup×1, Assembly::AssemblyObject×1
EXTERNAL_REF file=../parts/plate_roof.FCStd obj=Body
EXTERNAL_REF file=../secondary/linear_slide.FCStd obj=Body
EXTERNAL_REF file=asm_cam_holder.FCStd obj=Assembly
EXTERNAL_REF file=asm_shf.FCStd obj=Assembly
EXTERNAL_REF file=asm_shf.FCStd obj=SHF12
EXTERNAL_REF file=asm_shf.FCStd obj=Hex_socket_head_cap_screw_DIN_912_M4_15_0
EXTERNAL_REF file=asm_shf.FCStd obj=Hex_socket_head_cap_screw_DIN_912_M5_15_0
EXTERNAL_REF file=asm_shf.FCStd obj=Hex_socket_head_cap_screw_DIN_912_M5_15_001
EXTERNAL_REF file=../secondary/nuts_hexagonal.FCStd obj=Part__Feature001
EXTERNAL_REF file=../secondary/nuts_hexagonal.FCStd obj=Part__Feature

FEATURE [App::Link] plate_roof001  label="plate_roof"
  LinkedObject = -> <external ../parts/plate_roof.FCStd>#Body
FEATURE [App::FeaturePython] GroundedJoint  # Assembly grounded joint (typed FeaturePython)
  ObjectToGround = -> plate_roof001
FEATURE [App::Link] linear_slide  label="linear_slide_12"
  LinkPlacement = pos=(-38,-53.8,-15.1359) rot=(0,0,1;0rad)
  LinkedObject = -> <external ../secondary/linear_slide.FCStd>#Body
  Placement = pos=(-38,-53.8,-15.1359) rot=(0,0,1;0rad)
FEATURE [App::Link] linear_slide001  label="linear_slide_12_001"
  LinkPlacement = pos=(38,-53.8,-15.136) rot=(0,0,1;0rad)
  LinkedObject = -> <external ../secondary/linear_slide.FCStd>#Body
  Placement = pos=(38,-53.8,-15.136) rot=(0,0,1;0rad)
FEATURE [App::Link] asm_cam_holder
  LinkPlacement = pos=(-1.51e-14,-53.8,66.8641) rot=(0,0,1;1.5708rad)
  LinkedObject = -> <external asm_cam_holder.FCStd>#Assembly
  Placement = pos=(-1.51e-14,-53.8,66.8641) rot=(0,0,1;1.5708rad)
FEATURE [App::Link] SHF12
  LinkedObject = -> <external asm_shf.FCStd>#SHF12
FEATURE [App::Link] Hex_socket_head_cap_screw_DIN_912_M4_15_0  label="Hex socket head cap screw DIN 912 M4 15.0"
  LinkPlacement = pos=(12.25,6.5,11.5) rot=(0,-1,0;1.5708rad)
  LinkedObject = -> <external asm_shf.FCStd>#Hex_socket_head_cap_screw_DIN_912_M4_15_0
  Placement = pos=(12.25,6.5,11.5) rot=(0,-1,0;1.5708rad)
FEATURE [App::Link] Hex_socket_head_cap_screw_DIN_912_M5_15_0  label="Hex socket head cap screw DIN 912 M5 15.0"
  LinkPlacement = pos=(18,11,1.16e-14) rot=(0.57735,-0.57735,0.57735;2.0944rad)
  LinkedObject = -> <external asm_shf.FCStd>#Hex_socket_head_cap_screw_DIN_912_M5_15_0
  Placement = pos=(18,11,1.16e-14) rot=(0.57735,-0.57735,0.57735;2.0944rad)
FEATURE [App::Link] Hex_socket_head_cap_screw_DIN_912_M5_15_001  label="Hex socket head cap screw DIN 912 M5 15.001"
  LinkPlacement = pos=(-18,11,1.16e-14) rot=(0.57735,-0.57735,0.57735;2.0944rad)
  LinkedObject = -> <external asm_shf.FCStd>#Hex_socket_head_cap_screw_DIN_912_M5_15_001
  Placement = pos=(-18,11,1.16e-14) rot=(0.57735,-0.57735,0.57735;2.0944rad)
FEATURE [Assembly::AssemblyLink] asm_SHF
  Group = -> [SHF12,Hex_socket_head_cap_screw_DIN_912_M4_15_0,Hex_socket_head_cap_screw_DIN_912_M5_15_0,Hex_socket_head_cap_screw_DIN_912_M5_15_001]
  LinkedObject = -> <external asm_shf.FCStd>#Assembly
  Origin = -> Origin001
  Placement = pos=(38,-53.8,0) rot=(0.57735,0.57735,-0.57735;4.18879rad)
  Rigid = true
FEATURE [App::Link] SHF013
  LinkedObject = -> <external asm_shf.FCStd>#SHF12
FEATURE [App::Link] Hex_socket_head_cap_screw_DIN_912_M4_15_001  label="Hex socket head cap screw DIN 912 M4 15.001"
  LinkPlacement = pos=(12.25,6.5,11.5) rot=(0,-1,0;1.5708rad)
  LinkedObject = -> <external asm_shf.FCStd>#Hex_socket_head_cap_screw_DIN_912_M4_15_0
  Placement = pos=(12.25,6.5,11.5) rot=(0,-1,0;1.5708rad)
FEATURE [App::Link] Hex_socket_head_cap_screw_DIN_912_M5_15_002  label="Hex socket head cap screw DIN 912 M5 15.002"
  LinkPlacement = pos=(18,11,1.16e-14) rot=(0.57735,-0.57735,0.57735;2.0944rad)
  LinkedObject = -> <external asm_shf.FCStd>#Hex_socket_head_cap_screw_DIN_912_M5_15_0
  Placement = pos=(18,11,1.16e-14) rot=(0.57735,-0.57735,0.57735;2.0944rad)
FEATURE [App::Link] Hex_socket_head_cap_screw_DIN_912_M5_15_003  label="Hex socket head cap screw DIN 912 M5 15.003"
  LinkPlacement = pos=(-18,11,1.16e-14) rot=(0.57735,-0.57735,0.57735;2.0944rad)
  LinkedObject = -> <external asm_shf.FCStd>#Hex_socket_head_cap_screw_DIN_912_M5_15_001
  Placement = pos=(-18,11,1.16e-14) rot=(0.57735,-0.57735,0.57735;2.0944rad)
FEATURE [Assembly::AssemblyLink] asm_SHF001
  Group = -> [SHF013,Hex_socket_head_cap_screw_DIN_912_M4_15_001,Hex_socket_head_cap_screw_DIN_912_M5_15_002,Hex_socket_head_cap_screw_DIN_912_M5_15_003]
  LinkedObject = -> <external asm_shf.FCStd>#Assembly
  Origin = -> Origin002
  Placement = pos=(-38,-53.8,0) rot=(0.57735,0.57735,-0.57735;4.18879rad)
  Rigid = true
FEATURE [App::FeaturePython] Joint  label="Fixed"  # Assembly joint (typed FeaturePython)
  Activated = true
  AngleMax = 0
  AngleMin = 0
  Detach1 = false
  Detach2 = false
  Distance = 0
  Distance2 = 0
  EnableAngleMax = false
  EnableAngleMin = false
  EnableLengthMax = false
  EnableLengthMin = false
  JointType = 0 (Fixed)
  LengthMax = 0
  LengthMin = 0
  Placement1 = pos=(18,0,1.16e-14) rot=(-0.57735,0.57735,0.57735;2.0944rad)
  Placement2 = pos=(38,-35.8,0) rot=(0,0,1;0rad)
  Reference1 = -> Assembly [asm_SHF.SHF12.Edge23,asm_SHF.SHF12.Edge23]
  Reference2 = -> Assembly [plate_roof001.Edge35,plate_roof001.Edge35]
FEATURE [App::FeaturePython] Joint001  label="Fixed001"  # Assembly joint (typed FeaturePython)
  Activated = true
  AngleMax = 0
  AngleMin = 0
  Detach1 = false
  Detach2 = false
  Distance = 0
  Distance2 = 0
  EnableAngleMax = false
  EnableAngleMin = false
  EnableLengthMax = false
  EnableLengthMin = false
  JointType = 0 (Fixed)
  LengthMax = 0
  LengthMin = 0
  Placement1 = pos=(18,0,1.16e-14) rot=(-0.57735,0.57735,0.57735;2.0944rad)
  Placement2 = pos=(-38,-35.8,0) rot=(0,0,1;0rad)
  Reference1 = -> Assembly [asm_SHF001.SHF013.Edge23,asm_SHF001.SHF013.Edge23]
  Reference2 = -> Assembly [plate_roof001.Edge41,plate_roof001.Edge41]
FEATURE [App::FeaturePython] Joint002  label="Slider"  # Assembly joint (typed FeaturePython)
  Activated = true
  AngleMax = 0
  AngleMin = 0
  Detach1 = false
  Detach2 = false
  Distance = 0
  Distance2 = 0
  EnableAngleMax = false
  EnableAngleMin = false
  EnableLengthMax = false
  EnableLengthMin = true
  JointType = 3 (Slider)
  LengthMax = 38.1914
  LengthMin = 2.13595
  Placement2 = pos=(0,13,0) rot=(-0.57735,-0.57735,0.57735;4.18879rad)
  Reference1 = -> Assembly [linear_slide001.Edge2,linear_slide001.Edge2]
  Reference2 = -> Assembly [asm_SHF.SHF12.Edge3,asm_SHF.SHF12.Edge3]
FEATURE [App::FeaturePython] Joint003  label="Slider001"  # Assembly joint (typed FeaturePython)
  Activated = true
  AngleMax = 0
  AngleMin = 0
  Detach1 = false
  Detach2 = false
  Distance = 0
  Distance2 = 0
  EnableAngleMax = false
  EnableAngleMin = false
  EnableLengthMax = false
  EnableLengthMin = false
  JointType = 3 (Slider)
  LengthMax = 0
  LengthMin = 0
  Placement2 = pos=(0,13,0) rot=(-0.57735,-0.57735,0.57735;4.18879rad)
  Reference1 = -> Assembly [linear_slide.Edge2,linear_slide.Edge2]
  Reference2 = -> Assembly [asm_SHF001.SHF013.Edge3,asm_SHF001.SHF013.Edge3]
FEATURE [App::FeaturePython] Joint004  label="Fixed002"  # Assembly joint (typed FeaturePython)
  Activated = true
  AngleMax = 0
  AngleMin = 0
  Detach1 = false
  Detach2 = false
  Distance = 0
  Distance2 = 0
  EnableAngleMax = false
  EnableAngleMin = false
  EnableLengthMax = false
  EnableLengthMin = false
  JointType = 0 (Fixed)
  LengthMax = 0
  LengthMin = 0
  Offset2 = pos=(0,0,0) rot=(0,0,1;3.14159rad)
  Placement1 = pos=(0,13,0) rot=(-0.57735,-0.57735,0.57735;4.18879rad)
  Placement2 = pos=(0,0,100) rot=(0,0,1;3.14159rad)
  Reference1 = -> Assembly [asm_cam_holder.asm_SHF001.SHF013.Edge3,asm_cam_holder.asm_SHF001.SHF013.Edge3]
  Reference2 = -> Assembly [linear_slide001.Edge3,linear_slide001.Edge3]
FEATURE [App::FeaturePython] Joint005  label="Fixed003"  # Assembly joint (typed FeaturePython)
  Activated = true
  AngleMax = 0
  AngleMin = 0
  Detach1 = false
  Detach2 = false
  Distance = 0
  Distance2 = 0
  EnableAngleMax = false
  EnableAngleMin = false
  EnableLengthMax = false
  EnableLengthMin = false
  JointType = 0 (Fixed)
  LengthMax = 0
  LengthMin = 0
  Placement1 = pos=(0,0,100) rot=(0,0,1;0rad)
  Placement2 = pos=(0,13,0) rot=(-0.57735,-0.57735,0.57735;4.18879rad)
  Reference1 = -> Assembly [linear_slide.Edge3,linear_slide.Edge3]
  Reference2 = -> Assembly [asm_cam_holder.asm_SHF.SHF12.Edge3,asm_cam_holder.asm_SHF.SHF12.Edge3]
FEATURE [App::Link] Hexagonal_Nut_M5_CBALN5  label="Hexagonal Nut M5_CBALN5"
  LinkPlacement = pos=(-38,-71.8,66.8641) rot=(0,1,0;4.71239rad)
  LinkedObject = -> <external ../secondary/nuts_hexagonal.FCStd>#Part__Feature001
  Placement = pos=(-38,-71.8,66.8641) rot=(0,1,0;4.71239rad)
FEATURE [App::Link] Hexagonal_Nut_M5_CBALN006  label="Hexagonal Nut M5_CBALN006"
  LinkPlacement = pos=(38,-71.8,66.864) rot=(0.707107,0,0.707107;3.14159rad)
  LinkedObject = -> <external ../secondary/nuts_hexagonal.FCStd>#Part__Feature001
  Placement = pos=(38,-71.8,66.864) rot=(0.707107,0,0.707107;3.14159rad)
FEATURE [App::Link] Hexagonal_Nut_M5_CBALN007  label="Hexagonal Nut M5_CBALN007"
  LinkPlacement = pos=(-38,-35.8,66.8641) rot=(0,-1,0;1.5708rad)
  LinkedObject = -> <external ../secondary/nuts_hexagonal.FCStd>#Part__Feature001
  Placement = pos=(-38,-35.8,66.8641) rot=(0,-1,0;1.5708rad)
FEATURE [App::Link] Hexagonal_Nut_M5_CBALN008  label="Hexagonal Nut M5_CBALN008"
  LinkPlacement = pos=(38,-35.8,66.864) rot=(0.707107,0,0.707107;3.14159rad)
  LinkedObject = -> <external ../secondary/nuts_hexagonal.FCStd>#Part__Feature001
  Placement = pos=(38,-35.8,66.864) rot=(0.707107,0,0.707107;3.14159rad)
FEATURE [App::FeaturePython] Joint006  label="Fixed004"  # Assembly joint (typed FeaturePython)
  Activated = true
  AngleMax = 0
  AngleMin = 0
  Detach1 = false
  Detach2 = false
  Distance = 0
  Distance2 = 0
  EnableAngleMax = false
  EnableAngleMin = false
  EnableLengthMax = false
  EnableLengthMin = false
  JointType = 0 (Fixed)
  LengthMax = 0
  LengthMin = 0
  Offset2 = pos=(0,0,-11) rot=(0,0,1;0rad)
  Placement1 = pos=(0,0,0) rot=(0,-1,0;1.5708rad)
  Placement2 = pos=(-1.8e-15,-7e-15,16) rot=(0,0,1;0rad)
  Reference1 = -> Assembly [Hexagonal_Nut_M5_CBALN008.Edge48,Hexagonal_Nut_M5_CBALN008.Edge48]
  Reference2 = -> Assembly [asm_cam_holder.asm_SHF001.Hex_socket_head_cap_screw_DIN_912_M5_15_002.Edge11,asm_cam_holder.asm_SHF001.Hex_socket_head_cap_screw_DIN_912_M5_15_002.Edge11]
FEATURE [App::FeaturePython] Joint007  label="Fixed005"  # Assembly joint (typed FeaturePython)
  Activated = true
  AngleMax = 0
  AngleMin = 0
  Detach1 = false
  Detach2 = false
  Distance = 0
  Distance2 = 0
  EnableAngleMax = false
  EnableAngleMin = false
  EnableLengthMax = false
  EnableLengthMin = false
  JointType = 0 (Fixed)
  LengthMax = 0
  LengthMin = 0
  Offset2 = pos=(0,0,-11) rot=(0,0,1;0rad)
  Placement1 = pos=(0,0,0) rot=(0,-1,0;1.5708rad)
  Placement2 = pos=(0,-3.6e-15,16) rot=(0,0,1;0rad)
  Reference1 = -> Assembly [Hexagonal_Nut_M5_CBALN006.Edge28,Hexagonal_Nut_M5_CBALN006.Edge28]
  Reference2 = -> Assembly [asm_cam_holder.asm_SHF001.Hex_socket_head_cap_screw_DIN_912_M5_15_003.Edge11,asm_cam_holder.asm_SHF001.Hex_socket_head_cap_screw_DIN_912_M5_15_003.Edge11]
FEATURE [App::FeaturePython] Joint008  label="Fixed006"  # Assembly joint (typed FeaturePython)
  Activated = true
  AngleMax = 0
  AngleMin = 0
  Detach1 = false
  Detach2 = false
  Distance = 0
  Distance2 = 0
  EnableAngleMax = false
  EnableAngleMin = false
  EnableLengthMax = false
  EnableLengthMin = false
  JointType = 0 (Fixed)
  LengthMax = 0
  LengthMin = 0
  Offset2 = pos=(0,0,-11) rot=(0,0,1;0rad)
  Placement1 = pos=(0,0,0) rot=(0,1,0;4.71239rad)
  Placement2 = pos=(0,-3.6e-15,16) rot=(0,0,1;0rad)
  Reference1 = -> Assembly [Hexagonal_Nut_M5_CBALN007.Edge28,Hexagonal_Nut_M5_CBALN007.Edge28]
  Reference2 = -> Assembly [asm_cam_holder.asm_SHF.Hex_socket_head_cap_screw_DIN_912_M5_15_001.Edge11,asm_cam_holder.asm_SHF.Hex_socket_head_cap_screw_DIN_912_M5_15_001.Edge11]
FEATURE [App::FeaturePython] Joint009  label="Fixed007"  # Assembly joint (typed FeaturePython)
  Activated = true
  AngleMax = 0
  AngleMin = 0
  Detach1 = false
  Detach2 = false
  Distance = 0
  Distance2 = 0
  EnableAngleMax = false
  EnableAngleMin = false
  EnableLengthMax = false
  EnableLengthMin = false
  JointType = 0 (Fixed)
  LengthMax = 0
  LengthMin = 0
  Offset2 = pos=(0,0,-11) rot=(0,0,1;0rad)
  Placement1 = pos=(0,0,0) rot=(0,-1,0;1.5708rad)
  Placement2 = pos=(-1.8e-15,-7e-15,16) rot=(0,0,1;0rad)
  Reference1 = -> Assembly [Hexagonal_Nut_M5_CBALN5.Edge28,Hexagonal_Nut_M5_CBALN5.Edge28]
  Reference2 = -> Assembly [asm_cam_holder.asm_SHF.Hex_socket_head_cap_screw_DIN_912_M5_15_0.Edge11,asm_cam_holder.asm_SHF.Hex_socket_head_cap_screw_DIN_912_M5_15_0.Edge11]
FEATURE [App::Link] Hexagonal_Nut_M4_CBALN4  label="Hexagonal Nut M4_CBALN4"
  LinkPlacement = pos=(32.96,-17.7689,66.8641) rot=(0.707107,0,0.707107;3.14159rad)
  LinkedObject = -> <external ../secondary/nuts_hexagonal.FCStd>#Part__Feature
  Placement = pos=(32.96,-17.7689,66.8641) rot=(0.707107,0,0.707107;3.14159rad)
FEATURE [App::Link] Hexagonal_Nut_M4_CBALN005  label="Hexagonal Nut M4_CBALN005"
  LinkPlacement = pos=(-32.96,-17.7689,66.8641) rot=(0.707107,0,0.707107;3.14159rad)
  LinkedObject = -> <external ../secondary/nuts_hexagonal.FCStd>#Part__Feature
  Placement = pos=(-32.96,-17.7689,66.8641) rot=(0.707107,0,0.707107;3.14159rad)
FEATURE [App::Link] Hexagonal_Nut_M4_CBALN006  label="Hexagonal Nut M4_CBALN006"
  LinkPlacement = pos=(-32.96,20.2311,66.8641) rot=(0.707107,0,0.707107;3.14159rad)
  LinkedObject = -> <external ../secondary/nuts_hexagonal.FCStd>#Part__Feature
  Placement = pos=(-32.96,20.2311,66.8641) rot=(0.707107,0,0.707107;3.14159rad)
FEATURE [App::Link] Hexagonal_Nut_M4_CBALN007  label="Hexagonal Nut M4_CBALN007"
  LinkPlacement = pos=(32.96,20.2311,66.864) rot=(0.707107,0,0.707107;3.14159rad)
  LinkedObject = -> <external ../secondary/nuts_hexagonal.FCStd>#Part__Feature
  Placement = pos=(32.96,20.2311,66.864) rot=(0.707107,0,0.707107;3.14159rad)
FEATURE [App::FeaturePython] Joint010  label="Fixed008"  # Assembly joint (typed FeaturePython)
  Activated = true
  AngleMax = 0
  AngleMin = 0
  Detach1 = false
  Detach2 = false
  Distance = 0
  Distance2 = 0
  EnableAngleMax = false
  EnableAngleMin = false
  EnableLengthMax = false
  EnableLengthMin = false
  JointType = 0 (Fixed)
  LengthMax = 0
  LengthMin = 0
  Offset2 = pos=(0,0,3) rot=(0,0,1;0rad)
  Placement1 = pos=(0,0,0) rot=(0,-1,0;1.5708rad)
  Placement2 = pos=(-6.98683,35.5575,3) rot=(0,0,1;0rad)
  Reference1 = -> Assembly [Hexagonal_Nut_M4_CBALN007.Edge31,Hexagonal_Nut_M4_CBALN007.Edge31]
  Reference2 = -> Assembly [asm_cam_holder.asm_cam_mount.Hex_screw_M4_10_003.Edge2,asm_cam_holder.asm_cam_mount.Hex_screw_M4_10_003.Edge2]
FEATURE [App::FeaturePython] Joint011  label="Fixed009"  # Assembly joint (typed FeaturePython)
  Activated = true
  AngleMax = 0
  AngleMin = 0
  Detach1 = false
  Detach2 = false
  Distance = 0
  Distance2 = 0
  EnableAngleMax = false
  EnableAngleMin = false
  EnableLengthMax = false
  EnableLengthMin = false
  JointType = 0 (Fixed)
  LengthMax = 0
  LengthMin = 0
  Offset2 = pos=(0,0,3) rot=(0,0,1;0rad)
  Placement1 = pos=(0,0,0) rot=(0,-1,0;1.5708rad)
  Placement2 = pos=(-6.98683,35.5575,3) rot=(0,0,1;0rad)
  Reference1 = -> Assembly [Hexagonal_Nut_M4_CBALN006.Edge31,Hexagonal_Nut_M4_CBALN006.Edge31]
  Reference2 = -> Assembly [asm_cam_holder.asm_cam_mount.Hex_screw_M4_10_001.Edge2,asm_cam_holder.asm_cam_mount.Hex_screw_M4_10_001.Edge2]
FEATURE [App::FeaturePython] Joint012  label="Fixed010"  # Assembly joint (typed FeaturePython)
  Activated = true
  AngleMax = 0
  AngleMin = 0
  Detach1 = false
  Detach2 = false
  Distance = 0
  Distance2 = 0
  EnableAngleMax = false
  EnableAngleMin = false
  EnableLengthMax = false
  EnableLengthMin = false
  JointType = 0 (Fixed)
  LengthMax = 0
  LengthMin = 0
  Offset2 = pos=(0,0,3) rot=(0,0,1;0rad)
  Placement1 = pos=(0,0,0) rot=(0,-1,0;1.5708rad)
  Placement2 = pos=(-6.98683,35.5575,3) rot=(0,0,1;0rad)
  Reference1 = -> Assembly [Hexagonal_Nut_M4_CBALN005.Edge31,Hexagonal_Nut_M4_CBALN005.Edge31]
  Reference2 = -> Assembly [asm_cam_holder.asm_cam_mount.Hex_screw_M4_10_0.Edge2,asm_cam_holder.asm_cam_mount.Hex_screw_M4_10_0.Edge2]
FEATURE [App::FeaturePython] Joint013  label="Fixed011"  # Assembly joint (typed FeaturePython)
  Activated = true
  AngleMax = 0
  AngleMin = 0
  Detach1 = false
  Detach2 = false
  Distance = 0
  Distance2 = 0
  EnableAngleMax = false
  EnableAngleMin = false
  EnableLengthMax = false
  EnableLengthMin = false
  JointType = 0 (Fixed)
  LengthMax = 0
  LengthMin = 0
  Offset2 = pos=(0,0,3) rot=(0,0,1;0rad)
  Placement1 = pos=(0,0,0) rot=(0,-1,0;1.5708rad)
  Placement2 = pos=(-6.98683,35.5575,3) rot=(0,0,1;0rad)
  Reference1 = -> Assembly [Hexagonal_Nut_M4_CBALN4.Edge31,Hexagonal_Nut_M4_CBALN4.Edge31]
  Reference2 = -> Assembly [asm_cam_holder.asm_cam_mount.Hex_screw_M4_10_002.Edge2,asm_cam_holder.asm_cam_mount.Hex_screw_M4_10_002.Edge2]
FEATURE [Assembly::JointGroup] Joints
  Group = -> [GroundedJoint,Joint,Joint001,Joint002,Joint003,Joint004,Joint005,Joint006,Joint007,Joint008,Joint009,Joint010,Joint011,Joint012,Joint013]
FEATURE [Assembly::AssemblyObject] Assembly  label="asm_roof"
  Group = -> [Joints,plate_roof001,GroundedJoint,linear_slide,linear_slide001,asm_cam_holder,asm_SHF,asm_SHF001,Joint,Joint001,Joint002,Joint003,Joint004,Joint005,Hexagonal_Nut_M5_CBALN5,Hexagonal_Nut_M5_CBALN006,Hexagonal_Nut_M5_CBALN007,Hexagonal_Nut_M5_CBALN008,Joint006,Joint007,Joint008,Joint009,Hexagonal_Nut_M4_CBALN4,Hexagonal_Nut_M4_CBALN005,Hexagonal_Nut_M4_CBALN006,Hexagonal_Nut_M4_CBALN007,Joint010,+3 more]
  Origin = -> Origin
  Type = Assembly
---- part asm_shf.FCStd = doc fcstd_04160f494026 ----
FCSTD DOCUMENT  (FreeCAD 1.0R39109 (Git))
Label: asm_shf
License: All rights reserved
LicenseURL: https://en.wikipedia.org/wiki/All_rights_reserved
objects: App::Link×4, App::FeaturePython×3, Assembly::JointGroup×1, Assembly::AssemblyObject×1
EXTERNAL_REF file=../downloads/linear-bearing-shaft-support-shf12-1.snapshot.1/SHF_12.FCStd obj=Part__Feature
EXTERNAL_REF file=../secondary/bolts.FCStd obj=BOLTS_part001
EXTERNAL_REF file=../secondary/bolts.FCStd obj=BOLTS_part004

FEATURE [App::Link] SHF12
  LinkedObject = -> <external ../downloads/linear-bearing-shaft-support-shf12-1.snapshot.1/SHF_12.FCStd>#Part__Feature
FEATURE [App::FeaturePython] GroundedJoint  # Assembly grounded joint (typed FeaturePython)
  ObjectToGround = -> SHF12
FEATURE [App::Link] Hex_socket_head_cap_screw_DIN_912_M4_15_0  label="Hex socket head cap screw DIN 912 M4 15.0"
  LinkPlacement = pos=(12.25,6.5,11.5) rot=(0,-1,0;1.5708rad)
  LinkedObject = -> <external ../secondary/bolts.FCStd>#BOLTS_part001
  Placement = pos=(12.25,6.5,11.5) rot=(0,-1,0;1.5708rad)
FEATURE [App::Link] Hex_socket_head_cap_screw_DIN_912_M5_15_0  label="Hex socket head cap screw DIN 912 M5 15.0"
  LinkPlacement = pos=(18,11,1.16e-14) rot=(0.57735,-0.57735,0.57735;2.0944rad)
  LinkedObject = -> <external ../secondary/bolts.FCStd>#BOLTS_part004
  Placement = pos=(18,11,1.16e-14) rot=(0.57735,-0.57735,0.57735;2.0944rad)
FEATURE [App::Link] Hex_socket_head_cap_screw_DIN_912_M5_15_001  label="Hex socket head cap screw DIN 912 M5 15.001"
  LinkPlacement = pos=(-18,11,1.16e-14) rot=(0.57735,-0.57735,0.57735;2.0944rad)
  LinkedObject = -> <external ../secondary/bolts.FCStd>#BOLTS_part004
  Placement = pos=(-18,11,1.16e-14) rot=(0.57735,-0.57735,0.57735;2.0944rad)
FEATURE [App::FeaturePython] Joint001  label="Fixed001"  # Assembly joint (typed FeaturePython)
  Activated = true
  AngleMax = 0
  AngleMin = 0
  Detach1 = false
  Detach2 = false
  Distance = 0
  Distance2 = 0
  EnableAngleMax = false
  EnableAngleMin = false
  EnableLengthMax = false
  EnableLengthMin = false
  JointType = 0 (Fixed)
  LengthMax = 0
  LengthMin = 0
  Placement1 = pos=(-18,6,1.16e-14) rot=(0.57735,0.57735,0.57735;4.18879rad)
  Placement2 = pos=(-6e-16,-3.6e-15,5) rot=(0,0,1;0rad)
  Reference1 = -> Assembly [SHF12.Edge68,SHF12.Edge68]
  Reference2 = -> Assembly [Hex_socket_head_cap_screw_DIN_912_M5_15_001.Edge4,Hex_socket_head_cap_screw_DIN_912_M5_15_001.Edge4]
FEATURE [App::FeaturePython] Joint002  label="Fixed002"  # Assembly joint (typed FeaturePython)
  Activated = true
  AngleMax = 0
  AngleMin = 0
  Detach1 = false
  Detach2 = false
  Distance = 0
  Distance2 = 0
  EnableAngleMax = false
  EnableAngleMin = false
  EnableLengthMax = false
  EnableLengthMin = false
  JointType = 0 (Fixed)
  LengthMax = 0
  LengthMin = 0
FEATURE [Assembly::JointGroup] Joints
  Group = -> [GroundedJoint,Joint001,Joint002]
FEATURE [Assembly::AssemblyObject] Assembly  label="asm_SHF"
  Group = -> [Joints,SHF12,GroundedJoint,Hex_socket_head_cap_screw_DIN_912_M4_15_0,Hex_socket_head_cap_screw_DIN_912_M5_15_0,Hex_socket_head_cap_screw_DIN_912_M5_15_001,Joint001,Joint002]
  Origin = -> Origin
  Type = Assembly
---- part roof_holder_asm.FCStd = doc fcstd_db53f0c2c757 ----
FCSTD DOCUMENT  (FreeCAD 1.0R39109 (Git))
Label: roof_holder_asm
License: All rights reserved
LicenseURL: https://en.wikipedia.org/wiki/All_rights_reserved
objects: App::Link×3, App::FeaturePython×3, Assembly::JointGroup×1, Assembly::AssemblyObject×1
EXTERNAL_REF file=../parts/roof_holder.FCStd obj=Body
EXTERNAL_REF file=dbox_asm.FCStd obj=BOLTS_part

FEATURE [App::Link] roof_holder
  LinkedObject = -> <external ../parts/roof_holder.FCStd>#Body
FEATURE [App::FeaturePython] GroundedJoint  # Assembly grounded joint (typed FeaturePython)
  ObjectToGround = -> roof_holder
FEATURE [App::Link] Hex_socket_countersunk_head_screw_ISO_10642_M5_15_0  label="Hex socket countersunk head screw ISO 10642 M5 15.0"
  LinkPlacement = pos=(12,7e-16,8.8) rot=(1,0,0;3.14159rad)
  LinkedObject = -> <external dbox_asm.FCStd>#BOLTS_part
  Placement = pos=(12,7e-16,8.8) rot=(1,0,0;3.14159rad)
FEATURE [App::Link] Hex_socket_countersunk_head_screw_ISO_10642_M5_15_001  label="Hex socket countersunk head screw ISO 10642 M5 15.001"
  LinkPlacement = pos=(-12,7e-16,8.8) rot=(1,0,0;3.14159rad)
  LinkedObject = -> <external dbox_asm.FCStd>#BOLTS_part
  Placement = pos=(-12,7e-16,8.8) rot=(1,0,0;3.14159rad)
FEATURE [App::FeaturePython] Joint  label="Fixed"  # Assembly joint (typed FeaturePython)
  Activated = true
  AngleMax = 0
  AngleMin = 0
  Detach1 = false
  Detach2 = false
  Distance = 0
  Distance2 = 0
  EnableAngleMax = false
  EnableAngleMin = false
  EnableLengthMax = false
  EnableLengthMin = false
  JointType = 0 (Fixed)
  LengthMax = 0
  LengthMin = 0
  Placement1 = pos=(-12,7e-16,6) rot=(0,0,1;0rad)
  Placement2 = pos=(0,0,2.8) rot=(0,0,1;0rad)
  Reference1 = -> Assembly [roof_holder.Edge21,roof_holder.Edge21]
  Reference2 = -> Assembly [Hex_socket_countersunk_head_screw_ISO_10642_M5_15_001.Edge1,Hex_socket_countersunk_head_screw_ISO_10642_M5_15_001.Edge1]
FEATURE [App::FeaturePython] Joint001  label="Fixed001"  # Assembly joint (typed FeaturePython)
  Activated = true
  AngleMax = 0
  AngleMin = 0
  Detach1 = false
  Detach2 = false
  Distance = 0
  Distance2 = 0
  EnableAngleMax = false
  EnableAngleMin = false
  EnableLengthMax = false
  EnableLengthMin = false
  JointType = 0 (Fixed)
  LengthMax = 0
  LengthMin = 0
  Placement1 = pos=(0,0,2.8) rot=(0,0,1;0rad)
  Placement2 = pos=(12,7e-16,6) rot=(0,0,1;0rad)
  Reference1 = -> Assembly [Hex_socket_countersunk_head_screw_ISO_10642_M5_15_0.Edge1,Hex_socket_countersunk_head_screw_ISO_10642_M5_15_0.Edge1]
  Reference2 = -> Assembly [roof_holder.Edge2,roof_holder.Edge2]
FEATURE [Assembly::JointGroup] Joints
  Group = -> [GroundedJoint,Joint,Joint001]
FEATURE [Assembly::AssemblyObject] Assembly  label="asm_roof_holder"
  Group = -> [Joints,roof_holder,GroundedJoint,Hex_socket_countersunk_head_screw_ISO_10642_M5_15_0,Hex_socket_countersunk_head_screw_ISO_10642_M5_15_001,Joint,Joint001]
  Origin = -> Origin
  Type = Assembly
